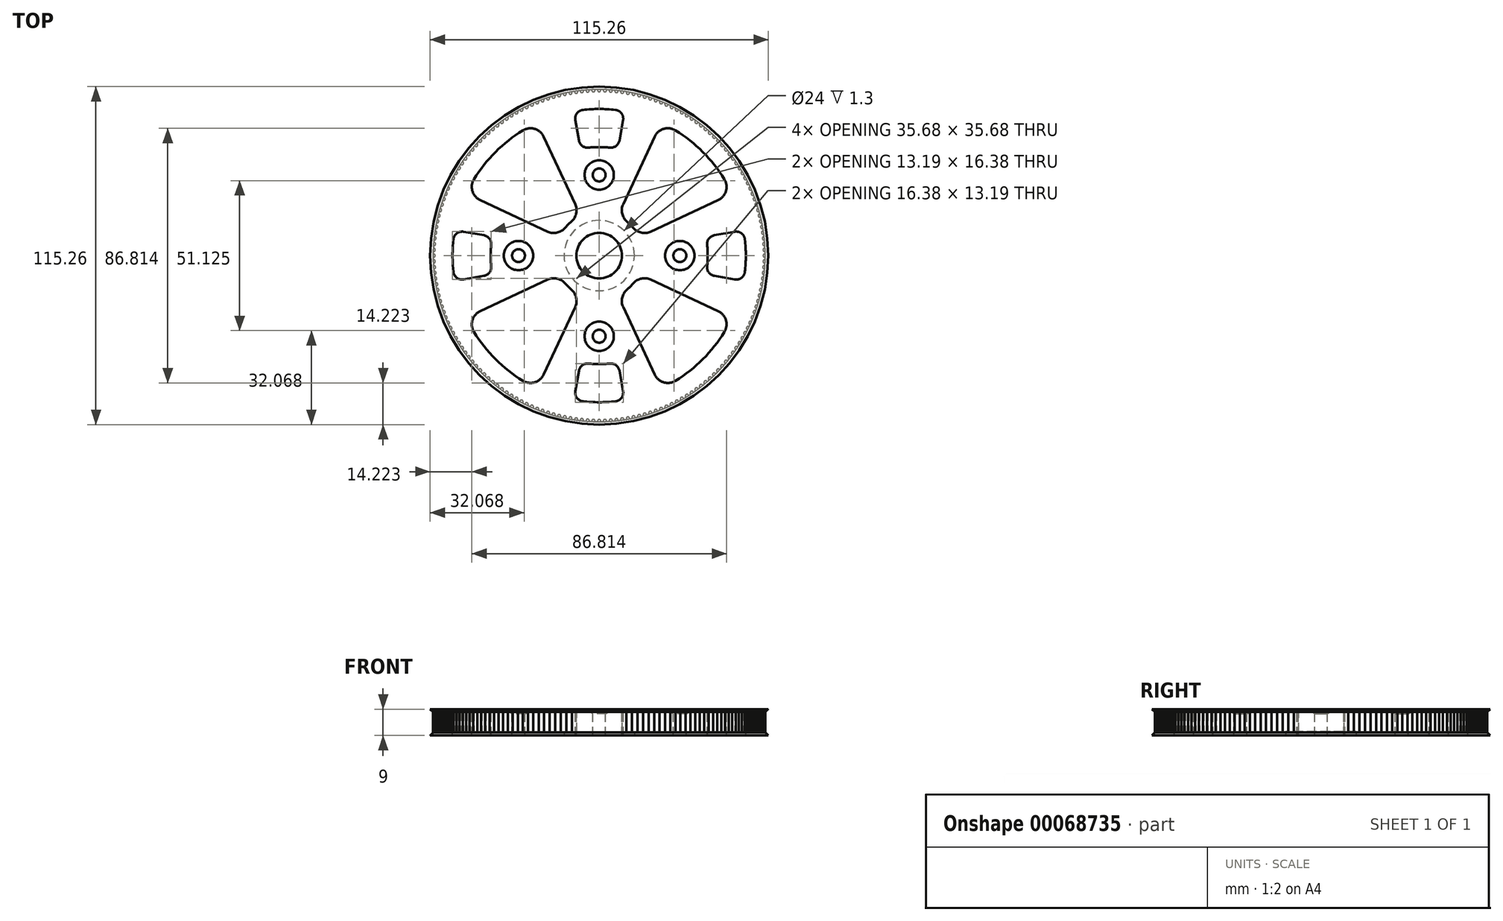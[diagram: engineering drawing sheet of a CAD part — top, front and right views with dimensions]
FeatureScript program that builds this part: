
annotation { "Feature Type Name" : "Feature", "Feature Type Description" : "" }
export const myFeature = defineFeature(function(context is Context, id is Id, definition is map)
    precondition{}
    {
        {
            var Q0;
            Q0=qCreatedBy(makeId("Top.planeOp"),FACE);
            var sketch = newSketch(context, id + "F0", { "sketchPlane" : qUnion([Q0])});
            skCircle(sketch, "E0", {"center": v(0, 0) * mm, "radius": 55.88 * mm, "construction": true});
            skCircle(sketch, "E1", {"center": v(0, 0) * mm, "radius": 56.63 * mm});
            skArc(sketch, "E2", {"start": v(0, -55.88) * mm, "mid": v(-0.3, -55.96) * mm, "end": v(-0.5, -56.2) * mm});
            skArc(sketch, "E3", {"start": v(-0.5, -56.2) * mm, "mid": v(-0.56, -56.32) * mm, "end": v(-0.59, -56.45) * mm});
            skArc(sketch, "E4", {"start": v(-0.59, -56.45) * mm, "mid": v(-0.66, -56.57) * mm, "end": v(-0.79, -56.62) * mm});
            skArc(sketch, "E5.MirrorCS", {"start": v(0, -55.88) * mm, "mid": v(0.3, -55.96) * mm, "end": v(0.5, -56.2) * mm});
            skArc(sketch, "E6.MirrorCS", {"start": v(0.5, -56.2) * mm, "mid": v(0.56, -56.32) * mm, "end": v(0.59, -56.45) * mm});
            skArc(sketch, "E7.MirrorCS", {"start": v(0.59, -56.45) * mm, "mid": v(0.66, -56.57) * mm, "end": v(0.79, -56.62) * mm});
            skArc(sketch, "E8.1.0", {"start": v(1.38, -56.44) * mm, "mid": v(1.32, -56.56) * mm, "end": v(1.19, -56.61) * mm});
            skArc(sketch, "E8.1.1", {"start": v(1.46, -56.18) * mm, "mid": v(1.41, -56.3) * mm, "end": v(1.38, -56.44) * mm});
            skArc(sketch, "E8.1.2", {"start": v(1.95, -55.84) * mm, "mid": v(1.65, -55.94) * mm, "end": v(1.46, -56.18) * mm});
            skArc(sketch, "E8.1.3", {"start": v(1.95, -55.84) * mm, "mid": v(2.25, -55.92) * mm, "end": v(2.47, -56.15) * mm});
            skArc(sketch, "E8.1.4", {"start": v(2.47, -56.15) * mm, "mid": v(2.52, -56.27) * mm, "end": v(2.56, -56.4) * mm});
            skArc(sketch, "E8.1.5", {"start": v(2.56, -56.4) * mm, "mid": v(2.63, -56.52) * mm, "end": v(2.76, -56.56) * mm});
            skArc(sketch, "E8.2.0", {"start": v(3.35, -56.36) * mm, "mid": v(3.3, -56.48) * mm, "end": v(3.16, -56.54) * mm});
            skArc(sketch, "E8.2.1", {"start": v(3.41, -56.1) * mm, "mid": v(3.37, -56.22) * mm, "end": v(3.35, -56.36) * mm});
            skArc(sketch, "E8.2.2", {"start": v(3.9, -55.74) * mm, "mid": v(3.6, -55.85) * mm, "end": v(3.41, -56.1) * mm});
            skArc(sketch, "E8.2.3", {"start": v(3.9, -55.74) * mm, "mid": v(4.2, -55.8) * mm, "end": v(4.43, -56.02) * mm});
            skArc(sketch, "E8.2.4", {"start": v(4.43, -56.02) * mm, "mid": v(4.48, -56.15) * mm, "end": v(4.52, -56.28) * mm});
            skArc(sketch, "E8.2.5", {"start": v(4.52, -56.28) * mm, "mid": v(4.6, -56.4) * mm, "end": v(4.74, -56.43) * mm});
            skArc(sketch, "E8.3.0", {"start": v(5.32, -56.2) * mm, "mid": v(5.26, -56.33) * mm, "end": v(5.14, -56.4) * mm});
            skArc(sketch, "E8.3.1", {"start": v(5.37, -55.94) * mm, "mid": v(5.33, -56.07) * mm, "end": v(5.32, -56.2) * mm});
            skArc(sketch, "E8.3.2", {"start": v(5.84, -55.57) * mm, "mid": v(5.55, -55.69) * mm, "end": v(5.37, -55.94) * mm});
            skArc(sketch, "E8.3.3", {"start": v(5.84, -55.57) * mm, "mid": v(6.15, -55.62) * mm, "end": v(6.38, -55.84) * mm});
            skArc(sketch, "E8.3.4", {"start": v(6.38, -55.84) * mm, "mid": v(6.44, -55.96) * mm, "end": v(6.49, -56.08) * mm});
            skArc(sketch, "E8.3.5", {"start": v(6.49, -56.08) * mm, "mid": v(6.57, -56.2) * mm, "end": v(6.7, -56.23) * mm});
            skArc(sketch, "E8.4.0", {"start": v(7.27, -55.99) * mm, "mid": v(7.22, -56.12) * mm, "end": v(7.1, -56.18) * mm});
            skArc(sketch, "E8.4.1", {"start": v(7.32, -55.72) * mm, "mid": v(7.29, -55.85) * mm, "end": v(7.27, -55.99) * mm});
            skArc(sketch, "E8.4.2", {"start": v(7.78, -55.33) * mm, "mid": v(7.5, -55.46) * mm, "end": v(7.32, -55.72) * mm});
            skArc(sketch, "E8.4.3", {"start": v(7.78, -55.33) * mm, "mid": v(8.09, -55.38) * mm, "end": v(8.32, -55.58) * mm});
            skArc(sketch, "E8.4.4", {"start": v(8.32, -55.58) * mm, "mid": v(8.39, -55.7) * mm, "end": v(8.44, -55.82) * mm});
            skArc(sketch, "E8.4.5", {"start": v(8.44, -55.82) * mm, "mid": v(8.52, -55.93) * mm, "end": v(8.66, -55.96) * mm});
            skArc(sketch, "E8.5.0", {"start": v(9.22, -55.7) * mm, "mid": v(9.18, -55.83) * mm, "end": v(9.06, -55.9) * mm});
            skArc(sketch, "E8.5.1", {"start": v(9.26, -55.43) * mm, "mid": v(9.23, -55.56) * mm, "end": v(9.22, -55.7) * mm});
            skArc(sketch, "E8.5.2", {"start": v(9.7, -55.03) * mm, "mid": v(9.42, -55.16) * mm, "end": v(9.26, -55.43) * mm});
            skArc(sketch, "E8.5.3", {"start": v(9.7, -55.03) * mm, "mid": v(10.01, -55.06) * mm, "end": v(10.26, -55.26) * mm});
            skArc(sketch, "E8.5.4", {"start": v(10.26, -55.26) * mm, "mid": v(10.33, -55.37) * mm, "end": v(10.38, -55.5) * mm});
            skArc(sketch, "E8.5.5", {"start": v(10.38, -55.5) * mm, "mid": v(10.47, -55.6) * mm, "end": v(10.6, -55.62) * mm});
            skArc(sketch, "E8.6.0", {"start": v(11.16, -55.34) * mm, "mid": v(11.12, -55.47) * mm, "end": v(11, -55.55) * mm});
            skArc(sketch, "E8.6.1", {"start": v(11.19, -55.07) * mm, "mid": v(11.17, -55.2) * mm, "end": v(11.16, -55.34) * mm});
            skArc(sketch, "E8.6.2", {"start": v(11.62, -54.65) * mm, "mid": v(11.34, -54.8) * mm, "end": v(11.19, -55.07) * mm});
            skArc(sketch, "E8.6.3", {"start": v(11.62, -54.65) * mm, "mid": v(11.93, -54.68) * mm, "end": v(12.18, -54.86) * mm});
            skArc(sketch, "E8.6.4", {"start": v(12.18, -54.86) * mm, "mid": v(12.25, -54.98) * mm, "end": v(12.31, -55.1) * mm});
            skArc(sketch, "E8.6.5", {"start": v(12.31, -55.1) * mm, "mid": v(12.4, -55.2) * mm, "end": v(12.54, -55.22) * mm});
            skArc(sketch, "E8.7.0", {"start": v(13.09, -54.92) * mm, "mid": v(13.05, -55.05) * mm, "end": v(12.93, -55.13) * mm});
            skArc(sketch, "E8.7.1", {"start": v(13.1, -54.65) * mm, "mid": v(13.09, -54.78) * mm, "end": v(13.09, -54.92) * mm});
            skArc(sketch, "E8.7.2", {"start": v(13.52, -54.22) * mm, "mid": v(13.25, -54.37) * mm, "end": v(13.1, -54.65) * mm});
            skArc(sketch, "E8.7.3", {"start": v(13.52, -54.22) * mm, "mid": v(13.83, -54.23) * mm, "end": v(14.09, -54.4) * mm});
            skArc(sketch, "E8.7.4", {"start": v(14.09, -54.4) * mm, "mid": v(14.17, -54.52) * mm, "end": v(14.23, -54.64) * mm});
            skArc(sketch, "E8.7.5", {"start": v(14.23, -54.64) * mm, "mid": v(14.32, -54.73) * mm, "end": v(14.46, -54.75) * mm});
            skArc(sketch, "E8.8.0", {"start": v(15, -54.43) * mm, "mid": v(14.96, -54.56) * mm, "end": v(14.85, -54.64) * mm});
            skArc(sketch, "E8.8.1", {"start": v(15, -54.16) * mm, "mid": v(15, -54.3) * mm, "end": v(15, -54.43) * mm});
            skArc(sketch, "E8.8.2", {"start": v(15.4, -53.71) * mm, "mid": v(15.14, -53.88) * mm, "end": v(15, -54.16) * mm});
            skArc(sketch, "E8.8.3", {"start": v(15.4, -53.71) * mm, "mid": v(15.71, -53.71) * mm, "end": v(15.98, -53.88) * mm});
            skArc(sketch, "E8.8.4", {"start": v(15.98, -53.88) * mm, "mid": v(16.06, -53.99) * mm, "end": v(16.13, -54.1) * mm});
            skArc(sketch, "E8.8.5", {"start": v(16.13, -54.1) * mm, "mid": v(16.23, -54.2) * mm, "end": v(16.36, -54.2) * mm});
            skArc(sketch, "E8.9.0", {"start": v(16.89, -53.87) * mm, "mid": v(16.86, -54) * mm, "end": v(16.75, -54.1) * mm});
            skArc(sketch, "E8.9.1", {"start": v(16.88, -53.6) * mm, "mid": v(16.88, -53.74) * mm, "end": v(16.89, -53.87) * mm});
            skArc(sketch, "E8.9.2", {"start": v(17.27, -53.14) * mm, "mid": v(17, -53.32) * mm, "end": v(16.88, -53.6) * mm});
            skArc(sketch, "E8.9.3", {"start": v(17.27, -53.14) * mm, "mid": v(17.58, -53.13) * mm, "end": v(17.85, -53.29) * mm});
            skArc(sketch, "E8.9.4", {"start": v(17.85, -53.29) * mm, "mid": v(17.93, -53.4) * mm, "end": v(18, -53.5) * mm});
            skArc(sketch, "E8.9.5", {"start": v(18, -53.5) * mm, "mid": v(18.1, -53.6) * mm, "end": v(18.25, -53.6) * mm});
            skArc(sketch, "E8.10.0", {"start": v(18.76, -53.25) * mm, "mid": v(18.73, -53.39) * mm, "end": v(18.63, -53.48) * mm});
            skArc(sketch, "E8.10.1", {"start": v(18.74, -52.98) * mm, "mid": v(18.74, -53.12) * mm, "end": v(18.76, -53.25) * mm});
            skArc(sketch, "E8.10.2", {"start": v(19.11, -52.5) * mm, "mid": v(18.86, -52.7) * mm, "end": v(18.74, -52.98) * mm});
            skArc(sketch, "E8.10.3", {"start": v(19.11, -52.5) * mm, "mid": v(19.42, -52.49) * mm, "end": v(19.7, -52.63) * mm});
            skArc(sketch, "E8.10.4", {"start": v(19.7, -52.63) * mm, "mid": v(19.79, -52.74) * mm, "end": v(19.86, -52.85) * mm});
            skArc(sketch, "E8.10.5", {"start": v(19.86, -52.85) * mm, "mid": v(19.97, -52.94) * mm, "end": v(20.1, -52.94) * mm});
            skArc(sketch, "E8.11.0", {"start": v(20.6, -52.56) * mm, "mid": v(20.58, -52.7) * mm, "end": v(20.48, -52.8) * mm});
            skArc(sketch, "E8.11.1", {"start": v(20.58, -52.3) * mm, "mid": v(20.58, -52.43) * mm, "end": v(20.6, -52.56) * mm});
            skArc(sketch, "E8.11.2", {"start": v(20.93, -51.8) * mm, "mid": v(20.69, -52) * mm, "end": v(20.58, -52.3) * mm});
            skArc(sketch, "E8.11.3", {"start": v(20.93, -51.8) * mm, "mid": v(21.24, -51.78) * mm, "end": v(21.52, -51.92) * mm});
            skArc(sketch, "E8.11.4", {"start": v(21.52, -51.92) * mm, "mid": v(21.61, -52.01) * mm, "end": v(21.7, -52.12) * mm});
            skArc(sketch, "E8.11.5", {"start": v(21.7, -52.12) * mm, "mid": v(21.8, -52.2) * mm, "end": v(21.94, -52.2) * mm});
            skArc(sketch, "E8.12.0", {"start": v(22.43, -51.81) * mm, "mid": v(22.41, -51.95) * mm, "end": v(22.31, -52.05) * mm});
            skArc(sketch, "E8.12.1", {"start": v(22.4, -51.54) * mm, "mid": v(22.4, -51.68) * mm, "end": v(22.43, -51.81) * mm});
            skArc(sketch, "E8.12.2", {"start": v(22.73, -51.05) * mm, "mid": v(22.49, -51.25) * mm, "end": v(22.4, -51.54) * mm});
            skArc(sketch, "E8.12.3", {"start": v(22.73, -51.05) * mm, "mid": v(23.04, -51) * mm, "end": v(23.32, -51.13) * mm});
            skArc(sketch, "E8.12.4", {"start": v(23.32, -51.13) * mm, "mid": v(23.42, -51.23) * mm, "end": v(23.5, -51.33) * mm});
            skArc(sketch, "E8.12.5", {"start": v(23.5, -51.33) * mm, "mid": v(23.61, -51.42) * mm, "end": v(23.75, -51.4) * mm});
            skArc(sketch, "E8.13.0", {"start": v(24.22, -51) * mm, "mid": v(24.2, -51.14) * mm, "end": v(24.11, -51.24) * mm});
            skArc(sketch, "E8.13.1", {"start": v(24.18, -50.73) * mm, "mid": v(24.2, -50.87) * mm, "end": v(24.22, -51) * mm});
            skArc(sketch, "E8.13.2", {"start": v(24.5, -50.22) * mm, "mid": v(24.26, -50.43) * mm, "end": v(24.18, -50.73) * mm});
            skArc(sketch, "E8.13.3", {"start": v(24.5, -50.22) * mm, "mid": v(24.8, -50.17) * mm, "end": v(25.1, -50.29) * mm});
            skArc(sketch, "E8.13.4", {"start": v(25.1, -50.29) * mm, "mid": v(25.19, -50.38) * mm, "end": v(25.28, -50.48) * mm});
            skArc(sketch, "E8.13.5", {"start": v(25.28, -50.48) * mm, "mid": v(25.4, -50.56) * mm, "end": v(25.53, -50.54) * mm});
            skArc(sketch, "E8.14.0", {"start": v(25.98, -50.12) * mm, "mid": v(25.98, -50.26) * mm, "end": v(25.89, -50.36) * mm});
            skArc(sketch, "E8.14.1", {"start": v(25.94, -49.86) * mm, "mid": v(25.95, -50) * mm, "end": v(25.98, -50.12) * mm});
            skArc(sketch, "E8.14.2", {"start": v(26.23, -49.34) * mm, "mid": v(26, -49.55) * mm, "end": v(25.94, -49.86) * mm});
            skArc(sketch, "E8.14.3", {"start": v(26.23, -49.34) * mm, "mid": v(26.54, -49.27) * mm, "end": v(26.83, -49.38) * mm});
            skArc(sketch, "E8.14.4", {"start": v(26.83, -49.38) * mm, "mid": v(26.93, -49.47) * mm, "end": v(27.02, -49.57) * mm});
            skArc(sketch, "E8.14.5", {"start": v(27.02, -49.57) * mm, "mid": v(27.14, -49.64) * mm, "end": v(27.28, -49.62) * mm});
            skArc(sketch, "E8.15.0", {"start": v(27.72, -49.18) * mm, "mid": v(27.72, -49.32) * mm, "end": v(27.63, -49.43) * mm});
            skArc(sketch, "E8.15.1", {"start": v(27.66, -48.92) * mm, "mid": v(27.68, -49.05) * mm, "end": v(27.72, -49.18) * mm});
            skArc(sketch, "E8.15.2", {"start": v(27.94, -48.39) * mm, "mid": v(27.72, -48.62) * mm, "end": v(27.66, -48.92) * mm});
            skArc(sketch, "E8.15.3", {"start": v(27.94, -48.39) * mm, "mid": v(28.24, -48.32) * mm, "end": v(28.54, -48.41) * mm});
            skArc(sketch, "E8.15.4", {"start": v(28.54, -48.41) * mm, "mid": v(28.64, -48.5) * mm, "end": v(28.74, -48.6) * mm});
            skArc(sketch, "E8.15.5", {"start": v(28.74, -48.6) * mm, "mid": v(28.86, -48.67) * mm, "end": v(29, -48.64) * mm});
            skArc(sketch, "E8.16.0", {"start": v(29.42, -48.19) * mm, "mid": v(29.42, -48.33) * mm, "end": v(29.34, -48.43) * mm});
            skArc(sketch, "E8.16.1", {"start": v(29.35, -47.93) * mm, "mid": v(29.38, -48.06) * mm, "end": v(29.42, -48.19) * mm});
            skArc(sketch, "E8.16.2", {"start": v(29.6, -47.39) * mm, "mid": v(29.4, -47.62) * mm, "end": v(29.35, -47.93) * mm});
            skArc(sketch, "E8.16.3", {"start": v(29.6, -47.39) * mm, "mid": v(29.91, -47.3) * mm, "end": v(30.2, -47.39) * mm});
            skArc(sketch, "E8.16.4", {"start": v(30.2, -47.39) * mm, "mid": v(30.32, -47.47) * mm, "end": v(30.41, -47.56) * mm});
            skArc(sketch, "E8.16.5", {"start": v(30.41, -47.56) * mm, "mid": v(30.54, -47.63) * mm, "end": v(30.67, -47.6) * mm});
            skArc(sketch, "E8.17.0", {"start": v(31.08, -47.13) * mm, "mid": v(31.1, -47.27) * mm, "end": v(31, -47.38) * mm});
            skArc(sketch, "E8.17.1", {"start": v(31, -46.87) * mm, "mid": v(31.03, -47) * mm, "end": v(31.08, -47.13) * mm});
            skArc(sketch, "E8.17.2", {"start": v(31.25, -46.32) * mm, "mid": v(31.05, -46.56) * mm, "end": v(31, -46.87) * mm});
            skArc(sketch, "E8.17.3", {"start": v(31.25, -46.32) * mm, "mid": v(31.54, -46.23) * mm, "end": v(31.84, -46.3) * mm});
            skArc(sketch, "E8.17.4", {"start": v(31.84, -46.3) * mm, "mid": v(31.96, -46.38) * mm, "end": v(32.06, -46.47) * mm});
            skArc(sketch, "E8.17.5", {"start": v(32.06, -46.47) * mm, "mid": v(32.18, -46.53) * mm, "end": v(32.31, -46.5) * mm});
            skArc(sketch, "E8.18.0", {"start": v(32.7, -46.02) * mm, "mid": v(32.72, -46.16) * mm, "end": v(32.64, -46.27) * mm});
            skArc(sketch, "E8.18.1", {"start": v(32.62, -45.76) * mm, "mid": v(32.66, -45.9) * mm, "end": v(32.7, -46.02) * mm});
            skArc(sketch, "E8.18.2", {"start": v(32.84, -45.2) * mm, "mid": v(32.65, -45.45) * mm, "end": v(32.62, -45.76) * mm});
            skArc(sketch, "E8.18.3", {"start": v(32.84, -45.2) * mm, "mid": v(33.14, -45.1) * mm, "end": v(33.44, -45.17) * mm});
            skArc(sketch, "E8.18.4", {"start": v(33.44, -45.17) * mm, "mid": v(33.56, -45.24) * mm, "end": v(33.66, -45.33) * mm});
            skArc(sketch, "E8.18.5", {"start": v(33.66, -45.33) * mm, "mid": v(33.78, -45.38) * mm, "end": v(33.92, -45.34) * mm});
            skArc(sketch, "E8.19.0", {"start": v(34.3, -44.85) * mm, "mid": v(34.31, -44.99) * mm, "end": v(34.24, -45.1) * mm});
            skArc(sketch, "E8.19.1", {"start": v(34.2, -44.6) * mm, "mid": v(34.24, -44.73) * mm, "end": v(34.3, -44.85) * mm});
            skArc(sketch, "E8.19.2", {"start": v(34.4, -44.03) * mm, "mid": v(34.22, -44.28) * mm, "end": v(34.2, -44.6) * mm});
            skArc(sketch, "E8.19.3", {"start": v(34.4, -44.03) * mm, "mid": v(34.7, -43.91) * mm, "end": v(35, -43.97) * mm});
            skArc(sketch, "E8.19.4", {"start": v(35, -43.97) * mm, "mid": v(35.11, -44.04) * mm, "end": v(35.22, -44.12) * mm});
            skArc(sketch, "E8.19.5", {"start": v(35.22, -44.12) * mm, "mid": v(35.35, -44.18) * mm, "end": v(35.48, -44.13) * mm});
            skArc(sketch, "E8.20.0", {"start": v(35.84, -43.62) * mm, "mid": v(35.86, -43.76) * mm, "end": v(35.8, -43.88) * mm});
            skArc(sketch, "E8.20.1", {"start": v(35.73, -43.37) * mm, "mid": v(35.78, -43.5) * mm, "end": v(35.84, -43.62) * mm});
            skArc(sketch, "E8.20.2", {"start": v(35.92, -42.8) * mm, "mid": v(35.74, -43.06) * mm, "end": v(35.73, -43.37) * mm});
            skArc(sketch, "E8.20.3", {"start": v(35.92, -42.8) * mm, "mid": v(36.2, -42.68) * mm, "end": v(36.51, -42.72) * mm});
            skArc(sketch, "E8.20.4", {"start": v(36.51, -42.72) * mm, "mid": v(36.63, -42.79) * mm, "end": v(36.74, -42.87) * mm});
            skArc(sketch, "E8.20.5", {"start": v(36.74, -42.87) * mm, "mid": v(36.87, -42.92) * mm, "end": v(37, -42.87) * mm});
            skArc(sketch, "E8.21.0", {"start": v(37.34, -42.35) * mm, "mid": v(37.37, -42.48) * mm, "end": v(37.3, -42.6) * mm});
            skArc(sketch, "E8.21.1", {"start": v(37.23, -42.1) * mm, "mid": v(37.27, -42.23) * mm, "end": v(37.34, -42.35) * mm});
            skArc(sketch, "E8.21.2", {"start": v(37.39, -41.52) * mm, "mid": v(37.22, -41.79) * mm, "end": v(37.23, -42.1) * mm});
            skArc(sketch, "E8.21.3", {"start": v(37.39, -41.52) * mm, "mid": v(37.67, -41.39) * mm, "end": v(37.98, -41.42) * mm});
            skArc(sketch, "E8.21.4", {"start": v(37.98, -41.42) * mm, "mid": v(38.1, -41.48) * mm, "end": v(38.21, -41.56) * mm});
            skArc(sketch, "E8.21.5", {"start": v(38.21, -41.56) * mm, "mid": v(38.34, -41.6) * mm, "end": v(38.47, -41.55) * mm});
            skArc(sketch, "E8.22.0", {"start": v(38.8, -41.02) * mm, "mid": v(38.83, -41.15) * mm, "end": v(38.77, -41.28) * mm});
            skArc(sketch, "E8.22.1", {"start": v(38.67, -40.78) * mm, "mid": v(38.73, -40.9) * mm, "end": v(38.8, -41.02) * mm});
            skArc(sketch, "E8.22.2", {"start": v(38.81, -40.2) * mm, "mid": v(38.66, -40.46) * mm, "end": v(38.67, -40.78) * mm});
            skArc(sketch, "E8.22.3", {"start": v(38.81, -40.2) * mm, "mid": v(39.1, -40.05) * mm, "end": v(39.4, -40.07) * mm});
            skArc(sketch, "E8.22.4", {"start": v(39.4, -40.07) * mm, "mid": v(39.52, -40.13) * mm, "end": v(39.64, -40.2) * mm});
            skArc(sketch, "E8.22.5", {"start": v(39.64, -40.2) * mm, "mid": v(39.77, -40.24) * mm, "end": v(39.9, -40.18) * mm});
            skArc(sketch, "E8.23.0", {"start": v(40.2, -39.64) * mm, "mid": v(40.24, -39.77) * mm, "end": v(40.18, -39.9) * mm});
            skArc(sketch, "E8.23.1", {"start": v(40.07, -39.4) * mm, "mid": v(40.13, -39.52) * mm, "end": v(40.2, -39.64) * mm});
            skArc(sketch, "E8.23.2", {"start": v(40.2, -38.81) * mm, "mid": v(40.05, -39.1) * mm, "end": v(40.07, -39.4) * mm});
            skArc(sketch, "E8.23.3", {"start": v(40.2, -38.81) * mm, "mid": v(40.46, -38.66) * mm, "end": v(40.78, -38.67) * mm});
            skArc(sketch, "E8.23.4", {"start": v(40.78, -38.67) * mm, "mid": v(40.9, -38.73) * mm, "end": v(41.02, -38.8) * mm});
            skArc(sketch, "E8.23.5", {"start": v(41.02, -38.8) * mm, "mid": v(41.15, -38.83) * mm, "end": v(41.28, -38.77) * mm});
            skArc(sketch, "E8.24.0", {"start": v(41.56, -38.21) * mm, "mid": v(41.6, -38.34) * mm, "end": v(41.55, -38.47) * mm});
            skArc(sketch, "E8.24.1", {"start": v(41.42, -37.98) * mm, "mid": v(41.48, -38.1) * mm, "end": v(41.56, -38.21) * mm});
            skArc(sketch, "E8.24.2", {"start": v(41.52, -37.39) * mm, "mid": v(41.39, -37.67) * mm, "end": v(41.42, -37.98) * mm});
            skArc(sketch, "E8.24.3", {"start": v(41.52, -37.39) * mm, "mid": v(41.79, -37.22) * mm, "end": v(42.1, -37.23) * mm});
            skArc(sketch, "E8.24.4", {"start": v(42.1, -37.23) * mm, "mid": v(42.23, -37.27) * mm, "end": v(42.35, -37.34) * mm});
            skArc(sketch, "E8.24.5", {"start": v(42.35, -37.34) * mm, "mid": v(42.48, -37.37) * mm, "end": v(42.6, -37.3) * mm});
            skArc(sketch, "E8.25.0", {"start": v(42.87, -36.74) * mm, "mid": v(42.92, -36.87) * mm, "end": v(42.87, -37) * mm});
            skArc(sketch, "E8.25.1", {"start": v(42.72, -36.51) * mm, "mid": v(42.79, -36.63) * mm, "end": v(42.87, -36.74) * mm});
            skArc(sketch, "E8.25.2", {"start": v(42.8, -35.92) * mm, "mid": v(42.68, -36.2) * mm, "end": v(42.72, -36.51) * mm});
            skArc(sketch, "E8.25.3", {"start": v(42.8, -35.92) * mm, "mid": v(43.06, -35.74) * mm, "end": v(43.37, -35.73) * mm});
            skArc(sketch, "E8.25.4", {"start": v(43.37, -35.73) * mm, "mid": v(43.5, -35.78) * mm, "end": v(43.62, -35.84) * mm});
            skArc(sketch, "E8.25.5", {"start": v(43.62, -35.84) * mm, "mid": v(43.76, -35.86) * mm, "end": v(43.88, -35.8) * mm});
            skArc(sketch, "E8.26.0", {"start": v(44.12, -35.22) * mm, "mid": v(44.18, -35.35) * mm, "end": v(44.13, -35.48) * mm});
            skArc(sketch, "E8.26.1", {"start": v(43.97, -35) * mm, "mid": v(44.04, -35.11) * mm, "end": v(44.12, -35.22) * mm});
            skArc(sketch, "E8.26.2", {"start": v(44.03, -34.4) * mm, "mid": v(43.91, -34.7) * mm, "end": v(43.97, -35) * mm});
            skArc(sketch, "E8.26.3", {"start": v(44.03, -34.4) * mm, "mid": v(44.28, -34.22) * mm, "end": v(44.6, -34.2) * mm});
            skArc(sketch, "E8.26.4", {"start": v(44.6, -34.2) * mm, "mid": v(44.73, -34.24) * mm, "end": v(44.85, -34.3) * mm});
            skArc(sketch, "E8.26.5", {"start": v(44.85, -34.3) * mm, "mid": v(44.99, -34.31) * mm, "end": v(45.1, -34.24) * mm});
            skArc(sketch, "E8.27.0", {"start": v(45.33, -33.66) * mm, "mid": v(45.38, -33.78) * mm, "end": v(45.34, -33.92) * mm});
            skArc(sketch, "E8.27.1", {"start": v(45.17, -33.44) * mm, "mid": v(45.24, -33.56) * mm, "end": v(45.33, -33.66) * mm});
            skArc(sketch, "E8.27.2", {"start": v(45.2, -32.84) * mm, "mid": v(45.1, -33.14) * mm, "end": v(45.17, -33.44) * mm});
            skArc(sketch, "E8.27.3", {"start": v(45.2, -32.84) * mm, "mid": v(45.45, -32.65) * mm, "end": v(45.76, -32.62) * mm});
            skArc(sketch, "E8.27.4", {"start": v(45.76, -32.62) * mm, "mid": v(45.9, -32.66) * mm, "end": v(46.02, -32.7) * mm});
            skArc(sketch, "E8.27.5", {"start": v(46.02, -32.7) * mm, "mid": v(46.16, -32.72) * mm, "end": v(46.27, -32.64) * mm});
            skArc(sketch, "E8.28.0", {"start": v(46.47, -32.06) * mm, "mid": v(46.53, -32.18) * mm, "end": v(46.5, -32.31) * mm});
            skArc(sketch, "E8.28.1", {"start": v(46.3, -31.84) * mm, "mid": v(46.38, -31.96) * mm, "end": v(46.47, -32.06) * mm});
            skArc(sketch, "E8.28.2", {"start": v(46.32, -31.25) * mm, "mid": v(46.23, -31.54) * mm, "end": v(46.3, -31.84) * mm});
            skArc(sketch, "E8.28.3", {"start": v(46.32, -31.25) * mm, "mid": v(46.56, -31.05) * mm, "end": v(46.87, -31) * mm});
            skArc(sketch, "E8.28.4", {"start": v(46.87, -31) * mm, "mid": v(47, -31.03) * mm, "end": v(47.13, -31.08) * mm});
            skArc(sketch, "E8.28.5", {"start": v(47.13, -31.08) * mm, "mid": v(47.27, -31.1) * mm, "end": v(47.38, -31) * mm});
            skArc(sketch, "E8.29.0", {"start": v(47.56, -30.41) * mm, "mid": v(47.63, -30.54) * mm, "end": v(47.6, -30.67) * mm});
            skArc(sketch, "E8.29.1", {"start": v(47.39, -30.2) * mm, "mid": v(47.47, -30.32) * mm, "end": v(47.56, -30.41) * mm});
            skArc(sketch, "E8.29.2", {"start": v(47.39, -29.6) * mm, "mid": v(47.3, -29.91) * mm, "end": v(47.39, -30.2) * mm});
            skArc(sketch, "E8.29.3", {"start": v(47.39, -29.6) * mm, "mid": v(47.62, -29.4) * mm, "end": v(47.93, -29.35) * mm});
            skArc(sketch, "E8.29.4", {"start": v(47.93, -29.35) * mm, "mid": v(48.06, -29.38) * mm, "end": v(48.19, -29.42) * mm});
            skArc(sketch, "E8.29.5", {"start": v(48.19, -29.42) * mm, "mid": v(48.33, -29.42) * mm, "end": v(48.43, -29.34) * mm});
            skArc(sketch, "E8.30.0", {"start": v(48.6, -28.74) * mm, "mid": v(48.67, -28.86) * mm, "end": v(48.64, -29) * mm});
            skArc(sketch, "E8.30.1", {"start": v(48.41, -28.54) * mm, "mid": v(48.5, -28.64) * mm, "end": v(48.6, -28.74) * mm});
            skArc(sketch, "E8.30.2", {"start": v(48.39, -27.94) * mm, "mid": v(48.32, -28.24) * mm, "end": v(48.41, -28.54) * mm});
            skArc(sketch, "E8.30.3", {"start": v(48.39, -27.94) * mm, "mid": v(48.62, -27.72) * mm, "end": v(48.92, -27.66) * mm});
            skArc(sketch, "E8.30.4", {"start": v(48.92, -27.66) * mm, "mid": v(49.05, -27.68) * mm, "end": v(49.18, -27.72) * mm});
            skArc(sketch, "E8.30.5", {"start": v(49.18, -27.72) * mm, "mid": v(49.32, -27.72) * mm, "end": v(49.43, -27.63) * mm});
            skArc(sketch, "E8.31.0", {"start": v(49.57, -27.02) * mm, "mid": v(49.64, -27.14) * mm, "end": v(49.62, -27.28) * mm});
            skArc(sketch, "E8.31.1", {"start": v(49.38, -26.83) * mm, "mid": v(49.47, -26.93) * mm, "end": v(49.57, -27.02) * mm});
            skArc(sketch, "E8.31.2", {"start": v(49.34, -26.23) * mm, "mid": v(49.27, -26.54) * mm, "end": v(49.38, -26.83) * mm});
            skArc(sketch, "E8.31.3", {"start": v(49.34, -26.23) * mm, "mid": v(49.55, -26) * mm, "end": v(49.86, -25.94) * mm});
            skArc(sketch, "E8.31.4", {"start": v(49.86, -25.94) * mm, "mid": v(50, -25.95) * mm, "end": v(50.12, -25.98) * mm});
            skArc(sketch, "E8.31.5", {"start": v(50.12, -25.98) * mm, "mid": v(50.26, -25.98) * mm, "end": v(50.36, -25.89) * mm});
            skArc(sketch, "E8.32.0", {"start": v(50.48, -25.28) * mm, "mid": v(50.56, -25.4) * mm, "end": v(50.54, -25.53) * mm});
            skArc(sketch, "E8.32.1", {"start": v(50.29, -25.1) * mm, "mid": v(50.38, -25.19) * mm, "end": v(50.48, -25.28) * mm});
            skArc(sketch, "E8.32.2", {"start": v(50.22, -24.5) * mm, "mid": v(50.17, -24.8) * mm, "end": v(50.29, -25.1) * mm});
            skArc(sketch, "E8.32.3", {"start": v(50.22, -24.5) * mm, "mid": v(50.43, -24.26) * mm, "end": v(50.73, -24.18) * mm});
            skArc(sketch, "E8.32.4", {"start": v(50.73, -24.18) * mm, "mid": v(50.87, -24.2) * mm, "end": v(51, -24.22) * mm});
            skArc(sketch, "E8.32.5", {"start": v(51, -24.22) * mm, "mid": v(51.14, -24.2) * mm, "end": v(51.24, -24.11) * mm});
            skArc(sketch, "E8.33.0", {"start": v(51.33, -23.5) * mm, "mid": v(51.42, -23.61) * mm, "end": v(51.4, -23.75) * mm});
            skArc(sketch, "E8.33.1", {"start": v(51.13, -23.32) * mm, "mid": v(51.23, -23.42) * mm, "end": v(51.33, -23.5) * mm});
            skArc(sketch, "E8.33.2", {"start": v(51.05, -22.73) * mm, "mid": v(51, -23.04) * mm, "end": v(51.13, -23.32) * mm});
            skArc(sketch, "E8.33.3", {"start": v(51.05, -22.73) * mm, "mid": v(51.25, -22.49) * mm, "end": v(51.54, -22.4) * mm});
            skArc(sketch, "E8.33.4", {"start": v(51.54, -22.4) * mm, "mid": v(51.68, -22.4) * mm, "end": v(51.81, -22.43) * mm});
            skArc(sketch, "E8.33.5", {"start": v(51.81, -22.43) * mm, "mid": v(51.95, -22.41) * mm, "end": v(52.05, -22.31) * mm});
            skArc(sketch, "E8.34.0", {"start": v(52.12, -21.7) * mm, "mid": v(52.2, -21.8) * mm, "end": v(52.2, -21.94) * mm});
            skArc(sketch, "E8.34.1", {"start": v(51.92, -21.52) * mm, "mid": v(52.01, -21.61) * mm, "end": v(52.12, -21.7) * mm});
            skArc(sketch, "E8.34.2", {"start": v(51.8, -20.93) * mm, "mid": v(51.78, -21.24) * mm, "end": v(51.92, -21.52) * mm});
            skArc(sketch, "E8.34.3", {"start": v(51.8, -20.93) * mm, "mid": v(52, -20.69) * mm, "end": v(52.3, -20.58) * mm});
            skArc(sketch, "E8.34.4", {"start": v(52.3, -20.58) * mm, "mid": v(52.43, -20.58) * mm, "end": v(52.56, -20.6) * mm});
            skArc(sketch, "E8.34.5", {"start": v(52.56, -20.6) * mm, "mid": v(52.7, -20.58) * mm, "end": v(52.8, -20.48) * mm});
            skArc(sketch, "E8.35.0", {"start": v(52.85, -19.86) * mm, "mid": v(52.94, -19.97) * mm, "end": v(52.94, -20.1) * mm});
            skArc(sketch, "E8.35.1", {"start": v(52.63, -19.7) * mm, "mid": v(52.74, -19.79) * mm, "end": v(52.85, -19.86) * mm});
            skArc(sketch, "E8.35.2", {"start": v(52.5, -19.11) * mm, "mid": v(52.49, -19.42) * mm, "end": v(52.63, -19.7) * mm});
            skArc(sketch, "E8.35.3", {"start": v(52.5, -19.11) * mm, "mid": v(52.7, -18.86) * mm, "end": v(52.98, -18.74) * mm});
            skArc(sketch, "E8.35.4", {"start": v(52.98, -18.74) * mm, "mid": v(53.12, -18.74) * mm, "end": v(53.25, -18.76) * mm});
            skArc(sketch, "E8.35.5", {"start": v(53.25, -18.76) * mm, "mid": v(53.39, -18.73) * mm, "end": v(53.48, -18.63) * mm});
            skArc(sketch, "E8.36.0", {"start": v(53.5, -18) * mm, "mid": v(53.6, -18.1) * mm, "end": v(53.6, -18.25) * mm});
            skArc(sketch, "E8.36.1", {"start": v(53.29, -17.85) * mm, "mid": v(53.4, -17.93) * mm, "end": v(53.5, -18) * mm});
            skArc(sketch, "E8.36.2", {"start": v(53.14, -17.27) * mm, "mid": v(53.13, -17.58) * mm, "end": v(53.29, -17.85) * mm});
            skArc(sketch, "E8.36.3", {"start": v(53.14, -17.27) * mm, "mid": v(53.32, -17) * mm, "end": v(53.6, -16.88) * mm});
            skArc(sketch, "E8.36.4", {"start": v(53.6, -16.88) * mm, "mid": v(53.74, -16.88) * mm, "end": v(53.87, -16.89) * mm});
            skArc(sketch, "E8.36.5", {"start": v(53.87, -16.89) * mm, "mid": v(54, -16.86) * mm, "end": v(54.1, -16.75) * mm});
            skArc(sketch, "E8.37.0", {"start": v(54.1, -16.13) * mm, "mid": v(54.2, -16.23) * mm, "end": v(54.2, -16.36) * mm});
            skArc(sketch, "E8.37.1", {"start": v(53.88, -15.98) * mm, "mid": v(53.99, -16.06) * mm, "end": v(54.1, -16.13) * mm});
            skArc(sketch, "E8.37.2", {"start": v(53.71, -15.4) * mm, "mid": v(53.71, -15.71) * mm, "end": v(53.88, -15.98) * mm});
            skArc(sketch, "E8.37.3", {"start": v(53.71, -15.4) * mm, "mid": v(53.88, -15.14) * mm, "end": v(54.16, -15) * mm});
            skArc(sketch, "E8.37.4", {"start": v(54.16, -15) * mm, "mid": v(54.3, -15) * mm, "end": v(54.43, -15) * mm});
            skArc(sketch, "E8.37.5", {"start": v(54.43, -15) * mm, "mid": v(54.56, -14.96) * mm, "end": v(54.64, -14.85) * mm});
            skArc(sketch, "E8.38.0", {"start": v(54.64, -14.23) * mm, "mid": v(54.73, -14.32) * mm, "end": v(54.75, -14.46) * mm});
            skArc(sketch, "E8.38.1", {"start": v(54.4, -14.09) * mm, "mid": v(54.52, -14.17) * mm, "end": v(54.64, -14.23) * mm});
            skArc(sketch, "E8.38.2", {"start": v(54.22, -13.52) * mm, "mid": v(54.23, -13.83) * mm, "end": v(54.4, -14.09) * mm});
            skArc(sketch, "E8.38.3", {"start": v(54.22, -13.52) * mm, "mid": v(54.37, -13.25) * mm, "end": v(54.65, -13.1) * mm});
            skArc(sketch, "E8.38.4", {"start": v(54.65, -13.1) * mm, "mid": v(54.78, -13.09) * mm, "end": v(54.92, -13.09) * mm});
            skArc(sketch, "E8.38.5", {"start": v(54.92, -13.09) * mm, "mid": v(55.05, -13.05) * mm, "end": v(55.13, -12.93) * mm});
            skArc(sketch, "E8.39.0", {"start": v(55.1, -12.31) * mm, "mid": v(55.2, -12.4) * mm, "end": v(55.22, -12.54) * mm});
            skArc(sketch, "E8.39.1", {"start": v(54.86, -12.18) * mm, "mid": v(54.98, -12.25) * mm, "end": v(55.1, -12.31) * mm});
            skArc(sketch, "E8.39.2", {"start": v(54.65, -11.62) * mm, "mid": v(54.68, -11.93) * mm, "end": v(54.86, -12.18) * mm});
            skArc(sketch, "E8.39.3", {"start": v(54.65, -11.62) * mm, "mid": v(54.8, -11.34) * mm, "end": v(55.07, -11.19) * mm});
            skArc(sketch, "E8.39.4", {"start": v(55.07, -11.19) * mm, "mid": v(55.2, -11.17) * mm, "end": v(55.34, -11.16) * mm});
            skArc(sketch, "E8.39.5", {"start": v(55.34, -11.16) * mm, "mid": v(55.47, -11.12) * mm, "end": v(55.55, -11) * mm});
            skArc(sketch, "E8.40.0", {"start": v(55.5, -10.38) * mm, "mid": v(55.6, -10.47) * mm, "end": v(55.62, -10.6) * mm});
            skArc(sketch, "E8.40.1", {"start": v(55.26, -10.26) * mm, "mid": v(55.37, -10.33) * mm, "end": v(55.5, -10.38) * mm});
            skArc(sketch, "E8.40.2", {"start": v(55.03, -9.7) * mm, "mid": v(55.06, -10.01) * mm, "end": v(55.26, -10.26) * mm});
            skArc(sketch, "E8.40.3", {"start": v(55.03, -9.7) * mm, "mid": v(55.16, -9.42) * mm, "end": v(55.43, -9.26) * mm});
            skArc(sketch, "E8.40.4", {"start": v(55.43, -9.26) * mm, "mid": v(55.56, -9.23) * mm, "end": v(55.7, -9.22) * mm});
            skArc(sketch, "E8.40.5", {"start": v(55.7, -9.22) * mm, "mid": v(55.83, -9.18) * mm, "end": v(55.9, -9.06) * mm});
            skArc(sketch, "E8.41.0", {"start": v(55.82, -8.44) * mm, "mid": v(55.93, -8.52) * mm, "end": v(55.96, -8.66) * mm});
            skArc(sketch, "E8.41.1", {"start": v(55.58, -8.32) * mm, "mid": v(55.7, -8.39) * mm, "end": v(55.82, -8.44) * mm});
            skArc(sketch, "E8.41.2", {"start": v(55.33, -7.78) * mm, "mid": v(55.38, -8.09) * mm, "end": v(55.58, -8.32) * mm});
            skArc(sketch, "E8.41.3", {"start": v(55.33, -7.78) * mm, "mid": v(55.46, -7.5) * mm, "end": v(55.72, -7.32) * mm});
            skArc(sketch, "E8.41.4", {"start": v(55.72, -7.32) * mm, "mid": v(55.85, -7.29) * mm, "end": v(55.99, -7.27) * mm});
            skArc(sketch, "E8.41.5", {"start": v(55.99, -7.27) * mm, "mid": v(56.12, -7.22) * mm, "end": v(56.18, -7.1) * mm});
            skArc(sketch, "E8.42.0", {"start": v(56.08, -6.49) * mm, "mid": v(56.2, -6.57) * mm, "end": v(56.23, -6.7) * mm});
            skArc(sketch, "E8.42.1", {"start": v(55.84, -6.38) * mm, "mid": v(55.96, -6.44) * mm, "end": v(56.08, -6.49) * mm});
            skArc(sketch, "E8.42.2", {"start": v(55.57, -5.84) * mm, "mid": v(55.62, -6.15) * mm, "end": v(55.84, -6.38) * mm});
            skArc(sketch, "E8.42.3", {"start": v(55.57, -5.84) * mm, "mid": v(55.69, -5.55) * mm, "end": v(55.94, -5.37) * mm});
            skArc(sketch, "E8.42.4", {"start": v(55.94, -5.37) * mm, "mid": v(56.07, -5.33) * mm, "end": v(56.2, -5.32) * mm});
            skArc(sketch, "E8.42.5", {"start": v(56.2, -5.32) * mm, "mid": v(56.33, -5.26) * mm, "end": v(56.4, -5.14) * mm});
            skArc(sketch, "E8.43.0", {"start": v(56.28, -4.52) * mm, "mid": v(56.4, -4.6) * mm, "end": v(56.43, -4.74) * mm});
            skArc(sketch, "E8.43.1", {"start": v(56.02, -4.43) * mm, "mid": v(56.15, -4.48) * mm, "end": v(56.28, -4.52) * mm});
            skArc(sketch, "E8.43.2", {"start": v(55.74, -3.9) * mm, "mid": v(55.8, -4.2) * mm, "end": v(56.02, -4.43) * mm});
            skArc(sketch, "E8.43.3", {"start": v(55.74, -3.9) * mm, "mid": v(55.85, -3.6) * mm, "end": v(56.1, -3.41) * mm});
            skArc(sketch, "E8.43.4", {"start": v(56.1, -3.41) * mm, "mid": v(56.22, -3.37) * mm, "end": v(56.36, -3.35) * mm});
            skArc(sketch, "E8.43.5", {"start": v(56.36, -3.35) * mm, "mid": v(56.48, -3.3) * mm, "end": v(56.54, -3.16) * mm});
            skArc(sketch, "E8.44.0", {"start": v(56.4, -2.56) * mm, "mid": v(56.52, -2.63) * mm, "end": v(56.56, -2.76) * mm});
            skArc(sketch, "E8.44.1", {"start": v(56.15, -2.47) * mm, "mid": v(56.27, -2.52) * mm, "end": v(56.4, -2.56) * mm});
            skArc(sketch, "E8.44.2", {"start": v(55.84, -1.95) * mm, "mid": v(55.92, -2.25) * mm, "end": v(56.15, -2.47) * mm});
            skArc(sketch, "E8.44.3", {"start": v(55.84, -1.95) * mm, "mid": v(55.94, -1.65) * mm, "end": v(56.18, -1.46) * mm});
            skArc(sketch, "E8.44.4", {"start": v(56.18, -1.46) * mm, "mid": v(56.3, -1.41) * mm, "end": v(56.44, -1.38) * mm});
            skArc(sketch, "E8.44.5", {"start": v(56.44, -1.38) * mm, "mid": v(56.56, -1.32) * mm, "end": v(56.61, -1.19) * mm});
            skArc(sketch, "E8.45.0", {"start": v(56.45, -0.59) * mm, "mid": v(56.57, -0.66) * mm, "end": v(56.62, -0.79) * mm});
            skArc(sketch, "E8.45.1", {"start": v(56.2, -0.5) * mm, "mid": v(56.32, -0.56) * mm, "end": v(56.45, -0.59) * mm});
            skArc(sketch, "E8.45.2", {"start": v(55.88, 0) * mm, "mid": v(55.96, -0.3) * mm, "end": v(56.2, -0.5) * mm});
            skArc(sketch, "E8.45.3", {"start": v(55.88, 0) * mm, "mid": v(55.96, 0.3) * mm, "end": v(56.2, 0.5) * mm});
            skArc(sketch, "E8.45.4", {"start": v(56.2, 0.5) * mm, "mid": v(56.32, 0.56) * mm, "end": v(56.45, 0.59) * mm});
            skArc(sketch, "E8.45.5", {"start": v(56.45, 0.59) * mm, "mid": v(56.57, 0.66) * mm, "end": v(56.62, 0.79) * mm});
            skArc(sketch, "E8.46.0", {"start": v(56.44, 1.38) * mm, "mid": v(56.56, 1.32) * mm, "end": v(56.61, 1.19) * mm});
            skArc(sketch, "E8.46.1", {"start": v(56.18, 1.46) * mm, "mid": v(56.3, 1.41) * mm, "end": v(56.44, 1.38) * mm});
            skArc(sketch, "E8.46.2", {"start": v(55.84, 1.95) * mm, "mid": v(55.94, 1.65) * mm, "end": v(56.18, 1.46) * mm});
            skArc(sketch, "E8.46.3", {"start": v(55.84, 1.95) * mm, "mid": v(55.92, 2.25) * mm, "end": v(56.15, 2.47) * mm});
            skArc(sketch, "E8.46.4", {"start": v(56.15, 2.47) * mm, "mid": v(56.27, 2.52) * mm, "end": v(56.4, 2.56) * mm});
            skArc(sketch, "E8.46.5", {"start": v(56.4, 2.56) * mm, "mid": v(56.52, 2.63) * mm, "end": v(56.56, 2.76) * mm});
            skArc(sketch, "E8.47.0", {"start": v(56.36, 3.35) * mm, "mid": v(56.48, 3.3) * mm, "end": v(56.54, 3.16) * mm});
            skArc(sketch, "E8.47.1", {"start": v(56.1, 3.41) * mm, "mid": v(56.22, 3.37) * mm, "end": v(56.36, 3.35) * mm});
            skArc(sketch, "E8.47.2", {"start": v(55.74, 3.9) * mm, "mid": v(55.85, 3.6) * mm, "end": v(56.1, 3.41) * mm});
            skArc(sketch, "E8.47.3", {"start": v(55.74, 3.9) * mm, "mid": v(55.8, 4.2) * mm, "end": v(56.02, 4.43) * mm});
            skArc(sketch, "E8.47.4", {"start": v(56.02, 4.43) * mm, "mid": v(56.15, 4.48) * mm, "end": v(56.28, 4.52) * mm});
            skArc(sketch, "E8.47.5", {"start": v(56.28, 4.52) * mm, "mid": v(56.4, 4.6) * mm, "end": v(56.43, 4.74) * mm});
            skArc(sketch, "E8.48.0", {"start": v(56.2, 5.32) * mm, "mid": v(56.33, 5.26) * mm, "end": v(56.4, 5.14) * mm});
            skArc(sketch, "E8.48.1", {"start": v(55.94, 5.37) * mm, "mid": v(56.07, 5.33) * mm, "end": v(56.2, 5.32) * mm});
            skArc(sketch, "E8.48.2", {"start": v(55.57, 5.84) * mm, "mid": v(55.69, 5.55) * mm, "end": v(55.94, 5.37) * mm});
            skArc(sketch, "E8.48.3", {"start": v(55.57, 5.84) * mm, "mid": v(55.62, 6.15) * mm, "end": v(55.84, 6.38) * mm});
            skArc(sketch, "E8.48.4", {"start": v(55.84, 6.38) * mm, "mid": v(55.96, 6.44) * mm, "end": v(56.08, 6.49) * mm});
            skArc(sketch, "E8.48.5", {"start": v(56.08, 6.49) * mm, "mid": v(56.2, 6.57) * mm, "end": v(56.23, 6.7) * mm});
            skArc(sketch, "E8.49.0", {"start": v(55.99, 7.27) * mm, "mid": v(56.12, 7.22) * mm, "end": v(56.18, 7.1) * mm});
            skArc(sketch, "E8.49.1", {"start": v(55.72, 7.32) * mm, "mid": v(55.85, 7.29) * mm, "end": v(55.99, 7.27) * mm});
            skArc(sketch, "E8.49.2", {"start": v(55.33, 7.78) * mm, "mid": v(55.46, 7.5) * mm, "end": v(55.72, 7.32) * mm});
            skArc(sketch, "E8.49.3", {"start": v(55.33, 7.78) * mm, "mid": v(55.38, 8.09) * mm, "end": v(55.58, 8.32) * mm});
            skArc(sketch, "E8.49.4", {"start": v(55.58, 8.32) * mm, "mid": v(55.7, 8.39) * mm, "end": v(55.82, 8.44) * mm});
            skArc(sketch, "E8.49.5", {"start": v(55.82, 8.44) * mm, "mid": v(55.93, 8.52) * mm, "end": v(55.96, 8.66) * mm});
            skArc(sketch, "E8.50.0", {"start": v(55.7, 9.22) * mm, "mid": v(55.83, 9.18) * mm, "end": v(55.9, 9.06) * mm});
            skArc(sketch, "E8.50.1", {"start": v(55.43, 9.26) * mm, "mid": v(55.56, 9.23) * mm, "end": v(55.7, 9.22) * mm});
            skArc(sketch, "E8.50.2", {"start": v(55.03, 9.7) * mm, "mid": v(55.16, 9.42) * mm, "end": v(55.43, 9.26) * mm});
            skArc(sketch, "E8.50.3", {"start": v(55.03, 9.7) * mm, "mid": v(55.06, 10.01) * mm, "end": v(55.26, 10.26) * mm});
            skArc(sketch, "E8.50.4", {"start": v(55.26, 10.26) * mm, "mid": v(55.37, 10.33) * mm, "end": v(55.5, 10.38) * mm});
            skArc(sketch, "E8.50.5", {"start": v(55.5, 10.38) * mm, "mid": v(55.6, 10.47) * mm, "end": v(55.62, 10.6) * mm});
            skArc(sketch, "E8.51.0", {"start": v(55.34, 11.16) * mm, "mid": v(55.47, 11.12) * mm, "end": v(55.55, 11) * mm});
            skArc(sketch, "E8.51.1", {"start": v(55.07, 11.19) * mm, "mid": v(55.2, 11.17) * mm, "end": v(55.34, 11.16) * mm});
            skArc(sketch, "E8.51.2", {"start": v(54.65, 11.62) * mm, "mid": v(54.8, 11.34) * mm, "end": v(55.07, 11.19) * mm});
            skArc(sketch, "E8.51.3", {"start": v(54.65, 11.62) * mm, "mid": v(54.68, 11.93) * mm, "end": v(54.86, 12.18) * mm});
            skArc(sketch, "E8.51.4", {"start": v(54.86, 12.18) * mm, "mid": v(54.98, 12.25) * mm, "end": v(55.1, 12.31) * mm});
            skArc(sketch, "E8.51.5", {"start": v(55.1, 12.31) * mm, "mid": v(55.2, 12.4) * mm, "end": v(55.22, 12.54) * mm});
            skArc(sketch, "E8.52.0", {"start": v(54.92, 13.09) * mm, "mid": v(55.05, 13.05) * mm, "end": v(55.13, 12.93) * mm});
            skArc(sketch, "E8.52.1", {"start": v(54.65, 13.1) * mm, "mid": v(54.78, 13.09) * mm, "end": v(54.92, 13.09) * mm});
            skArc(sketch, "E8.52.2", {"start": v(54.22, 13.52) * mm, "mid": v(54.37, 13.25) * mm, "end": v(54.65, 13.1) * mm});
            skArc(sketch, "E8.52.3", {"start": v(54.22, 13.52) * mm, "mid": v(54.23, 13.83) * mm, "end": v(54.4, 14.09) * mm});
            skArc(sketch, "E8.52.4", {"start": v(54.4, 14.09) * mm, "mid": v(54.52, 14.17) * mm, "end": v(54.64, 14.23) * mm});
            skArc(sketch, "E8.52.5", {"start": v(54.64, 14.23) * mm, "mid": v(54.73, 14.32) * mm, "end": v(54.75, 14.46) * mm});
            skArc(sketch, "E8.53.0", {"start": v(54.43, 15) * mm, "mid": v(54.56, 14.96) * mm, "end": v(54.64, 14.85) * mm});
            skArc(sketch, "E8.53.1", {"start": v(54.16, 15) * mm, "mid": v(54.3, 15) * mm, "end": v(54.43, 15) * mm});
            skArc(sketch, "E8.53.2", {"start": v(53.71, 15.4) * mm, "mid": v(53.88, 15.14) * mm, "end": v(54.16, 15) * mm});
            skArc(sketch, "E8.53.3", {"start": v(53.71, 15.4) * mm, "mid": v(53.71, 15.71) * mm, "end": v(53.88, 15.98) * mm});
            skArc(sketch, "E8.53.4", {"start": v(53.88, 15.98) * mm, "mid": v(53.99, 16.06) * mm, "end": v(54.1, 16.13) * mm});
            skArc(sketch, "E8.53.5", {"start": v(54.1, 16.13) * mm, "mid": v(54.2, 16.23) * mm, "end": v(54.2, 16.36) * mm});
            skArc(sketch, "E8.54.0", {"start": v(53.87, 16.89) * mm, "mid": v(54, 16.86) * mm, "end": v(54.1, 16.75) * mm});
            skArc(sketch, "E8.54.1", {"start": v(53.6, 16.88) * mm, "mid": v(53.74, 16.88) * mm, "end": v(53.87, 16.89) * mm});
            skArc(sketch, "E8.54.2", {"start": v(53.14, 17.27) * mm, "mid": v(53.32, 17) * mm, "end": v(53.6, 16.88) * mm});
            skArc(sketch, "E8.54.3", {"start": v(53.14, 17.27) * mm, "mid": v(53.13, 17.58) * mm, "end": v(53.29, 17.85) * mm});
            skArc(sketch, "E8.54.4", {"start": v(53.29, 17.85) * mm, "mid": v(53.4, 17.93) * mm, "end": v(53.5, 18) * mm});
            skArc(sketch, "E8.54.5", {"start": v(53.5, 18) * mm, "mid": v(53.6, 18.1) * mm, "end": v(53.6, 18.25) * mm});
            skArc(sketch, "E8.55.0", {"start": v(53.25, 18.76) * mm, "mid": v(53.39, 18.73) * mm, "end": v(53.48, 18.63) * mm});
            skArc(sketch, "E8.55.1", {"start": v(52.98, 18.74) * mm, "mid": v(53.12, 18.74) * mm, "end": v(53.25, 18.76) * mm});
            skArc(sketch, "E8.55.2", {"start": v(52.5, 19.11) * mm, "mid": v(52.7, 18.86) * mm, "end": v(52.98, 18.74) * mm});
            skArc(sketch, "E8.55.3", {"start": v(52.5, 19.11) * mm, "mid": v(52.49, 19.42) * mm, "end": v(52.63, 19.7) * mm});
            skArc(sketch, "E8.55.4", {"start": v(52.63, 19.7) * mm, "mid": v(52.74, 19.79) * mm, "end": v(52.85, 19.86) * mm});
            skArc(sketch, "E8.55.5", {"start": v(52.85, 19.86) * mm, "mid": v(52.94, 19.97) * mm, "end": v(52.94, 20.1) * mm});
            skArc(sketch, "E8.56.0", {"start": v(52.56, 20.6) * mm, "mid": v(52.7, 20.58) * mm, "end": v(52.8, 20.48) * mm});
            skArc(sketch, "E8.56.1", {"start": v(52.3, 20.58) * mm, "mid": v(52.43, 20.58) * mm, "end": v(52.56, 20.6) * mm});
            skArc(sketch, "E8.56.2", {"start": v(51.8, 20.93) * mm, "mid": v(52, 20.69) * mm, "end": v(52.3, 20.58) * mm});
            skArc(sketch, "E8.56.3", {"start": v(51.8, 20.93) * mm, "mid": v(51.78, 21.24) * mm, "end": v(51.92, 21.52) * mm});
            skArc(sketch, "E8.56.4", {"start": v(51.92, 21.52) * mm, "mid": v(52.01, 21.61) * mm, "end": v(52.12, 21.7) * mm});
            skArc(sketch, "E8.56.5", {"start": v(52.12, 21.7) * mm, "mid": v(52.2, 21.8) * mm, "end": v(52.2, 21.94) * mm});
            skArc(sketch, "E8.57.0", {"start": v(51.81, 22.43) * mm, "mid": v(51.95, 22.41) * mm, "end": v(52.05, 22.31) * mm});
            skArc(sketch, "E8.57.1", {"start": v(51.54, 22.4) * mm, "mid": v(51.68, 22.4) * mm, "end": v(51.81, 22.43) * mm});
            skArc(sketch, "E8.57.2", {"start": v(51.05, 22.73) * mm, "mid": v(51.25, 22.49) * mm, "end": v(51.54, 22.4) * mm});
            skArc(sketch, "E8.57.3", {"start": v(51.05, 22.73) * mm, "mid": v(51, 23.04) * mm, "end": v(51.13, 23.32) * mm});
            skArc(sketch, "E8.57.4", {"start": v(51.13, 23.32) * mm, "mid": v(51.23, 23.42) * mm, "end": v(51.33, 23.5) * mm});
            skArc(sketch, "E8.57.5", {"start": v(51.33, 23.5) * mm, "mid": v(51.42, 23.61) * mm, "end": v(51.4, 23.75) * mm});
            skArc(sketch, "E8.58.0", {"start": v(51, 24.22) * mm, "mid": v(51.14, 24.2) * mm, "end": v(51.24, 24.11) * mm});
            skArc(sketch, "E8.58.1", {"start": v(50.73, 24.18) * mm, "mid": v(50.87, 24.2) * mm, "end": v(51, 24.22) * mm});
            skArc(sketch, "E8.58.2", {"start": v(50.22, 24.5) * mm, "mid": v(50.43, 24.26) * mm, "end": v(50.73, 24.18) * mm});
            skArc(sketch, "E8.58.3", {"start": v(50.22, 24.5) * mm, "mid": v(50.17, 24.8) * mm, "end": v(50.29, 25.1) * mm});
            skArc(sketch, "E8.58.4", {"start": v(50.29, 25.1) * mm, "mid": v(50.38, 25.19) * mm, "end": v(50.48, 25.28) * mm});
            skArc(sketch, "E8.58.5", {"start": v(50.48, 25.28) * mm, "mid": v(50.56, 25.4) * mm, "end": v(50.54, 25.53) * mm});
            skArc(sketch, "E8.59.0", {"start": v(50.12, 25.98) * mm, "mid": v(50.26, 25.98) * mm, "end": v(50.36, 25.89) * mm});
            skArc(sketch, "E8.59.1", {"start": v(49.86, 25.94) * mm, "mid": v(50, 25.95) * mm, "end": v(50.12, 25.98) * mm});
            skArc(sketch, "E8.59.2", {"start": v(49.34, 26.23) * mm, "mid": v(49.55, 26) * mm, "end": v(49.86, 25.94) * mm});
            skArc(sketch, "E8.59.3", {"start": v(49.34, 26.23) * mm, "mid": v(49.27, 26.54) * mm, "end": v(49.38, 26.83) * mm});
            skArc(sketch, "E8.59.4", {"start": v(49.38, 26.83) * mm, "mid": v(49.47, 26.93) * mm, "end": v(49.57, 27.02) * mm});
            skArc(sketch, "E8.59.5", {"start": v(49.57, 27.02) * mm, "mid": v(49.64, 27.14) * mm, "end": v(49.62, 27.28) * mm});
            skArc(sketch, "E8.60.0", {"start": v(49.18, 27.72) * mm, "mid": v(49.32, 27.72) * mm, "end": v(49.43, 27.63) * mm});
            skArc(sketch, "E8.60.1", {"start": v(48.92, 27.66) * mm, "mid": v(49.05, 27.68) * mm, "end": v(49.18, 27.72) * mm});
            skArc(sketch, "E8.60.2", {"start": v(48.39, 27.94) * mm, "mid": v(48.62, 27.72) * mm, "end": v(48.92, 27.66) * mm});
            skArc(sketch, "E8.60.3", {"start": v(48.39, 27.94) * mm, "mid": v(48.32, 28.24) * mm, "end": v(48.41, 28.54) * mm});
            skArc(sketch, "E8.60.4", {"start": v(48.41, 28.54) * mm, "mid": v(48.5, 28.64) * mm, "end": v(48.6, 28.74) * mm});
            skArc(sketch, "E8.60.5", {"start": v(48.6, 28.74) * mm, "mid": v(48.67, 28.86) * mm, "end": v(48.64, 29) * mm});
            skArc(sketch, "E8.61.0", {"start": v(48.19, 29.42) * mm, "mid": v(48.33, 29.42) * mm, "end": v(48.43, 29.34) * mm});
            skArc(sketch, "E8.61.1", {"start": v(47.93, 29.35) * mm, "mid": v(48.06, 29.38) * mm, "end": v(48.19, 29.42) * mm});
            skArc(sketch, "E8.61.2", {"start": v(47.39, 29.6) * mm, "mid": v(47.62, 29.4) * mm, "end": v(47.93, 29.35) * mm});
            skArc(sketch, "E8.61.3", {"start": v(47.39, 29.6) * mm, "mid": v(47.3, 29.91) * mm, "end": v(47.39, 30.2) * mm});
            skArc(sketch, "E8.61.4", {"start": v(47.39, 30.2) * mm, "mid": v(47.47, 30.32) * mm, "end": v(47.56, 30.41) * mm});
            skArc(sketch, "E8.61.5", {"start": v(47.56, 30.41) * mm, "mid": v(47.63, 30.54) * mm, "end": v(47.6, 30.67) * mm});
            skArc(sketch, "E8.62.0", {"start": v(47.13, 31.08) * mm, "mid": v(47.27, 31.1) * mm, "end": v(47.38, 31) * mm});
            skArc(sketch, "E8.62.1", {"start": v(46.87, 31) * mm, "mid": v(47, 31.03) * mm, "end": v(47.13, 31.08) * mm});
            skArc(sketch, "E8.62.2", {"start": v(46.32, 31.25) * mm, "mid": v(46.56, 31.05) * mm, "end": v(46.87, 31) * mm});
            skArc(sketch, "E8.62.3", {"start": v(46.32, 31.25) * mm, "mid": v(46.23, 31.54) * mm, "end": v(46.3, 31.84) * mm});
            skArc(sketch, "E8.62.4", {"start": v(46.3, 31.84) * mm, "mid": v(46.38, 31.96) * mm, "end": v(46.47, 32.06) * mm});
            skArc(sketch, "E8.62.5", {"start": v(46.47, 32.06) * mm, "mid": v(46.53, 32.18) * mm, "end": v(46.5, 32.31) * mm});
            skArc(sketch, "E8.63.0", {"start": v(46.02, 32.7) * mm, "mid": v(46.16, 32.72) * mm, "end": v(46.27, 32.64) * mm});
            skArc(sketch, "E8.63.1", {"start": v(45.76, 32.62) * mm, "mid": v(45.9, 32.66) * mm, "end": v(46.02, 32.7) * mm});
            skArc(sketch, "E8.63.2", {"start": v(45.2, 32.84) * mm, "mid": v(45.45, 32.65) * mm, "end": v(45.76, 32.62) * mm});
            skArc(sketch, "E8.63.3", {"start": v(45.2, 32.84) * mm, "mid": v(45.1, 33.14) * mm, "end": v(45.17, 33.44) * mm});
            skArc(sketch, "E8.63.4", {"start": v(45.17, 33.44) * mm, "mid": v(45.24, 33.56) * mm, "end": v(45.33, 33.66) * mm});
            skArc(sketch, "E8.63.5", {"start": v(45.33, 33.66) * mm, "mid": v(45.38, 33.78) * mm, "end": v(45.34, 33.92) * mm});
            skArc(sketch, "E8.64.0", {"start": v(44.85, 34.3) * mm, "mid": v(44.99, 34.31) * mm, "end": v(45.1, 34.24) * mm});
            skArc(sketch, "E8.64.1", {"start": v(44.6, 34.2) * mm, "mid": v(44.73, 34.24) * mm, "end": v(44.85, 34.3) * mm});
            skArc(sketch, "E8.64.2", {"start": v(44.03, 34.4) * mm, "mid": v(44.28, 34.22) * mm, "end": v(44.6, 34.2) * mm});
            skArc(sketch, "E8.64.3", {"start": v(44.03, 34.4) * mm, "mid": v(43.91, 34.7) * mm, "end": v(43.97, 35) * mm});
            skArc(sketch, "E8.64.4", {"start": v(43.97, 35) * mm, "mid": v(44.04, 35.11) * mm, "end": v(44.12, 35.22) * mm});
            skArc(sketch, "E8.64.5", {"start": v(44.12, 35.22) * mm, "mid": v(44.18, 35.35) * mm, "end": v(44.13, 35.48) * mm});
            skArc(sketch, "E8.65.0", {"start": v(43.62, 35.84) * mm, "mid": v(43.76, 35.86) * mm, "end": v(43.88, 35.8) * mm});
            skArc(sketch, "E8.65.1", {"start": v(43.37, 35.73) * mm, "mid": v(43.5, 35.78) * mm, "end": v(43.62, 35.84) * mm});
            skArc(sketch, "E8.65.2", {"start": v(42.8, 35.92) * mm, "mid": v(43.06, 35.74) * mm, "end": v(43.37, 35.73) * mm});
            skArc(sketch, "E8.65.3", {"start": v(42.8, 35.92) * mm, "mid": v(42.68, 36.2) * mm, "end": v(42.72, 36.51) * mm});
            skArc(sketch, "E8.65.4", {"start": v(42.72, 36.51) * mm, "mid": v(42.79, 36.63) * mm, "end": v(42.87, 36.74) * mm});
            skArc(sketch, "E8.65.5", {"start": v(42.87, 36.74) * mm, "mid": v(42.92, 36.87) * mm, "end": v(42.87, 37) * mm});
            skArc(sketch, "E8.66.0", {"start": v(42.35, 37.34) * mm, "mid": v(42.48, 37.37) * mm, "end": v(42.6, 37.3) * mm});
            skArc(sketch, "E8.66.1", {"start": v(42.1, 37.23) * mm, "mid": v(42.23, 37.27) * mm, "end": v(42.35, 37.34) * mm});
            skArc(sketch, "E8.66.2", {"start": v(41.52, 37.39) * mm, "mid": v(41.79, 37.22) * mm, "end": v(42.1, 37.23) * mm});
            skArc(sketch, "E8.66.3", {"start": v(41.52, 37.39) * mm, "mid": v(41.39, 37.67) * mm, "end": v(41.42, 37.98) * mm});
            skArc(sketch, "E8.66.4", {"start": v(41.42, 37.98) * mm, "mid": v(41.48, 38.1) * mm, "end": v(41.56, 38.21) * mm});
            skArc(sketch, "E8.66.5", {"start": v(41.56, 38.21) * mm, "mid": v(41.6, 38.34) * mm, "end": v(41.55, 38.47) * mm});
            skArc(sketch, "E8.67.0", {"start": v(41.02, 38.8) * mm, "mid": v(41.15, 38.83) * mm, "end": v(41.28, 38.77) * mm});
            skArc(sketch, "E8.67.1", {"start": v(40.78, 38.67) * mm, "mid": v(40.9, 38.73) * mm, "end": v(41.02, 38.8) * mm});
            skArc(sketch, "E8.67.2", {"start": v(40.2, 38.81) * mm, "mid": v(40.46, 38.66) * mm, "end": v(40.78, 38.67) * mm});
            skArc(sketch, "E8.67.3", {"start": v(40.2, 38.81) * mm, "mid": v(40.05, 39.1) * mm, "end": v(40.07, 39.4) * mm});
            skArc(sketch, "E8.67.4", {"start": v(40.07, 39.4) * mm, "mid": v(40.13, 39.52) * mm, "end": v(40.2, 39.64) * mm});
            skArc(sketch, "E8.67.5", {"start": v(40.2, 39.64) * mm, "mid": v(40.24, 39.77) * mm, "end": v(40.18, 39.9) * mm});
            skArc(sketch, "E8.68.0", {"start": v(39.64, 40.2) * mm, "mid": v(39.77, 40.24) * mm, "end": v(39.9, 40.18) * mm});
            skArc(sketch, "E8.68.1", {"start": v(39.4, 40.07) * mm, "mid": v(39.52, 40.13) * mm, "end": v(39.64, 40.2) * mm});
            skArc(sketch, "E8.68.2", {"start": v(38.81, 40.2) * mm, "mid": v(39.1, 40.05) * mm, "end": v(39.4, 40.07) * mm});
            skArc(sketch, "E8.68.3", {"start": v(38.81, 40.2) * mm, "mid": v(38.66, 40.46) * mm, "end": v(38.67, 40.78) * mm});
            skArc(sketch, "E8.68.4", {"start": v(38.67, 40.78) * mm, "mid": v(38.73, 40.9) * mm, "end": v(38.8, 41.02) * mm});
            skArc(sketch, "E8.68.5", {"start": v(38.8, 41.02) * mm, "mid": v(38.83, 41.15) * mm, "end": v(38.77, 41.28) * mm});
            skArc(sketch, "E8.69.0", {"start": v(38.21, 41.56) * mm, "mid": v(38.34, 41.6) * mm, "end": v(38.47, 41.55) * mm});
            skArc(sketch, "E8.69.1", {"start": v(37.98, 41.42) * mm, "mid": v(38.1, 41.48) * mm, "end": v(38.21, 41.56) * mm});
            skArc(sketch, "E8.69.2", {"start": v(37.39, 41.52) * mm, "mid": v(37.67, 41.39) * mm, "end": v(37.98, 41.42) * mm});
            skArc(sketch, "E8.69.3", {"start": v(37.39, 41.52) * mm, "mid": v(37.22, 41.79) * mm, "end": v(37.23, 42.1) * mm});
            skArc(sketch, "E8.69.4", {"start": v(37.23, 42.1) * mm, "mid": v(37.27, 42.23) * mm, "end": v(37.34, 42.35) * mm});
            skArc(sketch, "E8.69.5", {"start": v(37.34, 42.35) * mm, "mid": v(37.37, 42.48) * mm, "end": v(37.3, 42.6) * mm});
            skArc(sketch, "E8.70.0", {"start": v(36.74, 42.87) * mm, "mid": v(36.87, 42.92) * mm, "end": v(37, 42.87) * mm});
            skArc(sketch, "E8.70.1", {"start": v(36.51, 42.72) * mm, "mid": v(36.63, 42.79) * mm, "end": v(36.74, 42.87) * mm});
            skArc(sketch, "E8.70.2", {"start": v(35.92, 42.8) * mm, "mid": v(36.2, 42.68) * mm, "end": v(36.51, 42.72) * mm});
            skArc(sketch, "E8.70.3", {"start": v(35.92, 42.8) * mm, "mid": v(35.74, 43.06) * mm, "end": v(35.73, 43.37) * mm});
            skArc(sketch, "E8.70.4", {"start": v(35.73, 43.37) * mm, "mid": v(35.78, 43.5) * mm, "end": v(35.84, 43.62) * mm});
            skArc(sketch, "E8.70.5", {"start": v(35.84, 43.62) * mm, "mid": v(35.86, 43.76) * mm, "end": v(35.8, 43.88) * mm});
            skArc(sketch, "E8.71.0", {"start": v(35.22, 44.12) * mm, "mid": v(35.35, 44.18) * mm, "end": v(35.48, 44.13) * mm});
            skArc(sketch, "E8.71.1", {"start": v(35, 43.97) * mm, "mid": v(35.11, 44.04) * mm, "end": v(35.22, 44.12) * mm});
            skArc(sketch, "E8.71.2", {"start": v(34.4, 44.03) * mm, "mid": v(34.7, 43.91) * mm, "end": v(35, 43.97) * mm});
            skArc(sketch, "E8.71.3", {"start": v(34.4, 44.03) * mm, "mid": v(34.22, 44.28) * mm, "end": v(34.2, 44.6) * mm});
            skArc(sketch, "E8.71.4", {"start": v(34.2, 44.6) * mm, "mid": v(34.24, 44.73) * mm, "end": v(34.3, 44.85) * mm});
            skArc(sketch, "E8.71.5", {"start": v(34.3, 44.85) * mm, "mid": v(34.31, 44.99) * mm, "end": v(34.24, 45.1) * mm});
            skArc(sketch, "E8.72.0", {"start": v(33.66, 45.33) * mm, "mid": v(33.78, 45.38) * mm, "end": v(33.92, 45.34) * mm});
            skArc(sketch, "E8.72.1", {"start": v(33.44, 45.17) * mm, "mid": v(33.56, 45.24) * mm, "end": v(33.66, 45.33) * mm});
            skArc(sketch, "E8.72.2", {"start": v(32.84, 45.2) * mm, "mid": v(33.14, 45.1) * mm, "end": v(33.44, 45.17) * mm});
            skArc(sketch, "E8.72.3", {"start": v(32.84, 45.2) * mm, "mid": v(32.65, 45.45) * mm, "end": v(32.62, 45.76) * mm});
            skArc(sketch, "E8.72.4", {"start": v(32.62, 45.76) * mm, "mid": v(32.66, 45.9) * mm, "end": v(32.7, 46.02) * mm});
            skArc(sketch, "E8.72.5", {"start": v(32.7, 46.02) * mm, "mid": v(32.72, 46.16) * mm, "end": v(32.64, 46.27) * mm});
            skArc(sketch, "E8.73.0", {"start": v(32.06, 46.47) * mm, "mid": v(32.18, 46.53) * mm, "end": v(32.31, 46.5) * mm});
            skArc(sketch, "E8.73.1", {"start": v(31.84, 46.3) * mm, "mid": v(31.96, 46.38) * mm, "end": v(32.06, 46.47) * mm});
            skArc(sketch, "E8.73.2", {"start": v(31.25, 46.32) * mm, "mid": v(31.54, 46.23) * mm, "end": v(31.84, 46.3) * mm});
            skArc(sketch, "E8.73.3", {"start": v(31.25, 46.32) * mm, "mid": v(31.05, 46.56) * mm, "end": v(31, 46.87) * mm});
            skArc(sketch, "E8.73.4", {"start": v(31, 46.87) * mm, "mid": v(31.03, 47) * mm, "end": v(31.08, 47.13) * mm});
            skArc(sketch, "E8.73.5", {"start": v(31.08, 47.13) * mm, "mid": v(31.1, 47.27) * mm, "end": v(31, 47.38) * mm});
            skArc(sketch, "E8.74.0", {"start": v(30.41, 47.56) * mm, "mid": v(30.54, 47.63) * mm, "end": v(30.67, 47.6) * mm});
            skArc(sketch, "E8.74.1", {"start": v(30.2, 47.39) * mm, "mid": v(30.32, 47.47) * mm, "end": v(30.41, 47.56) * mm});
            skArc(sketch, "E8.74.2", {"start": v(29.6, 47.39) * mm, "mid": v(29.91, 47.3) * mm, "end": v(30.2, 47.39) * mm});
            skArc(sketch, "E8.74.3", {"start": v(29.6, 47.39) * mm, "mid": v(29.4, 47.62) * mm, "end": v(29.35, 47.93) * mm});
            skArc(sketch, "E8.74.4", {"start": v(29.35, 47.93) * mm, "mid": v(29.38, 48.06) * mm, "end": v(29.42, 48.19) * mm});
            skArc(sketch, "E8.74.5", {"start": v(29.42, 48.19) * mm, "mid": v(29.42, 48.33) * mm, "end": v(29.34, 48.43) * mm});
            skArc(sketch, "E8.75.0", {"start": v(28.74, 48.6) * mm, "mid": v(28.86, 48.67) * mm, "end": v(29, 48.64) * mm});
            skArc(sketch, "E8.75.1", {"start": v(28.54, 48.41) * mm, "mid": v(28.64, 48.5) * mm, "end": v(28.74, 48.6) * mm});
            skArc(sketch, "E8.75.2", {"start": v(27.94, 48.39) * mm, "mid": v(28.24, 48.32) * mm, "end": v(28.54, 48.41) * mm});
            skArc(sketch, "E8.75.3", {"start": v(27.94, 48.39) * mm, "mid": v(27.72, 48.62) * mm, "end": v(27.66, 48.92) * mm});
            skArc(sketch, "E8.75.4", {"start": v(27.66, 48.92) * mm, "mid": v(27.68, 49.05) * mm, "end": v(27.72, 49.18) * mm});
            skArc(sketch, "E8.75.5", {"start": v(27.72, 49.18) * mm, "mid": v(27.72, 49.32) * mm, "end": v(27.63, 49.43) * mm});
            skArc(sketch, "E8.76.0", {"start": v(27.02, 49.57) * mm, "mid": v(27.14, 49.64) * mm, "end": v(27.28, 49.62) * mm});
            skArc(sketch, "E8.76.1", {"start": v(26.83, 49.38) * mm, "mid": v(26.93, 49.47) * mm, "end": v(27.02, 49.57) * mm});
            skArc(sketch, "E8.76.2", {"start": v(26.23, 49.34) * mm, "mid": v(26.54, 49.27) * mm, "end": v(26.83, 49.38) * mm});
            skArc(sketch, "E8.76.3", {"start": v(26.23, 49.34) * mm, "mid": v(26, 49.55) * mm, "end": v(25.94, 49.86) * mm});
            skArc(sketch, "E8.76.4", {"start": v(25.94, 49.86) * mm, "mid": v(25.95, 50) * mm, "end": v(25.98, 50.12) * mm});
            skArc(sketch, "E8.76.5", {"start": v(25.98, 50.12) * mm, "mid": v(25.98, 50.26) * mm, "end": v(25.89, 50.36) * mm});
            skArc(sketch, "E8.77.0", {"start": v(25.28, 50.48) * mm, "mid": v(25.4, 50.56) * mm, "end": v(25.53, 50.54) * mm});
            skArc(sketch, "E8.77.1", {"start": v(25.1, 50.29) * mm, "mid": v(25.19, 50.38) * mm, "end": v(25.28, 50.48) * mm});
            skArc(sketch, "E8.77.2", {"start": v(24.5, 50.22) * mm, "mid": v(24.8, 50.17) * mm, "end": v(25.1, 50.29) * mm});
            skArc(sketch, "E8.77.3", {"start": v(24.5, 50.22) * mm, "mid": v(24.26, 50.43) * mm, "end": v(24.18, 50.73) * mm});
            skArc(sketch, "E8.77.4", {"start": v(24.18, 50.73) * mm, "mid": v(24.2, 50.87) * mm, "end": v(24.22, 51) * mm});
            skArc(sketch, "E8.77.5", {"start": v(24.22, 51) * mm, "mid": v(24.2, 51.14) * mm, "end": v(24.11, 51.24) * mm});
            skArc(sketch, "E8.78.0", {"start": v(23.5, 51.33) * mm, "mid": v(23.61, 51.42) * mm, "end": v(23.75, 51.4) * mm});
            skArc(sketch, "E8.78.1", {"start": v(23.32, 51.13) * mm, "mid": v(23.42, 51.23) * mm, "end": v(23.5, 51.33) * mm});
            skArc(sketch, "E8.78.2", {"start": v(22.73, 51.05) * mm, "mid": v(23.04, 51) * mm, "end": v(23.32, 51.13) * mm});
            skArc(sketch, "E8.78.3", {"start": v(22.73, 51.05) * mm, "mid": v(22.49, 51.25) * mm, "end": v(22.4, 51.54) * mm});
            skArc(sketch, "E8.78.4", {"start": v(22.4, 51.54) * mm, "mid": v(22.4, 51.68) * mm, "end": v(22.43, 51.81) * mm});
            skArc(sketch, "E8.78.5", {"start": v(22.43, 51.81) * mm, "mid": v(22.41, 51.95) * mm, "end": v(22.31, 52.05) * mm});
            skArc(sketch, "E8.79.0", {"start": v(21.7, 52.12) * mm, "mid": v(21.8, 52.2) * mm, "end": v(21.94, 52.2) * mm});
            skArc(sketch, "E8.79.1", {"start": v(21.52, 51.92) * mm, "mid": v(21.61, 52.01) * mm, "end": v(21.7, 52.12) * mm});
            skArc(sketch, "E8.79.2", {"start": v(20.93, 51.8) * mm, "mid": v(21.24, 51.78) * mm, "end": v(21.52, 51.92) * mm});
            skArc(sketch, "E8.79.3", {"start": v(20.93, 51.8) * mm, "mid": v(20.69, 52) * mm, "end": v(20.58, 52.3) * mm});
            skArc(sketch, "E8.79.4", {"start": v(20.58, 52.3) * mm, "mid": v(20.58, 52.43) * mm, "end": v(20.6, 52.56) * mm});
            skArc(sketch, "E8.79.5", {"start": v(20.6, 52.56) * mm, "mid": v(20.58, 52.7) * mm, "end": v(20.48, 52.8) * mm});
            skArc(sketch, "E8.80.0", {"start": v(19.86, 52.85) * mm, "mid": v(19.97, 52.94) * mm, "end": v(20.1, 52.94) * mm});
            skArc(sketch, "E8.80.1", {"start": v(19.7, 52.63) * mm, "mid": v(19.79, 52.74) * mm, "end": v(19.86, 52.85) * mm});
            skArc(sketch, "E8.80.2", {"start": v(19.11, 52.5) * mm, "mid": v(19.42, 52.49) * mm, "end": v(19.7, 52.63) * mm});
            skArc(sketch, "E8.80.3", {"start": v(19.11, 52.5) * mm, "mid": v(18.86, 52.7) * mm, "end": v(18.74, 52.98) * mm});
            skArc(sketch, "E8.80.4", {"start": v(18.74, 52.98) * mm, "mid": v(18.74, 53.12) * mm, "end": v(18.76, 53.25) * mm});
            skArc(sketch, "E8.80.5", {"start": v(18.76, 53.25) * mm, "mid": v(18.73, 53.39) * mm, "end": v(18.63, 53.48) * mm});
            skArc(sketch, "E8.81.0", {"start": v(18, 53.5) * mm, "mid": v(18.1, 53.6) * mm, "end": v(18.25, 53.6) * mm});
            skArc(sketch, "E8.81.1", {"start": v(17.85, 53.29) * mm, "mid": v(17.93, 53.4) * mm, "end": v(18, 53.5) * mm});
            skArc(sketch, "E8.81.2", {"start": v(17.27, 53.14) * mm, "mid": v(17.58, 53.13) * mm, "end": v(17.85, 53.29) * mm});
            skArc(sketch, "E8.81.3", {"start": v(17.27, 53.14) * mm, "mid": v(17, 53.32) * mm, "end": v(16.88, 53.6) * mm});
            skArc(sketch, "E8.81.4", {"start": v(16.88, 53.6) * mm, "mid": v(16.88, 53.74) * mm, "end": v(16.89, 53.87) * mm});
            skArc(sketch, "E8.81.5", {"start": v(16.89, 53.87) * mm, "mid": v(16.86, 54) * mm, "end": v(16.75, 54.1) * mm});
            skArc(sketch, "E8.82.0", {"start": v(16.13, 54.1) * mm, "mid": v(16.23, 54.2) * mm, "end": v(16.36, 54.2) * mm});
            skArc(sketch, "E8.82.1", {"start": v(15.98, 53.88) * mm, "mid": v(16.06, 53.99) * mm, "end": v(16.13, 54.1) * mm});
            skArc(sketch, "E8.82.2", {"start": v(15.4, 53.71) * mm, "mid": v(15.71, 53.71) * mm, "end": v(15.98, 53.88) * mm});
            skArc(sketch, "E8.82.3", {"start": v(15.4, 53.71) * mm, "mid": v(15.14, 53.88) * mm, "end": v(15, 54.16) * mm});
            skArc(sketch, "E8.82.4", {"start": v(15, 54.16) * mm, "mid": v(15, 54.3) * mm, "end": v(15, 54.43) * mm});
            skArc(sketch, "E8.82.5", {"start": v(15, 54.43) * mm, "mid": v(14.96, 54.56) * mm, "end": v(14.85, 54.64) * mm});
            skArc(sketch, "E8.83.0", {"start": v(14.23, 54.64) * mm, "mid": v(14.32, 54.73) * mm, "end": v(14.46, 54.75) * mm});
            skArc(sketch, "E8.83.1", {"start": v(14.09, 54.4) * mm, "mid": v(14.17, 54.52) * mm, "end": v(14.23, 54.64) * mm});
            skArc(sketch, "E8.83.2", {"start": v(13.52, 54.22) * mm, "mid": v(13.83, 54.23) * mm, "end": v(14.09, 54.4) * mm});
            skArc(sketch, "E8.83.3", {"start": v(13.52, 54.22) * mm, "mid": v(13.25, 54.37) * mm, "end": v(13.1, 54.65) * mm});
            skArc(sketch, "E8.83.4", {"start": v(13.1, 54.65) * mm, "mid": v(13.09, 54.78) * mm, "end": v(13.09, 54.92) * mm});
            skArc(sketch, "E8.83.5", {"start": v(13.09, 54.92) * mm, "mid": v(13.05, 55.05) * mm, "end": v(12.93, 55.13) * mm});
            skArc(sketch, "E8.84.0", {"start": v(12.31, 55.1) * mm, "mid": v(12.4, 55.2) * mm, "end": v(12.54, 55.22) * mm});
            skArc(sketch, "E8.84.1", {"start": v(12.18, 54.86) * mm, "mid": v(12.25, 54.98) * mm, "end": v(12.31, 55.1) * mm});
            skArc(sketch, "E8.84.2", {"start": v(11.62, 54.65) * mm, "mid": v(11.93, 54.68) * mm, "end": v(12.18, 54.86) * mm});
            skArc(sketch, "E8.84.3", {"start": v(11.62, 54.65) * mm, "mid": v(11.34, 54.8) * mm, "end": v(11.19, 55.07) * mm});
            skArc(sketch, "E8.84.4", {"start": v(11.19, 55.07) * mm, "mid": v(11.17, 55.2) * mm, "end": v(11.16, 55.34) * mm});
            skArc(sketch, "E8.84.5", {"start": v(11.16, 55.34) * mm, "mid": v(11.12, 55.47) * mm, "end": v(11, 55.55) * mm});
            skArc(sketch, "E8.85.0", {"start": v(10.38, 55.5) * mm, "mid": v(10.47, 55.6) * mm, "end": v(10.6, 55.62) * mm});
            skArc(sketch, "E8.85.1", {"start": v(10.26, 55.26) * mm, "mid": v(10.33, 55.37) * mm, "end": v(10.38, 55.5) * mm});
            skArc(sketch, "E8.85.2", {"start": v(9.7, 55.03) * mm, "mid": v(10.01, 55.06) * mm, "end": v(10.26, 55.26) * mm});
            skArc(sketch, "E8.85.3", {"start": v(9.7, 55.03) * mm, "mid": v(9.42, 55.16) * mm, "end": v(9.26, 55.43) * mm});
            skArc(sketch, "E8.85.4", {"start": v(9.26, 55.43) * mm, "mid": v(9.23, 55.56) * mm, "end": v(9.22, 55.7) * mm});
            skArc(sketch, "E8.85.5", {"start": v(9.22, 55.7) * mm, "mid": v(9.18, 55.83) * mm, "end": v(9.06, 55.9) * mm});
            skArc(sketch, "E8.86.0", {"start": v(8.44, 55.82) * mm, "mid": v(8.52, 55.93) * mm, "end": v(8.66, 55.96) * mm});
            skArc(sketch, "E8.86.1", {"start": v(8.32, 55.58) * mm, "mid": v(8.39, 55.7) * mm, "end": v(8.44, 55.82) * mm});
            skArc(sketch, "E8.86.2", {"start": v(7.78, 55.33) * mm, "mid": v(8.09, 55.38) * mm, "end": v(8.32, 55.58) * mm});
            skArc(sketch, "E8.86.3", {"start": v(7.78, 55.33) * mm, "mid": v(7.5, 55.46) * mm, "end": v(7.32, 55.72) * mm});
            skArc(sketch, "E8.86.4", {"start": v(7.32, 55.72) * mm, "mid": v(7.29, 55.85) * mm, "end": v(7.27, 55.99) * mm});
            skArc(sketch, "E8.86.5", {"start": v(7.27, 55.99) * mm, "mid": v(7.22, 56.12) * mm, "end": v(7.1, 56.18) * mm});
            skArc(sketch, "E8.87.0", {"start": v(6.49, 56.08) * mm, "mid": v(6.57, 56.2) * mm, "end": v(6.7, 56.23) * mm});
            skArc(sketch, "E8.87.1", {"start": v(6.38, 55.84) * mm, "mid": v(6.44, 55.96) * mm, "end": v(6.49, 56.08) * mm});
            skArc(sketch, "E8.87.2", {"start": v(5.84, 55.57) * mm, "mid": v(6.15, 55.62) * mm, "end": v(6.38, 55.84) * mm});
            skArc(sketch, "E8.87.3", {"start": v(5.84, 55.57) * mm, "mid": v(5.55, 55.69) * mm, "end": v(5.37, 55.94) * mm});
            skArc(sketch, "E8.87.4", {"start": v(5.37, 55.94) * mm, "mid": v(5.33, 56.07) * mm, "end": v(5.32, 56.2) * mm});
            skArc(sketch, "E8.87.5", {"start": v(5.32, 56.2) * mm, "mid": v(5.26, 56.33) * mm, "end": v(5.14, 56.4) * mm});
            skArc(sketch, "E8.88.0", {"start": v(4.52, 56.28) * mm, "mid": v(4.6, 56.4) * mm, "end": v(4.74, 56.43) * mm});
            skArc(sketch, "E8.88.1", {"start": v(4.43, 56.02) * mm, "mid": v(4.48, 56.15) * mm, "end": v(4.52, 56.28) * mm});
            skArc(sketch, "E8.88.2", {"start": v(3.9, 55.74) * mm, "mid": v(4.2, 55.8) * mm, "end": v(4.43, 56.02) * mm});
            skArc(sketch, "E8.88.3", {"start": v(3.9, 55.74) * mm, "mid": v(3.6, 55.85) * mm, "end": v(3.41, 56.1) * mm});
            skArc(sketch, "E8.88.4", {"start": v(3.41, 56.1) * mm, "mid": v(3.37, 56.22) * mm, "end": v(3.35, 56.36) * mm});
            skArc(sketch, "E8.88.5", {"start": v(3.35, 56.36) * mm, "mid": v(3.3, 56.48) * mm, "end": v(3.16, 56.54) * mm});
            skArc(sketch, "E8.89.0", {"start": v(2.56, 56.4) * mm, "mid": v(2.63, 56.52) * mm, "end": v(2.76, 56.56) * mm});
            skArc(sketch, "E8.89.1", {"start": v(2.47, 56.15) * mm, "mid": v(2.52, 56.27) * mm, "end": v(2.56, 56.4) * mm});
            skArc(sketch, "E8.89.2", {"start": v(1.95, 55.84) * mm, "mid": v(2.25, 55.92) * mm, "end": v(2.47, 56.15) * mm});
            skArc(sketch, "E8.89.3", {"start": v(1.95, 55.84) * mm, "mid": v(1.65, 55.94) * mm, "end": v(1.46, 56.18) * mm});
            skArc(sketch, "E8.89.4", {"start": v(1.46, 56.18) * mm, "mid": v(1.41, 56.3) * mm, "end": v(1.38, 56.44) * mm});
            skArc(sketch, "E8.89.5", {"start": v(1.38, 56.44) * mm, "mid": v(1.32, 56.56) * mm, "end": v(1.19, 56.61) * mm});
            skArc(sketch, "E8.90.0", {"start": v(0.59, 56.45) * mm, "mid": v(0.66, 56.57) * mm, "end": v(0.79, 56.62) * mm});
            skArc(sketch, "E8.90.1", {"start": v(0.5, 56.2) * mm, "mid": v(0.56, 56.32) * mm, "end": v(0.59, 56.45) * mm});
            skArc(sketch, "E8.90.2", {"start": v(0, 55.88) * mm, "mid": v(0.3, 55.96) * mm, "end": v(0.5, 56.2) * mm});
            skArc(sketch, "E8.90.3", {"start": v(0, 55.88) * mm, "mid": v(-0.3, 55.96) * mm, "end": v(-0.5, 56.2) * mm});
            skArc(sketch, "E8.90.4", {"start": v(-0.5, 56.2) * mm, "mid": v(-0.56, 56.32) * mm, "end": v(-0.59, 56.45) * mm});
            skArc(sketch, "E8.90.5", {"start": v(-0.59, 56.45) * mm, "mid": v(-0.66, 56.57) * mm, "end": v(-0.79, 56.62) * mm});
            skArc(sketch, "E8.91.0", {"start": v(-1.38, 56.44) * mm, "mid": v(-1.32, 56.56) * mm, "end": v(-1.19, 56.61) * mm});
            skArc(sketch, "E8.91.1", {"start": v(-1.46, 56.18) * mm, "mid": v(-1.41, 56.3) * mm, "end": v(-1.38, 56.44) * mm});
            skArc(sketch, "E8.91.2", {"start": v(-1.95, 55.84) * mm, "mid": v(-1.65, 55.94) * mm, "end": v(-1.46, 56.18) * mm});
            skArc(sketch, "E8.91.3", {"start": v(-1.95, 55.84) * mm, "mid": v(-2.25, 55.92) * mm, "end": v(-2.47, 56.15) * mm});
            skArc(sketch, "E8.91.4", {"start": v(-2.47, 56.15) * mm, "mid": v(-2.52, 56.27) * mm, "end": v(-2.56, 56.4) * mm});
            skArc(sketch, "E8.91.5", {"start": v(-2.56, 56.4) * mm, "mid": v(-2.63, 56.52) * mm, "end": v(-2.76, 56.56) * mm});
            skArc(sketch, "E8.92.0", {"start": v(-3.35, 56.36) * mm, "mid": v(-3.3, 56.48) * mm, "end": v(-3.16, 56.54) * mm});
            skArc(sketch, "E8.92.1", {"start": v(-3.41, 56.1) * mm, "mid": v(-3.37, 56.22) * mm, "end": v(-3.35, 56.36) * mm});
            skArc(sketch, "E8.92.2", {"start": v(-3.9, 55.74) * mm, "mid": v(-3.6, 55.85) * mm, "end": v(-3.41, 56.1) * mm});
            skArc(sketch, "E8.92.3", {"start": v(-3.9, 55.74) * mm, "mid": v(-4.2, 55.8) * mm, "end": v(-4.43, 56.02) * mm});
            skArc(sketch, "E8.92.4", {"start": v(-4.43, 56.02) * mm, "mid": v(-4.48, 56.15) * mm, "end": v(-4.52, 56.28) * mm});
            skArc(sketch, "E8.92.5", {"start": v(-4.52, 56.28) * mm, "mid": v(-4.6, 56.4) * mm, "end": v(-4.74, 56.43) * mm});
            skArc(sketch, "E8.93.0", {"start": v(-5.32, 56.2) * mm, "mid": v(-5.26, 56.33) * mm, "end": v(-5.14, 56.4) * mm});
            skArc(sketch, "E8.93.1", {"start": v(-5.37, 55.94) * mm, "mid": v(-5.33, 56.07) * mm, "end": v(-5.32, 56.2) * mm});
            skArc(sketch, "E8.93.2", {"start": v(-5.84, 55.57) * mm, "mid": v(-5.55, 55.69) * mm, "end": v(-5.37, 55.94) * mm});
            skArc(sketch, "E8.93.3", {"start": v(-5.84, 55.57) * mm, "mid": v(-6.15, 55.62) * mm, "end": v(-6.38, 55.84) * mm});
            skArc(sketch, "E8.93.4", {"start": v(-6.38, 55.84) * mm, "mid": v(-6.44, 55.96) * mm, "end": v(-6.49, 56.08) * mm});
            skArc(sketch, "E8.93.5", {"start": v(-6.49, 56.08) * mm, "mid": v(-6.57, 56.2) * mm, "end": v(-6.7, 56.23) * mm});
            skArc(sketch, "E8.94.0", {"start": v(-7.27, 55.99) * mm, "mid": v(-7.22, 56.12) * mm, "end": v(-7.1, 56.18) * mm});
            skArc(sketch, "E8.94.1", {"start": v(-7.32, 55.72) * mm, "mid": v(-7.29, 55.85) * mm, "end": v(-7.27, 55.99) * mm});
            skArc(sketch, "E8.94.2", {"start": v(-7.78, 55.33) * mm, "mid": v(-7.5, 55.46) * mm, "end": v(-7.32, 55.72) * mm});
            skArc(sketch, "E8.94.3", {"start": v(-7.78, 55.33) * mm, "mid": v(-8.09, 55.38) * mm, "end": v(-8.32, 55.58) * mm});
            skArc(sketch, "E8.94.4", {"start": v(-8.32, 55.58) * mm, "mid": v(-8.39, 55.7) * mm, "end": v(-8.44, 55.82) * mm});
            skArc(sketch, "E8.94.5", {"start": v(-8.44, 55.82) * mm, "mid": v(-8.52, 55.93) * mm, "end": v(-8.66, 55.96) * mm});
            skArc(sketch, "E8.95.0", {"start": v(-9.22, 55.7) * mm, "mid": v(-9.18, 55.83) * mm, "end": v(-9.06, 55.9) * mm});
            skArc(sketch, "E8.95.1", {"start": v(-9.26, 55.43) * mm, "mid": v(-9.23, 55.56) * mm, "end": v(-9.22, 55.7) * mm});
            skArc(sketch, "E8.95.2", {"start": v(-9.7, 55.03) * mm, "mid": v(-9.42, 55.16) * mm, "end": v(-9.26, 55.43) * mm});
            skArc(sketch, "E8.95.3", {"start": v(-9.7, 55.03) * mm, "mid": v(-10.01, 55.06) * mm, "end": v(-10.26, 55.26) * mm});
            skArc(sketch, "E8.95.4", {"start": v(-10.26, 55.26) * mm, "mid": v(-10.33, 55.37) * mm, "end": v(-10.38, 55.5) * mm});
            skArc(sketch, "E8.95.5", {"start": v(-10.38, 55.5) * mm, "mid": v(-10.47, 55.6) * mm, "end": v(-10.6, 55.62) * mm});
            skArc(sketch, "E8.96.0", {"start": v(-11.16, 55.34) * mm, "mid": v(-11.12, 55.47) * mm, "end": v(-11, 55.55) * mm});
            skArc(sketch, "E8.96.1", {"start": v(-11.19, 55.07) * mm, "mid": v(-11.17, 55.2) * mm, "end": v(-11.16, 55.34) * mm});
            skArc(sketch, "E8.96.2", {"start": v(-11.62, 54.65) * mm, "mid": v(-11.34, 54.8) * mm, "end": v(-11.19, 55.07) * mm});
            skArc(sketch, "E8.96.3", {"start": v(-11.62, 54.65) * mm, "mid": v(-11.93, 54.68) * mm, "end": v(-12.18, 54.86) * mm});
            skArc(sketch, "E8.96.4", {"start": v(-12.18, 54.86) * mm, "mid": v(-12.25, 54.98) * mm, "end": v(-12.31, 55.1) * mm});
            skArc(sketch, "E8.96.5", {"start": v(-12.31, 55.1) * mm, "mid": v(-12.4, 55.2) * mm, "end": v(-12.54, 55.22) * mm});
            skArc(sketch, "E8.97.0", {"start": v(-13.09, 54.92) * mm, "mid": v(-13.05, 55.05) * mm, "end": v(-12.93, 55.13) * mm});
            skArc(sketch, "E8.97.1", {"start": v(-13.1, 54.65) * mm, "mid": v(-13.09, 54.78) * mm, "end": v(-13.09, 54.92) * mm});
            skArc(sketch, "E8.97.2", {"start": v(-13.52, 54.22) * mm, "mid": v(-13.25, 54.37) * mm, "end": v(-13.1, 54.65) * mm});
            skArc(sketch, "E8.97.3", {"start": v(-13.52, 54.22) * mm, "mid": v(-13.83, 54.23) * mm, "end": v(-14.09, 54.4) * mm});
            skArc(sketch, "E8.97.4", {"start": v(-14.09, 54.4) * mm, "mid": v(-14.17, 54.52) * mm, "end": v(-14.23, 54.64) * mm});
            skArc(sketch, "E8.97.5", {"start": v(-14.23, 54.64) * mm, "mid": v(-14.32, 54.73) * mm, "end": v(-14.46, 54.75) * mm});
            skArc(sketch, "E8.98.0", {"start": v(-15, 54.43) * mm, "mid": v(-14.96, 54.56) * mm, "end": v(-14.85, 54.64) * mm});
            skArc(sketch, "E8.98.1", {"start": v(-15, 54.16) * mm, "mid": v(-15, 54.3) * mm, "end": v(-15, 54.43) * mm});
            skArc(sketch, "E8.98.2", {"start": v(-15.4, 53.71) * mm, "mid": v(-15.14, 53.88) * mm, "end": v(-15, 54.16) * mm});
            skArc(sketch, "E8.98.3", {"start": v(-15.4, 53.71) * mm, "mid": v(-15.71, 53.71) * mm, "end": v(-15.98, 53.88) * mm});
            skArc(sketch, "E8.98.4", {"start": v(-15.98, 53.88) * mm, "mid": v(-16.06, 53.99) * mm, "end": v(-16.13, 54.1) * mm});
            skArc(sketch, "E8.98.5", {"start": v(-16.13, 54.1) * mm, "mid": v(-16.23, 54.2) * mm, "end": v(-16.36, 54.2) * mm});
            skArc(sketch, "E8.99.0", {"start": v(-16.89, 53.87) * mm, "mid": v(-16.86, 54) * mm, "end": v(-16.75, 54.1) * mm});
            skArc(sketch, "E8.99.1", {"start": v(-16.88, 53.6) * mm, "mid": v(-16.88, 53.74) * mm, "end": v(-16.89, 53.87) * mm});
            skArc(sketch, "E8.99.2", {"start": v(-17.27, 53.14) * mm, "mid": v(-17, 53.32) * mm, "end": v(-16.88, 53.6) * mm});
            skArc(sketch, "E8.99.3", {"start": v(-17.27, 53.14) * mm, "mid": v(-17.58, 53.13) * mm, "end": v(-17.85, 53.29) * mm});
            skArc(sketch, "E8.99.4", {"start": v(-17.85, 53.29) * mm, "mid": v(-17.93, 53.4) * mm, "end": v(-18, 53.5) * mm});
            skArc(sketch, "E8.99.5", {"start": v(-18, 53.5) * mm, "mid": v(-18.1, 53.6) * mm, "end": v(-18.25, 53.6) * mm});
            skArc(sketch, "E8.100.0", {"start": v(-18.76, 53.25) * mm, "mid": v(-18.73, 53.39) * mm, "end": v(-18.63, 53.48) * mm});
            skArc(sketch, "E8.100.1", {"start": v(-18.74, 52.98) * mm, "mid": v(-18.74, 53.12) * mm, "end": v(-18.76, 53.25) * mm});
            skArc(sketch, "E8.100.2", {"start": v(-19.11, 52.5) * mm, "mid": v(-18.86, 52.7) * mm, "end": v(-18.74, 52.98) * mm});
            skArc(sketch, "E8.100.3", {"start": v(-19.11, 52.5) * mm, "mid": v(-19.42, 52.49) * mm, "end": v(-19.7, 52.63) * mm});
            skArc(sketch, "E8.100.4", {"start": v(-19.7, 52.63) * mm, "mid": v(-19.79, 52.74) * mm, "end": v(-19.86, 52.85) * mm});
            skArc(sketch, "E8.100.5", {"start": v(-19.86, 52.85) * mm, "mid": v(-19.97, 52.94) * mm, "end": v(-20.1, 52.94) * mm});
            skArc(sketch, "E8.101.0", {"start": v(-20.6, 52.56) * mm, "mid": v(-20.58, 52.7) * mm, "end": v(-20.48, 52.8) * mm});
            skArc(sketch, "E8.101.1", {"start": v(-20.58, 52.3) * mm, "mid": v(-20.58, 52.43) * mm, "end": v(-20.6, 52.56) * mm});
            skArc(sketch, "E8.101.2", {"start": v(-20.93, 51.8) * mm, "mid": v(-20.69, 52) * mm, "end": v(-20.58, 52.3) * mm});
            skArc(sketch, "E8.101.3", {"start": v(-20.93, 51.8) * mm, "mid": v(-21.24, 51.78) * mm, "end": v(-21.52, 51.92) * mm});
            skArc(sketch, "E8.101.4", {"start": v(-21.52, 51.92) * mm, "mid": v(-21.61, 52.01) * mm, "end": v(-21.7, 52.12) * mm});
            skArc(sketch, "E8.101.5", {"start": v(-21.7, 52.12) * mm, "mid": v(-21.8, 52.2) * mm, "end": v(-21.94, 52.2) * mm});
            skArc(sketch, "E8.102.0", {"start": v(-22.43, 51.81) * mm, "mid": v(-22.41, 51.95) * mm, "end": v(-22.31, 52.05) * mm});
            skArc(sketch, "E8.102.1", {"start": v(-22.4, 51.54) * mm, "mid": v(-22.4, 51.68) * mm, "end": v(-22.43, 51.81) * mm});
            skArc(sketch, "E8.102.2", {"start": v(-22.73, 51.05) * mm, "mid": v(-22.49, 51.25) * mm, "end": v(-22.4, 51.54) * mm});
            skArc(sketch, "E8.102.3", {"start": v(-22.73, 51.05) * mm, "mid": v(-23.04, 51) * mm, "end": v(-23.32, 51.13) * mm});
            skArc(sketch, "E8.102.4", {"start": v(-23.32, 51.13) * mm, "mid": v(-23.42, 51.23) * mm, "end": v(-23.5, 51.33) * mm});
            skArc(sketch, "E8.102.5", {"start": v(-23.5, 51.33) * mm, "mid": v(-23.61, 51.42) * mm, "end": v(-23.75, 51.4) * mm});
            skArc(sketch, "E8.103.0", {"start": v(-24.22, 51) * mm, "mid": v(-24.2, 51.14) * mm, "end": v(-24.11, 51.24) * mm});
            skArc(sketch, "E8.103.1", {"start": v(-24.18, 50.73) * mm, "mid": v(-24.2, 50.87) * mm, "end": v(-24.22, 51) * mm});
            skArc(sketch, "E8.103.2", {"start": v(-24.5, 50.22) * mm, "mid": v(-24.26, 50.43) * mm, "end": v(-24.18, 50.73) * mm});
            skArc(sketch, "E8.103.3", {"start": v(-24.5, 50.22) * mm, "mid": v(-24.8, 50.17) * mm, "end": v(-25.1, 50.29) * mm});
            skArc(sketch, "E8.103.4", {"start": v(-25.1, 50.29) * mm, "mid": v(-25.19, 50.38) * mm, "end": v(-25.28, 50.48) * mm});
            skArc(sketch, "E8.103.5", {"start": v(-25.28, 50.48) * mm, "mid": v(-25.4, 50.56) * mm, "end": v(-25.53, 50.54) * mm});
            skArc(sketch, "E8.104.0", {"start": v(-25.98, 50.12) * mm, "mid": v(-25.98, 50.26) * mm, "end": v(-25.89, 50.36) * mm});
            skArc(sketch, "E8.104.1", {"start": v(-25.94, 49.86) * mm, "mid": v(-25.95, 50) * mm, "end": v(-25.98, 50.12) * mm});
            skArc(sketch, "E8.104.2", {"start": v(-26.23, 49.34) * mm, "mid": v(-26, 49.55) * mm, "end": v(-25.94, 49.86) * mm});
            skArc(sketch, "E8.104.3", {"start": v(-26.23, 49.34) * mm, "mid": v(-26.54, 49.27) * mm, "end": v(-26.83, 49.38) * mm});
            skArc(sketch, "E8.104.4", {"start": v(-26.83, 49.38) * mm, "mid": v(-26.93, 49.47) * mm, "end": v(-27.02, 49.57) * mm});
            skArc(sketch, "E8.104.5", {"start": v(-27.02, 49.57) * mm, "mid": v(-27.14, 49.64) * mm, "end": v(-27.28, 49.62) * mm});
            skArc(sketch, "E8.105.0", {"start": v(-27.72, 49.18) * mm, "mid": v(-27.72, 49.32) * mm, "end": v(-27.63, 49.43) * mm});
            skArc(sketch, "E8.105.1", {"start": v(-27.66, 48.92) * mm, "mid": v(-27.68, 49.05) * mm, "end": v(-27.72, 49.18) * mm});
            skArc(sketch, "E8.105.2", {"start": v(-27.94, 48.39) * mm, "mid": v(-27.72, 48.62) * mm, "end": v(-27.66, 48.92) * mm});
            skArc(sketch, "E8.105.3", {"start": v(-27.94, 48.39) * mm, "mid": v(-28.24, 48.32) * mm, "end": v(-28.54, 48.41) * mm});
            skArc(sketch, "E8.105.4", {"start": v(-28.54, 48.41) * mm, "mid": v(-28.64, 48.5) * mm, "end": v(-28.74, 48.6) * mm});
            skArc(sketch, "E8.105.5", {"start": v(-28.74, 48.6) * mm, "mid": v(-28.86, 48.67) * mm, "end": v(-29, 48.64) * mm});
            skArc(sketch, "E8.106.0", {"start": v(-29.42, 48.19) * mm, "mid": v(-29.42, 48.33) * mm, "end": v(-29.34, 48.43) * mm});
            skArc(sketch, "E8.106.1", {"start": v(-29.35, 47.93) * mm, "mid": v(-29.38, 48.06) * mm, "end": v(-29.42, 48.19) * mm});
            skArc(sketch, "E8.106.2", {"start": v(-29.6, 47.39) * mm, "mid": v(-29.4, 47.62) * mm, "end": v(-29.35, 47.93) * mm});
            skArc(sketch, "E8.106.3", {"start": v(-29.6, 47.39) * mm, "mid": v(-29.91, 47.3) * mm, "end": v(-30.2, 47.39) * mm});
            skArc(sketch, "E8.106.4", {"start": v(-30.2, 47.39) * mm, "mid": v(-30.32, 47.47) * mm, "end": v(-30.41, 47.56) * mm});
            skArc(sketch, "E8.106.5", {"start": v(-30.41, 47.56) * mm, "mid": v(-30.54, 47.63) * mm, "end": v(-30.67, 47.6) * mm});
            skArc(sketch, "E8.107.0", {"start": v(-31.08, 47.13) * mm, "mid": v(-31.1, 47.27) * mm, "end": v(-31, 47.38) * mm});
            skArc(sketch, "E8.107.1", {"start": v(-31, 46.87) * mm, "mid": v(-31.03, 47) * mm, "end": v(-31.08, 47.13) * mm});
            skArc(sketch, "E8.107.2", {"start": v(-31.25, 46.32) * mm, "mid": v(-31.05, 46.56) * mm, "end": v(-31, 46.87) * mm});
            skArc(sketch, "E8.107.3", {"start": v(-31.25, 46.32) * mm, "mid": v(-31.54, 46.23) * mm, "end": v(-31.84, 46.3) * mm});
            skArc(sketch, "E8.107.4", {"start": v(-31.84, 46.3) * mm, "mid": v(-31.96, 46.38) * mm, "end": v(-32.06, 46.47) * mm});
            skArc(sketch, "E8.107.5", {"start": v(-32.06, 46.47) * mm, "mid": v(-32.18, 46.53) * mm, "end": v(-32.31, 46.5) * mm});
            skArc(sketch, "E8.108.0", {"start": v(-32.7, 46.02) * mm, "mid": v(-32.72, 46.16) * mm, "end": v(-32.64, 46.27) * mm});
            skArc(sketch, "E8.108.1", {"start": v(-32.62, 45.76) * mm, "mid": v(-32.66, 45.9) * mm, "end": v(-32.7, 46.02) * mm});
            skArc(sketch, "E8.108.2", {"start": v(-32.84, 45.2) * mm, "mid": v(-32.65, 45.45) * mm, "end": v(-32.62, 45.76) * mm});
            skArc(sketch, "E8.108.3", {"start": v(-32.84, 45.2) * mm, "mid": v(-33.14, 45.1) * mm, "end": v(-33.44, 45.17) * mm});
            skArc(sketch, "E8.108.4", {"start": v(-33.44, 45.17) * mm, "mid": v(-33.56, 45.24) * mm, "end": v(-33.66, 45.33) * mm});
            skArc(sketch, "E8.108.5", {"start": v(-33.66, 45.33) * mm, "mid": v(-33.78, 45.38) * mm, "end": v(-33.92, 45.34) * mm});
            skArc(sketch, "E8.109.0", {"start": v(-34.3, 44.85) * mm, "mid": v(-34.31, 44.99) * mm, "end": v(-34.24, 45.1) * mm});
            skArc(sketch, "E8.109.1", {"start": v(-34.2, 44.6) * mm, "mid": v(-34.24, 44.73) * mm, "end": v(-34.3, 44.85) * mm});
            skArc(sketch, "E8.109.2", {"start": v(-34.4, 44.03) * mm, "mid": v(-34.22, 44.28) * mm, "end": v(-34.2, 44.6) * mm});
            skArc(sketch, "E8.109.3", {"start": v(-34.4, 44.03) * mm, "mid": v(-34.7, 43.91) * mm, "end": v(-35, 43.97) * mm});
            skArc(sketch, "E8.109.4", {"start": v(-35, 43.97) * mm, "mid": v(-35.11, 44.04) * mm, "end": v(-35.22, 44.12) * mm});
            skArc(sketch, "E8.109.5", {"start": v(-35.22, 44.12) * mm, "mid": v(-35.35, 44.18) * mm, "end": v(-35.48, 44.13) * mm});
            skArc(sketch, "E8.110.0", {"start": v(-35.84, 43.62) * mm, "mid": v(-35.86, 43.76) * mm, "end": v(-35.8, 43.88) * mm});
            skArc(sketch, "E8.110.1", {"start": v(-35.73, 43.37) * mm, "mid": v(-35.78, 43.5) * mm, "end": v(-35.84, 43.62) * mm});
            skArc(sketch, "E8.110.2", {"start": v(-35.92, 42.8) * mm, "mid": v(-35.74, 43.06) * mm, "end": v(-35.73, 43.37) * mm});
            skArc(sketch, "E8.110.3", {"start": v(-35.92, 42.8) * mm, "mid": v(-36.2, 42.68) * mm, "end": v(-36.51, 42.72) * mm});
            skArc(sketch, "E8.110.4", {"start": v(-36.51, 42.72) * mm, "mid": v(-36.63, 42.79) * mm, "end": v(-36.74, 42.87) * mm});
            skArc(sketch, "E8.110.5", {"start": v(-36.74, 42.87) * mm, "mid": v(-36.87, 42.92) * mm, "end": v(-37, 42.87) * mm});
            skArc(sketch, "E8.111.0", {"start": v(-37.34, 42.35) * mm, "mid": v(-37.37, 42.48) * mm, "end": v(-37.3, 42.6) * mm});
            skArc(sketch, "E8.111.1", {"start": v(-37.23, 42.1) * mm, "mid": v(-37.27, 42.23) * mm, "end": v(-37.34, 42.35) * mm});
            skArc(sketch, "E8.111.2", {"start": v(-37.39, 41.52) * mm, "mid": v(-37.22, 41.79) * mm, "end": v(-37.23, 42.1) * mm});
            skArc(sketch, "E8.111.3", {"start": v(-37.39, 41.52) * mm, "mid": v(-37.67, 41.39) * mm, "end": v(-37.98, 41.42) * mm});
            skArc(sketch, "E8.111.4", {"start": v(-37.98, 41.42) * mm, "mid": v(-38.1, 41.48) * mm, "end": v(-38.21, 41.56) * mm});
            skArc(sketch, "E8.111.5", {"start": v(-38.21, 41.56) * mm, "mid": v(-38.34, 41.6) * mm, "end": v(-38.47, 41.55) * mm});
            skArc(sketch, "E8.112.0", {"start": v(-38.8, 41.02) * mm, "mid": v(-38.83, 41.15) * mm, "end": v(-38.77, 41.28) * mm});
            skArc(sketch, "E8.112.1", {"start": v(-38.67, 40.78) * mm, "mid": v(-38.73, 40.9) * mm, "end": v(-38.8, 41.02) * mm});
            skArc(sketch, "E8.112.2", {"start": v(-38.81, 40.2) * mm, "mid": v(-38.66, 40.46) * mm, "end": v(-38.67, 40.78) * mm});
            skArc(sketch, "E8.112.3", {"start": v(-38.81, 40.2) * mm, "mid": v(-39.1, 40.05) * mm, "end": v(-39.4, 40.07) * mm});
            skArc(sketch, "E8.112.4", {"start": v(-39.4, 40.07) * mm, "mid": v(-39.52, 40.13) * mm, "end": v(-39.64, 40.2) * mm});
            skArc(sketch, "E8.112.5", {"start": v(-39.64, 40.2) * mm, "mid": v(-39.77, 40.24) * mm, "end": v(-39.9, 40.18) * mm});
            skArc(sketch, "E8.113.0", {"start": v(-40.2, 39.64) * mm, "mid": v(-40.24, 39.77) * mm, "end": v(-40.18, 39.9) * mm});
            skArc(sketch, "E8.113.1", {"start": v(-40.07, 39.4) * mm, "mid": v(-40.13, 39.52) * mm, "end": v(-40.2, 39.64) * mm});
            skArc(sketch, "E8.113.2", {"start": v(-40.2, 38.81) * mm, "mid": v(-40.05, 39.1) * mm, "end": v(-40.07, 39.4) * mm});
            skArc(sketch, "E8.113.3", {"start": v(-40.2, 38.81) * mm, "mid": v(-40.46, 38.66) * mm, "end": v(-40.78, 38.67) * mm});
            skArc(sketch, "E8.113.4", {"start": v(-40.78, 38.67) * mm, "mid": v(-40.9, 38.73) * mm, "end": v(-41.02, 38.8) * mm});
            skArc(sketch, "E8.113.5", {"start": v(-41.02, 38.8) * mm, "mid": v(-41.15, 38.83) * mm, "end": v(-41.28, 38.77) * mm});
            skArc(sketch, "E8.114.0", {"start": v(-41.56, 38.21) * mm, "mid": v(-41.6, 38.34) * mm, "end": v(-41.55, 38.47) * mm});
            skArc(sketch, "E8.114.1", {"start": v(-41.42, 37.98) * mm, "mid": v(-41.48, 38.1) * mm, "end": v(-41.56, 38.21) * mm});
            skArc(sketch, "E8.114.2", {"start": v(-41.52, 37.39) * mm, "mid": v(-41.39, 37.67) * mm, "end": v(-41.42, 37.98) * mm});
            skArc(sketch, "E8.114.3", {"start": v(-41.52, 37.39) * mm, "mid": v(-41.79, 37.22) * mm, "end": v(-42.1, 37.23) * mm});
            skArc(sketch, "E8.114.4", {"start": v(-42.1, 37.23) * mm, "mid": v(-42.23, 37.27) * mm, "end": v(-42.35, 37.34) * mm});
            skArc(sketch, "E8.114.5", {"start": v(-42.35, 37.34) * mm, "mid": v(-42.48, 37.37) * mm, "end": v(-42.6, 37.3) * mm});
            skArc(sketch, "E8.115.0", {"start": v(-42.87, 36.74) * mm, "mid": v(-42.92, 36.87) * mm, "end": v(-42.87, 37) * mm});
            skArc(sketch, "E8.115.1", {"start": v(-42.72, 36.51) * mm, "mid": v(-42.79, 36.63) * mm, "end": v(-42.87, 36.74) * mm});
            skArc(sketch, "E8.115.2", {"start": v(-42.8, 35.92) * mm, "mid": v(-42.68, 36.2) * mm, "end": v(-42.72, 36.51) * mm});
            skArc(sketch, "E8.115.3", {"start": v(-42.8, 35.92) * mm, "mid": v(-43.06, 35.74) * mm, "end": v(-43.37, 35.73) * mm});
            skArc(sketch, "E8.115.4", {"start": v(-43.37, 35.73) * mm, "mid": v(-43.5, 35.78) * mm, "end": v(-43.62, 35.84) * mm});
            skArc(sketch, "E8.115.5", {"start": v(-43.62, 35.84) * mm, "mid": v(-43.76, 35.86) * mm, "end": v(-43.88, 35.8) * mm});
            skArc(sketch, "E8.116.0", {"start": v(-44.12, 35.22) * mm, "mid": v(-44.18, 35.35) * mm, "end": v(-44.13, 35.48) * mm});
            skArc(sketch, "E8.116.1", {"start": v(-43.97, 35) * mm, "mid": v(-44.04, 35.11) * mm, "end": v(-44.12, 35.22) * mm});
            skArc(sketch, "E8.116.2", {"start": v(-44.03, 34.4) * mm, "mid": v(-43.91, 34.7) * mm, "end": v(-43.97, 35) * mm});
            skArc(sketch, "E8.116.3", {"start": v(-44.03, 34.4) * mm, "mid": v(-44.28, 34.22) * mm, "end": v(-44.6, 34.2) * mm});
            skArc(sketch, "E8.116.4", {"start": v(-44.6, 34.2) * mm, "mid": v(-44.73, 34.24) * mm, "end": v(-44.85, 34.3) * mm});
            skArc(sketch, "E8.116.5", {"start": v(-44.85, 34.3) * mm, "mid": v(-44.99, 34.31) * mm, "end": v(-45.1, 34.24) * mm});
            skArc(sketch, "E8.117.0", {"start": v(-45.33, 33.66) * mm, "mid": v(-45.38, 33.78) * mm, "end": v(-45.34, 33.92) * mm});
            skArc(sketch, "E8.117.1", {"start": v(-45.17, 33.44) * mm, "mid": v(-45.24, 33.56) * mm, "end": v(-45.33, 33.66) * mm});
            skArc(sketch, "E8.117.2", {"start": v(-45.2, 32.84) * mm, "mid": v(-45.1, 33.14) * mm, "end": v(-45.17, 33.44) * mm});
            skArc(sketch, "E8.117.3", {"start": v(-45.2, 32.84) * mm, "mid": v(-45.45, 32.65) * mm, "end": v(-45.76, 32.62) * mm});
            skArc(sketch, "E8.117.4", {"start": v(-45.76, 32.62) * mm, "mid": v(-45.9, 32.66) * mm, "end": v(-46.02, 32.7) * mm});
            skArc(sketch, "E8.117.5", {"start": v(-46.02, 32.7) * mm, "mid": v(-46.16, 32.72) * mm, "end": v(-46.27, 32.64) * mm});
            skArc(sketch, "E8.118.0", {"start": v(-46.47, 32.06) * mm, "mid": v(-46.53, 32.18) * mm, "end": v(-46.5, 32.31) * mm});
            skArc(sketch, "E8.118.1", {"start": v(-46.3, 31.84) * mm, "mid": v(-46.38, 31.96) * mm, "end": v(-46.47, 32.06) * mm});
            skArc(sketch, "E8.118.2", {"start": v(-46.32, 31.25) * mm, "mid": v(-46.23, 31.54) * mm, "end": v(-46.3, 31.84) * mm});
            skArc(sketch, "E8.118.3", {"start": v(-46.32, 31.25) * mm, "mid": v(-46.56, 31.05) * mm, "end": v(-46.87, 31) * mm});
            skArc(sketch, "E8.118.4", {"start": v(-46.87, 31) * mm, "mid": v(-47, 31.03) * mm, "end": v(-47.13, 31.08) * mm});
            skArc(sketch, "E8.118.5", {"start": v(-47.13, 31.08) * mm, "mid": v(-47.27, 31.1) * mm, "end": v(-47.38, 31) * mm});
            skArc(sketch, "E8.119.0", {"start": v(-47.56, 30.41) * mm, "mid": v(-47.63, 30.54) * mm, "end": v(-47.6, 30.67) * mm});
            skArc(sketch, "E8.119.1", {"start": v(-47.39, 30.2) * mm, "mid": v(-47.47, 30.32) * mm, "end": v(-47.56, 30.41) * mm});
            skArc(sketch, "E8.119.2", {"start": v(-47.39, 29.6) * mm, "mid": v(-47.3, 29.91) * mm, "end": v(-47.39, 30.2) * mm});
            skArc(sketch, "E8.119.3", {"start": v(-47.39, 29.6) * mm, "mid": v(-47.62, 29.4) * mm, "end": v(-47.93, 29.35) * mm});
            skArc(sketch, "E8.119.4", {"start": v(-47.93, 29.35) * mm, "mid": v(-48.06, 29.38) * mm, "end": v(-48.19, 29.42) * mm});
            skArc(sketch, "E8.119.5", {"start": v(-48.19, 29.42) * mm, "mid": v(-48.33, 29.42) * mm, "end": v(-48.43, 29.34) * mm});
            skArc(sketch, "E8.120.0", {"start": v(-48.6, 28.74) * mm, "mid": v(-48.67, 28.86) * mm, "end": v(-48.64, 29) * mm});
            skArc(sketch, "E8.120.1", {"start": v(-48.41, 28.54) * mm, "mid": v(-48.5, 28.64) * mm, "end": v(-48.6, 28.74) * mm});
            skArc(sketch, "E8.120.2", {"start": v(-48.39, 27.94) * mm, "mid": v(-48.32, 28.24) * mm, "end": v(-48.41, 28.54) * mm});
            skArc(sketch, "E8.120.3", {"start": v(-48.39, 27.94) * mm, "mid": v(-48.62, 27.72) * mm, "end": v(-48.92, 27.66) * mm});
            skArc(sketch, "E8.120.4", {"start": v(-48.92, 27.66) * mm, "mid": v(-49.05, 27.68) * mm, "end": v(-49.18, 27.72) * mm});
            skArc(sketch, "E8.120.5", {"start": v(-49.18, 27.72) * mm, "mid": v(-49.32, 27.72) * mm, "end": v(-49.43, 27.63) * mm});
            skArc(sketch, "E8.121.0", {"start": v(-49.57, 27.02) * mm, "mid": v(-49.64, 27.14) * mm, "end": v(-49.62, 27.28) * mm});
            skArc(sketch, "E8.121.1", {"start": v(-49.38, 26.83) * mm, "mid": v(-49.47, 26.93) * mm, "end": v(-49.57, 27.02) * mm});
            skArc(sketch, "E8.121.2", {"start": v(-49.34, 26.23) * mm, "mid": v(-49.27, 26.54) * mm, "end": v(-49.38, 26.83) * mm});
            skArc(sketch, "E8.121.3", {"start": v(-49.34, 26.23) * mm, "mid": v(-49.55, 26) * mm, "end": v(-49.86, 25.94) * mm});
            skArc(sketch, "E8.121.4", {"start": v(-49.86, 25.94) * mm, "mid": v(-50, 25.95) * mm, "end": v(-50.12, 25.98) * mm});
            skArc(sketch, "E8.121.5", {"start": v(-50.12, 25.98) * mm, "mid": v(-50.26, 25.98) * mm, "end": v(-50.36, 25.89) * mm});
            skArc(sketch, "E8.122.0", {"start": v(-50.48, 25.28) * mm, "mid": v(-50.56, 25.4) * mm, "end": v(-50.54, 25.53) * mm});
            skArc(sketch, "E8.122.1", {"start": v(-50.29, 25.1) * mm, "mid": v(-50.38, 25.19) * mm, "end": v(-50.48, 25.28) * mm});
            skArc(sketch, "E8.122.2", {"start": v(-50.22, 24.5) * mm, "mid": v(-50.17, 24.8) * mm, "end": v(-50.29, 25.1) * mm});
            skArc(sketch, "E8.122.3", {"start": v(-50.22, 24.5) * mm, "mid": v(-50.43, 24.26) * mm, "end": v(-50.73, 24.18) * mm});
            skArc(sketch, "E8.122.4", {"start": v(-50.73, 24.18) * mm, "mid": v(-50.87, 24.2) * mm, "end": v(-51, 24.22) * mm});
            skArc(sketch, "E8.122.5", {"start": v(-51, 24.22) * mm, "mid": v(-51.14, 24.2) * mm, "end": v(-51.24, 24.11) * mm});
            skArc(sketch, "E8.123.0", {"start": v(-51.33, 23.5) * mm, "mid": v(-51.42, 23.61) * mm, "end": v(-51.4, 23.75) * mm});
            skArc(sketch, "E8.123.1", {"start": v(-51.13, 23.32) * mm, "mid": v(-51.23, 23.42) * mm, "end": v(-51.33, 23.5) * mm});
            skArc(sketch, "E8.123.2", {"start": v(-51.05, 22.73) * mm, "mid": v(-51, 23.04) * mm, "end": v(-51.13, 23.32) * mm});
            skArc(sketch, "E8.123.3", {"start": v(-51.05, 22.73) * mm, "mid": v(-51.25, 22.49) * mm, "end": v(-51.54, 22.4) * mm});
            skArc(sketch, "E8.123.4", {"start": v(-51.54, 22.4) * mm, "mid": v(-51.68, 22.4) * mm, "end": v(-51.81, 22.43) * mm});
            skArc(sketch, "E8.123.5", {"start": v(-51.81, 22.43) * mm, "mid": v(-51.95, 22.41) * mm, "end": v(-52.05, 22.31) * mm});
            skArc(sketch, "E8.124.0", {"start": v(-52.12, 21.7) * mm, "mid": v(-52.2, 21.8) * mm, "end": v(-52.2, 21.94) * mm});
            skArc(sketch, "E8.124.1", {"start": v(-51.92, 21.52) * mm, "mid": v(-52.01, 21.61) * mm, "end": v(-52.12, 21.7) * mm});
            skArc(sketch, "E8.124.2", {"start": v(-51.8, 20.93) * mm, "mid": v(-51.78, 21.24) * mm, "end": v(-51.92, 21.52) * mm});
            skArc(sketch, "E8.124.3", {"start": v(-51.8, 20.93) * mm, "mid": v(-52, 20.69) * mm, "end": v(-52.3, 20.58) * mm});
            skArc(sketch, "E8.124.4", {"start": v(-52.3, 20.58) * mm, "mid": v(-52.43, 20.58) * mm, "end": v(-52.56, 20.6) * mm});
            skArc(sketch, "E8.124.5", {"start": v(-52.56, 20.6) * mm, "mid": v(-52.7, 20.58) * mm, "end": v(-52.8, 20.48) * mm});
            skArc(sketch, "E8.125.0", {"start": v(-52.85, 19.86) * mm, "mid": v(-52.94, 19.97) * mm, "end": v(-52.94, 20.1) * mm});
            skArc(sketch, "E8.125.1", {"start": v(-52.63, 19.7) * mm, "mid": v(-52.74, 19.79) * mm, "end": v(-52.85, 19.86) * mm});
            skArc(sketch, "E8.125.2", {"start": v(-52.5, 19.11) * mm, "mid": v(-52.49, 19.42) * mm, "end": v(-52.63, 19.7) * mm});
            skArc(sketch, "E8.125.3", {"start": v(-52.5, 19.11) * mm, "mid": v(-52.7, 18.86) * mm, "end": v(-52.98, 18.74) * mm});
            skArc(sketch, "E8.125.4", {"start": v(-52.98, 18.74) * mm, "mid": v(-53.12, 18.74) * mm, "end": v(-53.25, 18.76) * mm});
            skArc(sketch, "E8.125.5", {"start": v(-53.25, 18.76) * mm, "mid": v(-53.39, 18.73) * mm, "end": v(-53.48, 18.63) * mm});
            skArc(sketch, "E8.126.0", {"start": v(-53.5, 18) * mm, "mid": v(-53.6, 18.1) * mm, "end": v(-53.6, 18.25) * mm});
            skArc(sketch, "E8.126.1", {"start": v(-53.29, 17.85) * mm, "mid": v(-53.4, 17.93) * mm, "end": v(-53.5, 18) * mm});
            skArc(sketch, "E8.126.2", {"start": v(-53.14, 17.27) * mm, "mid": v(-53.13, 17.58) * mm, "end": v(-53.29, 17.85) * mm});
            skArc(sketch, "E8.126.3", {"start": v(-53.14, 17.27) * mm, "mid": v(-53.32, 17) * mm, "end": v(-53.6, 16.88) * mm});
            skArc(sketch, "E8.126.4", {"start": v(-53.6, 16.88) * mm, "mid": v(-53.74, 16.88) * mm, "end": v(-53.87, 16.89) * mm});
            skArc(sketch, "E8.126.5", {"start": v(-53.87, 16.89) * mm, "mid": v(-54, 16.86) * mm, "end": v(-54.1, 16.75) * mm});
            skArc(sketch, "E8.127.0", {"start": v(-54.1, 16.13) * mm, "mid": v(-54.2, 16.23) * mm, "end": v(-54.2, 16.36) * mm});
            skArc(sketch, "E8.127.1", {"start": v(-53.88, 15.98) * mm, "mid": v(-53.99, 16.06) * mm, "end": v(-54.1, 16.13) * mm});
            skArc(sketch, "E8.127.2", {"start": v(-53.71, 15.4) * mm, "mid": v(-53.71, 15.71) * mm, "end": v(-53.88, 15.98) * mm});
            skArc(sketch, "E8.127.3", {"start": v(-53.71, 15.4) * mm, "mid": v(-53.88, 15.14) * mm, "end": v(-54.16, 15) * mm});
            skArc(sketch, "E8.127.4", {"start": v(-54.16, 15) * mm, "mid": v(-54.3, 15) * mm, "end": v(-54.43, 15) * mm});
            skArc(sketch, "E8.127.5", {"start": v(-54.43, 15) * mm, "mid": v(-54.56, 14.96) * mm, "end": v(-54.64, 14.85) * mm});
            skArc(sketch, "E8.128.0", {"start": v(-54.64, 14.23) * mm, "mid": v(-54.73, 14.32) * mm, "end": v(-54.75, 14.46) * mm});
            skArc(sketch, "E8.128.1", {"start": v(-54.4, 14.09) * mm, "mid": v(-54.52, 14.17) * mm, "end": v(-54.64, 14.23) * mm});
            skArc(sketch, "E8.128.2", {"start": v(-54.22, 13.52) * mm, "mid": v(-54.23, 13.83) * mm, "end": v(-54.4, 14.09) * mm});
            skArc(sketch, "E8.128.3", {"start": v(-54.22, 13.52) * mm, "mid": v(-54.37, 13.25) * mm, "end": v(-54.65, 13.1) * mm});
            skArc(sketch, "E8.128.4", {"start": v(-54.65, 13.1) * mm, "mid": v(-54.78, 13.09) * mm, "end": v(-54.92, 13.09) * mm});
            skArc(sketch, "E8.128.5", {"start": v(-54.92, 13.09) * mm, "mid": v(-55.05, 13.05) * mm, "end": v(-55.13, 12.93) * mm});
            skArc(sketch, "E8.129.0", {"start": v(-55.1, 12.31) * mm, "mid": v(-55.2, 12.4) * mm, "end": v(-55.22, 12.54) * mm});
            skArc(sketch, "E8.129.1", {"start": v(-54.86, 12.18) * mm, "mid": v(-54.98, 12.25) * mm, "end": v(-55.1, 12.31) * mm});
            skArc(sketch, "E8.129.2", {"start": v(-54.65, 11.62) * mm, "mid": v(-54.68, 11.93) * mm, "end": v(-54.86, 12.18) * mm});
            skArc(sketch, "E8.129.3", {"start": v(-54.65, 11.62) * mm, "mid": v(-54.8, 11.34) * mm, "end": v(-55.07, 11.19) * mm});
            skArc(sketch, "E8.129.4", {"start": v(-55.07, 11.19) * mm, "mid": v(-55.2, 11.17) * mm, "end": v(-55.34, 11.16) * mm});
            skArc(sketch, "E8.129.5", {"start": v(-55.34, 11.16) * mm, "mid": v(-55.47, 11.12) * mm, "end": v(-55.55, 11) * mm});
            skArc(sketch, "E8.130.0", {"start": v(-55.5, 10.38) * mm, "mid": v(-55.6, 10.47) * mm, "end": v(-55.62, 10.6) * mm});
            skArc(sketch, "E8.130.1", {"start": v(-55.26, 10.26) * mm, "mid": v(-55.37, 10.33) * mm, "end": v(-55.5, 10.38) * mm});
            skArc(sketch, "E8.130.2", {"start": v(-55.03, 9.7) * mm, "mid": v(-55.06, 10.01) * mm, "end": v(-55.26, 10.26) * mm});
            skArc(sketch, "E8.130.3", {"start": v(-55.03, 9.7) * mm, "mid": v(-55.16, 9.42) * mm, "end": v(-55.43, 9.26) * mm});
            skArc(sketch, "E8.130.4", {"start": v(-55.43, 9.26) * mm, "mid": v(-55.56, 9.23) * mm, "end": v(-55.7, 9.22) * mm});
            skArc(sketch, "E8.130.5", {"start": v(-55.7, 9.22) * mm, "mid": v(-55.83, 9.18) * mm, "end": v(-55.9, 9.06) * mm});
            skArc(sketch, "E8.131.0", {"start": v(-55.82, 8.44) * mm, "mid": v(-55.93, 8.52) * mm, "end": v(-55.96, 8.66) * mm});
            skArc(sketch, "E8.131.1", {"start": v(-55.58, 8.32) * mm, "mid": v(-55.7, 8.39) * mm, "end": v(-55.82, 8.44) * mm});
            skArc(sketch, "E8.131.2", {"start": v(-55.33, 7.78) * mm, "mid": v(-55.38, 8.09) * mm, "end": v(-55.58, 8.32) * mm});
            skArc(sketch, "E8.131.3", {"start": v(-55.33, 7.78) * mm, "mid": v(-55.46, 7.5) * mm, "end": v(-55.72, 7.32) * mm});
            skArc(sketch, "E8.131.4", {"start": v(-55.72, 7.32) * mm, "mid": v(-55.85, 7.29) * mm, "end": v(-55.99, 7.27) * mm});
            skArc(sketch, "E8.131.5", {"start": v(-55.99, 7.27) * mm, "mid": v(-56.12, 7.22) * mm, "end": v(-56.18, 7.1) * mm});
            skArc(sketch, "E8.132.0", {"start": v(-56.08, 6.49) * mm, "mid": v(-56.2, 6.57) * mm, "end": v(-56.23, 6.7) * mm});
            skArc(sketch, "E8.132.1", {"start": v(-55.84, 6.38) * mm, "mid": v(-55.96, 6.44) * mm, "end": v(-56.08, 6.49) * mm});
            skArc(sketch, "E8.132.2", {"start": v(-55.57, 5.84) * mm, "mid": v(-55.62, 6.15) * mm, "end": v(-55.84, 6.38) * mm});
            skArc(sketch, "E8.132.3", {"start": v(-55.57, 5.84) * mm, "mid": v(-55.69, 5.55) * mm, "end": v(-55.94, 5.37) * mm});
            skArc(sketch, "E8.132.4", {"start": v(-55.94, 5.37) * mm, "mid": v(-56.07, 5.33) * mm, "end": v(-56.2, 5.32) * mm});
            skArc(sketch, "E8.132.5", {"start": v(-56.2, 5.32) * mm, "mid": v(-56.33, 5.26) * mm, "end": v(-56.4, 5.14) * mm});
            skArc(sketch, "E8.133.0", {"start": v(-56.28, 4.52) * mm, "mid": v(-56.4, 4.6) * mm, "end": v(-56.43, 4.74) * mm});
            skArc(sketch, "E8.133.1", {"start": v(-56.02, 4.43) * mm, "mid": v(-56.15, 4.48) * mm, "end": v(-56.28, 4.52) * mm});
            skArc(sketch, "E8.133.2", {"start": v(-55.74, 3.9) * mm, "mid": v(-55.8, 4.2) * mm, "end": v(-56.02, 4.43) * mm});
            skArc(sketch, "E8.133.3", {"start": v(-55.74, 3.9) * mm, "mid": v(-55.85, 3.6) * mm, "end": v(-56.1, 3.41) * mm});
            skArc(sketch, "E8.133.4", {"start": v(-56.1, 3.41) * mm, "mid": v(-56.22, 3.37) * mm, "end": v(-56.36, 3.35) * mm});
            skArc(sketch, "E8.133.5", {"start": v(-56.36, 3.35) * mm, "mid": v(-56.48, 3.3) * mm, "end": v(-56.54, 3.16) * mm});
            skArc(sketch, "E8.134.0", {"start": v(-56.4, 2.56) * mm, "mid": v(-56.52, 2.63) * mm, "end": v(-56.56, 2.76) * mm});
            skArc(sketch, "E8.134.1", {"start": v(-56.15, 2.47) * mm, "mid": v(-56.27, 2.52) * mm, "end": v(-56.4, 2.56) * mm});
            skArc(sketch, "E8.134.2", {"start": v(-55.84, 1.95) * mm, "mid": v(-55.92, 2.25) * mm, "end": v(-56.15, 2.47) * mm});
            skArc(sketch, "E8.134.3", {"start": v(-55.84, 1.95) * mm, "mid": v(-55.94, 1.65) * mm, "end": v(-56.18, 1.46) * mm});
            skArc(sketch, "E8.134.4", {"start": v(-56.18, 1.46) * mm, "mid": v(-56.3, 1.41) * mm, "end": v(-56.44, 1.38) * mm});
            skArc(sketch, "E8.134.5", {"start": v(-56.44, 1.38) * mm, "mid": v(-56.56, 1.32) * mm, "end": v(-56.61, 1.19) * mm});
            skArc(sketch, "E8.135.0", {"start": v(-56.45, 0.59) * mm, "mid": v(-56.57, 0.66) * mm, "end": v(-56.62, 0.79) * mm});
            skArc(sketch, "E8.135.1", {"start": v(-56.2, 0.5) * mm, "mid": v(-56.32, 0.56) * mm, "end": v(-56.45, 0.59) * mm});
            skArc(sketch, "E8.135.2", {"start": v(-55.88, 0) * mm, "mid": v(-55.96, 0.3) * mm, "end": v(-56.2, 0.5) * mm});
            skArc(sketch, "E8.135.3", {"start": v(-55.88, 0) * mm, "mid": v(-55.96, -0.3) * mm, "end": v(-56.2, -0.5) * mm});
            skArc(sketch, "E8.135.4", {"start": v(-56.2, -0.5) * mm, "mid": v(-56.32, -0.56) * mm, "end": v(-56.45, -0.59) * mm});
            skArc(sketch, "E8.135.5", {"start": v(-56.45, -0.59) * mm, "mid": v(-56.57, -0.66) * mm, "end": v(-56.62, -0.79) * mm});
            skArc(sketch, "E8.136.0", {"start": v(-56.44, -1.38) * mm, "mid": v(-56.56, -1.32) * mm, "end": v(-56.61, -1.19) * mm});
            skArc(sketch, "E8.136.1", {"start": v(-56.18, -1.46) * mm, "mid": v(-56.3, -1.41) * mm, "end": v(-56.44, -1.38) * mm});
            skArc(sketch, "E8.136.2", {"start": v(-55.84, -1.95) * mm, "mid": v(-55.94, -1.65) * mm, "end": v(-56.18, -1.46) * mm});
            skArc(sketch, "E8.136.3", {"start": v(-55.84, -1.95) * mm, "mid": v(-55.92, -2.25) * mm, "end": v(-56.15, -2.47) * mm});
            skArc(sketch, "E8.136.4", {"start": v(-56.15, -2.47) * mm, "mid": v(-56.27, -2.52) * mm, "end": v(-56.4, -2.56) * mm});
            skArc(sketch, "E8.136.5", {"start": v(-56.4, -2.56) * mm, "mid": v(-56.52, -2.63) * mm, "end": v(-56.56, -2.76) * mm});
            skArc(sketch, "E8.137.0", {"start": v(-56.36, -3.35) * mm, "mid": v(-56.48, -3.3) * mm, "end": v(-56.54, -3.16) * mm});
            skArc(sketch, "E8.137.1", {"start": v(-56.1, -3.41) * mm, "mid": v(-56.22, -3.37) * mm, "end": v(-56.36, -3.35) * mm});
            skArc(sketch, "E8.137.2", {"start": v(-55.74, -3.9) * mm, "mid": v(-55.85, -3.6) * mm, "end": v(-56.1, -3.41) * mm});
            skArc(sketch, "E8.137.3", {"start": v(-55.74, -3.9) * mm, "mid": v(-55.8, -4.2) * mm, "end": v(-56.02, -4.43) * mm});
            skArc(sketch, "E8.137.4", {"start": v(-56.02, -4.43) * mm, "mid": v(-56.15, -4.48) * mm, "end": v(-56.28, -4.52) * mm});
            skArc(sketch, "E8.137.5", {"start": v(-56.28, -4.52) * mm, "mid": v(-56.4, -4.6) * mm, "end": v(-56.43, -4.74) * mm});
            skArc(sketch, "E8.138.0", {"start": v(-56.2, -5.32) * mm, "mid": v(-56.33, -5.26) * mm, "end": v(-56.4, -5.14) * mm});
            skArc(sketch, "E8.138.1", {"start": v(-55.94, -5.37) * mm, "mid": v(-56.07, -5.33) * mm, "end": v(-56.2, -5.32) * mm});
            skArc(sketch, "E8.138.2", {"start": v(-55.57, -5.84) * mm, "mid": v(-55.69, -5.55) * mm, "end": v(-55.94, -5.37) * mm});
            skArc(sketch, "E8.138.3", {"start": v(-55.57, -5.84) * mm, "mid": v(-55.62, -6.15) * mm, "end": v(-55.84, -6.38) * mm});
            skArc(sketch, "E8.138.4", {"start": v(-55.84, -6.38) * mm, "mid": v(-55.96, -6.44) * mm, "end": v(-56.08, -6.49) * mm});
            skArc(sketch, "E8.138.5", {"start": v(-56.08, -6.49) * mm, "mid": v(-56.2, -6.57) * mm, "end": v(-56.23, -6.7) * mm});
            skArc(sketch, "E8.139.0", {"start": v(-55.99, -7.27) * mm, "mid": v(-56.12, -7.22) * mm, "end": v(-56.18, -7.1) * mm});
            skArc(sketch, "E8.139.1", {"start": v(-55.72, -7.32) * mm, "mid": v(-55.85, -7.29) * mm, "end": v(-55.99, -7.27) * mm});
            skArc(sketch, "E8.139.2", {"start": v(-55.33, -7.78) * mm, "mid": v(-55.46, -7.5) * mm, "end": v(-55.72, -7.32) * mm});
            skArc(sketch, "E8.139.3", {"start": v(-55.33, -7.78) * mm, "mid": v(-55.38, -8.09) * mm, "end": v(-55.58, -8.32) * mm});
            skArc(sketch, "E8.139.4", {"start": v(-55.58, -8.32) * mm, "mid": v(-55.7, -8.39) * mm, "end": v(-55.82, -8.44) * mm});
            skArc(sketch, "E8.139.5", {"start": v(-55.82, -8.44) * mm, "mid": v(-55.93, -8.52) * mm, "end": v(-55.96, -8.66) * mm});
            skArc(sketch, "E8.140.0", {"start": v(-55.7, -9.22) * mm, "mid": v(-55.83, -9.18) * mm, "end": v(-55.9, -9.06) * mm});
            skArc(sketch, "E8.140.1", {"start": v(-55.43, -9.26) * mm, "mid": v(-55.56, -9.23) * mm, "end": v(-55.7, -9.22) * mm});
            skArc(sketch, "E8.140.2", {"start": v(-55.03, -9.7) * mm, "mid": v(-55.16, -9.42) * mm, "end": v(-55.43, -9.26) * mm});
            skArc(sketch, "E8.140.3", {"start": v(-55.03, -9.7) * mm, "mid": v(-55.06, -10.01) * mm, "end": v(-55.26, -10.26) * mm});
            skArc(sketch, "E8.140.4", {"start": v(-55.26, -10.26) * mm, "mid": v(-55.37, -10.33) * mm, "end": v(-55.5, -10.38) * mm});
            skArc(sketch, "E8.140.5", {"start": v(-55.5, -10.38) * mm, "mid": v(-55.6, -10.47) * mm, "end": v(-55.62, -10.6) * mm});
            skArc(sketch, "E8.141.0", {"start": v(-55.34, -11.16) * mm, "mid": v(-55.47, -11.12) * mm, "end": v(-55.55, -11) * mm});
            skArc(sketch, "E8.141.1", {"start": v(-55.07, -11.19) * mm, "mid": v(-55.2, -11.17) * mm, "end": v(-55.34, -11.16) * mm});
            skArc(sketch, "E8.141.2", {"start": v(-54.65, -11.62) * mm, "mid": v(-54.8, -11.34) * mm, "end": v(-55.07, -11.19) * mm});
            skArc(sketch, "E8.141.3", {"start": v(-54.65, -11.62) * mm, "mid": v(-54.68, -11.93) * mm, "end": v(-54.86, -12.18) * mm});
            skArc(sketch, "E8.141.4", {"start": v(-54.86, -12.18) * mm, "mid": v(-54.98, -12.25) * mm, "end": v(-55.1, -12.31) * mm});
            skArc(sketch, "E8.141.5", {"start": v(-55.1, -12.31) * mm, "mid": v(-55.2, -12.4) * mm, "end": v(-55.22, -12.54) * mm});
            skArc(sketch, "E8.142.0", {"start": v(-54.92, -13.09) * mm, "mid": v(-55.05, -13.05) * mm, "end": v(-55.13, -12.93) * mm});
            skArc(sketch, "E8.142.1", {"start": v(-54.65, -13.1) * mm, "mid": v(-54.78, -13.09) * mm, "end": v(-54.92, -13.09) * mm});
            skArc(sketch, "E8.142.2", {"start": v(-54.22, -13.52) * mm, "mid": v(-54.37, -13.25) * mm, "end": v(-54.65, -13.1) * mm});
            skArc(sketch, "E8.142.3", {"start": v(-54.22, -13.52) * mm, "mid": v(-54.23, -13.83) * mm, "end": v(-54.4, -14.09) * mm});
            skArc(sketch, "E8.142.4", {"start": v(-54.4, -14.09) * mm, "mid": v(-54.52, -14.17) * mm, "end": v(-54.64, -14.23) * mm});
            skArc(sketch, "E8.142.5", {"start": v(-54.64, -14.23) * mm, "mid": v(-54.73, -14.32) * mm, "end": v(-54.75, -14.46) * mm});
            skArc(sketch, "E8.143.0", {"start": v(-54.43, -15) * mm, "mid": v(-54.56, -14.96) * mm, "end": v(-54.64, -14.85) * mm});
            skArc(sketch, "E8.143.1", {"start": v(-54.16, -15) * mm, "mid": v(-54.3, -15) * mm, "end": v(-54.43, -15) * mm});
            skArc(sketch, "E8.143.2", {"start": v(-53.71, -15.4) * mm, "mid": v(-53.88, -15.14) * mm, "end": v(-54.16, -15) * mm});
            skArc(sketch, "E8.143.3", {"start": v(-53.71, -15.4) * mm, "mid": v(-53.71, -15.71) * mm, "end": v(-53.88, -15.98) * mm});
            skArc(sketch, "E8.143.4", {"start": v(-53.88, -15.98) * mm, "mid": v(-53.99, -16.06) * mm, "end": v(-54.1, -16.13) * mm});
            skArc(sketch, "E8.143.5", {"start": v(-54.1, -16.13) * mm, "mid": v(-54.2, -16.23) * mm, "end": v(-54.2, -16.36) * mm});
            skArc(sketch, "E8.144.0", {"start": v(-53.87, -16.89) * mm, "mid": v(-54, -16.86) * mm, "end": v(-54.1, -16.75) * mm});
            skArc(sketch, "E8.144.1", {"start": v(-53.6, -16.88) * mm, "mid": v(-53.74, -16.88) * mm, "end": v(-53.87, -16.89) * mm});
            skArc(sketch, "E8.144.2", {"start": v(-53.14, -17.27) * mm, "mid": v(-53.32, -17) * mm, "end": v(-53.6, -16.88) * mm});
            skArc(sketch, "E8.144.3", {"start": v(-53.14, -17.27) * mm, "mid": v(-53.13, -17.58) * mm, "end": v(-53.29, -17.85) * mm});
            skArc(sketch, "E8.144.4", {"start": v(-53.29, -17.85) * mm, "mid": v(-53.4, -17.93) * mm, "end": v(-53.5, -18) * mm});
            skArc(sketch, "E8.144.5", {"start": v(-53.5, -18) * mm, "mid": v(-53.6, -18.1) * mm, "end": v(-53.6, -18.25) * mm});
            skArc(sketch, "E8.145.0", {"start": v(-53.25, -18.76) * mm, "mid": v(-53.39, -18.73) * mm, "end": v(-53.48, -18.63) * mm});
            skArc(sketch, "E8.145.1", {"start": v(-52.98, -18.74) * mm, "mid": v(-53.12, -18.74) * mm, "end": v(-53.25, -18.76) * mm});
            skArc(sketch, "E8.145.2", {"start": v(-52.5, -19.11) * mm, "mid": v(-52.7, -18.86) * mm, "end": v(-52.98, -18.74) * mm});
            skArc(sketch, "E8.145.3", {"start": v(-52.5, -19.11) * mm, "mid": v(-52.49, -19.42) * mm, "end": v(-52.63, -19.7) * mm});
            skArc(sketch, "E8.145.4", {"start": v(-52.63, -19.7) * mm, "mid": v(-52.74, -19.79) * mm, "end": v(-52.85, -19.86) * mm});
            skArc(sketch, "E8.145.5", {"start": v(-52.85, -19.86) * mm, "mid": v(-52.94, -19.97) * mm, "end": v(-52.94, -20.1) * mm});
            skArc(sketch, "E8.146.0", {"start": v(-52.56, -20.6) * mm, "mid": v(-52.7, -20.58) * mm, "end": v(-52.8, -20.48) * mm});
            skArc(sketch, "E8.146.1", {"start": v(-52.3, -20.58) * mm, "mid": v(-52.43, -20.58) * mm, "end": v(-52.56, -20.6) * mm});
            skArc(sketch, "E8.146.2", {"start": v(-51.8, -20.93) * mm, "mid": v(-52, -20.69) * mm, "end": v(-52.3, -20.58) * mm});
            skArc(sketch, "E8.146.3", {"start": v(-51.8, -20.93) * mm, "mid": v(-51.78, -21.24) * mm, "end": v(-51.92, -21.52) * mm});
            skArc(sketch, "E8.146.4", {"start": v(-51.92, -21.52) * mm, "mid": v(-52.01, -21.61) * mm, "end": v(-52.12, -21.7) * mm});
            skArc(sketch, "E8.146.5", {"start": v(-52.12, -21.7) * mm, "mid": v(-52.2, -21.8) * mm, "end": v(-52.2, -21.94) * mm});
            skArc(sketch, "E8.147.0", {"start": v(-51.81, -22.43) * mm, "mid": v(-51.95, -22.41) * mm, "end": v(-52.05, -22.31) * mm});
            skArc(sketch, "E8.147.1", {"start": v(-51.54, -22.4) * mm, "mid": v(-51.68, -22.4) * mm, "end": v(-51.81, -22.43) * mm});
            skArc(sketch, "E8.147.2", {"start": v(-51.05, -22.73) * mm, "mid": v(-51.25, -22.49) * mm, "end": v(-51.54, -22.4) * mm});
            skArc(sketch, "E8.147.3", {"start": v(-51.05, -22.73) * mm, "mid": v(-51, -23.04) * mm, "end": v(-51.13, -23.32) * mm});
            skArc(sketch, "E8.147.4", {"start": v(-51.13, -23.32) * mm, "mid": v(-51.23, -23.42) * mm, "end": v(-51.33, -23.5) * mm});
            skArc(sketch, "E8.147.5", {"start": v(-51.33, -23.5) * mm, "mid": v(-51.42, -23.61) * mm, "end": v(-51.4, -23.75) * mm});
            skArc(sketch, "E8.148.0", {"start": v(-51, -24.22) * mm, "mid": v(-51.14, -24.2) * mm, "end": v(-51.24, -24.11) * mm});
            skArc(sketch, "E8.148.1", {"start": v(-50.73, -24.18) * mm, "mid": v(-50.87, -24.2) * mm, "end": v(-51, -24.22) * mm});
            skArc(sketch, "E8.148.2", {"start": v(-50.22, -24.5) * mm, "mid": v(-50.43, -24.26) * mm, "end": v(-50.73, -24.18) * mm});
            skArc(sketch, "E8.148.3", {"start": v(-50.22, -24.5) * mm, "mid": v(-50.17, -24.8) * mm, "end": v(-50.29, -25.1) * mm});
            skArc(sketch, "E8.148.4", {"start": v(-50.29, -25.1) * mm, "mid": v(-50.38, -25.19) * mm, "end": v(-50.48, -25.28) * mm});
            skArc(sketch, "E8.148.5", {"start": v(-50.48, -25.28) * mm, "mid": v(-50.56, -25.4) * mm, "end": v(-50.54, -25.53) * mm});
            skArc(sketch, "E8.149.0", {"start": v(-50.12, -25.98) * mm, "mid": v(-50.26, -25.98) * mm, "end": v(-50.36, -25.89) * mm});
            skArc(sketch, "E8.149.1", {"start": v(-49.86, -25.94) * mm, "mid": v(-50, -25.95) * mm, "end": v(-50.12, -25.98) * mm});
            skArc(sketch, "E8.149.2", {"start": v(-49.34, -26.23) * mm, "mid": v(-49.55, -26) * mm, "end": v(-49.86, -25.94) * mm});
            skArc(sketch, "E8.149.3", {"start": v(-49.34, -26.23) * mm, "mid": v(-49.27, -26.54) * mm, "end": v(-49.38, -26.83) * mm});
            skArc(sketch, "E8.149.4", {"start": v(-49.38, -26.83) * mm, "mid": v(-49.47, -26.93) * mm, "end": v(-49.57, -27.02) * mm});
            skArc(sketch, "E8.149.5", {"start": v(-49.57, -27.02) * mm, "mid": v(-49.64, -27.14) * mm, "end": v(-49.62, -27.28) * mm});
            skArc(sketch, "E8.150.0", {"start": v(-49.18, -27.72) * mm, "mid": v(-49.32, -27.72) * mm, "end": v(-49.43, -27.63) * mm});
            skArc(sketch, "E8.150.1", {"start": v(-48.92, -27.66) * mm, "mid": v(-49.05, -27.68) * mm, "end": v(-49.18, -27.72) * mm});
            skArc(sketch, "E8.150.2", {"start": v(-48.39, -27.94) * mm, "mid": v(-48.62, -27.72) * mm, "end": v(-48.92, -27.66) * mm});
            skArc(sketch, "E8.150.3", {"start": v(-48.39, -27.94) * mm, "mid": v(-48.32, -28.24) * mm, "end": v(-48.41, -28.54) * mm});
            skArc(sketch, "E8.150.4", {"start": v(-48.41, -28.54) * mm, "mid": v(-48.5, -28.64) * mm, "end": v(-48.6, -28.74) * mm});
            skArc(sketch, "E8.150.5", {"start": v(-48.6, -28.74) * mm, "mid": v(-48.67, -28.86) * mm, "end": v(-48.64, -29) * mm});
            skArc(sketch, "E8.151.0", {"start": v(-48.19, -29.42) * mm, "mid": v(-48.33, -29.42) * mm, "end": v(-48.43, -29.34) * mm});
            skArc(sketch, "E8.151.1", {"start": v(-47.93, -29.35) * mm, "mid": v(-48.06, -29.38) * mm, "end": v(-48.19, -29.42) * mm});
            skArc(sketch, "E8.151.2", {"start": v(-47.39, -29.6) * mm, "mid": v(-47.62, -29.4) * mm, "end": v(-47.93, -29.35) * mm});
            skArc(sketch, "E8.151.3", {"start": v(-47.39, -29.6) * mm, "mid": v(-47.3, -29.91) * mm, "end": v(-47.39, -30.2) * mm});
            skArc(sketch, "E8.151.4", {"start": v(-47.39, -30.2) * mm, "mid": v(-47.47, -30.32) * mm, "end": v(-47.56, -30.41) * mm});
            skArc(sketch, "E8.151.5", {"start": v(-47.56, -30.41) * mm, "mid": v(-47.63, -30.54) * mm, "end": v(-47.6, -30.67) * mm});
            skArc(sketch, "E8.152.0", {"start": v(-47.13, -31.08) * mm, "mid": v(-47.27, -31.1) * mm, "end": v(-47.38, -31) * mm});
            skArc(sketch, "E8.152.1", {"start": v(-46.87, -31) * mm, "mid": v(-47, -31.03) * mm, "end": v(-47.13, -31.08) * mm});
            skArc(sketch, "E8.152.2", {"start": v(-46.32, -31.25) * mm, "mid": v(-46.56, -31.05) * mm, "end": v(-46.87, -31) * mm});
            skArc(sketch, "E8.152.3", {"start": v(-46.32, -31.25) * mm, "mid": v(-46.23, -31.54) * mm, "end": v(-46.3, -31.84) * mm});
            skArc(sketch, "E8.152.4", {"start": v(-46.3, -31.84) * mm, "mid": v(-46.38, -31.96) * mm, "end": v(-46.47, -32.06) * mm});
            skArc(sketch, "E8.152.5", {"start": v(-46.47, -32.06) * mm, "mid": v(-46.53, -32.18) * mm, "end": v(-46.5, -32.31) * mm});
            skArc(sketch, "E8.153.0", {"start": v(-46.02, -32.7) * mm, "mid": v(-46.16, -32.72) * mm, "end": v(-46.27, -32.64) * mm});
            skArc(sketch, "E8.153.1", {"start": v(-45.76, -32.62) * mm, "mid": v(-45.9, -32.66) * mm, "end": v(-46.02, -32.7) * mm});
            skArc(sketch, "E8.153.2", {"start": v(-45.2, -32.84) * mm, "mid": v(-45.45, -32.65) * mm, "end": v(-45.76, -32.62) * mm});
            skArc(sketch, "E8.153.3", {"start": v(-45.2, -32.84) * mm, "mid": v(-45.1, -33.14) * mm, "end": v(-45.17, -33.44) * mm});
            skArc(sketch, "E8.153.4", {"start": v(-45.17, -33.44) * mm, "mid": v(-45.24, -33.56) * mm, "end": v(-45.33, -33.66) * mm});
            skArc(sketch, "E8.153.5", {"start": v(-45.33, -33.66) * mm, "mid": v(-45.38, -33.78) * mm, "end": v(-45.34, -33.92) * mm});
            skArc(sketch, "E8.154.0", {"start": v(-44.85, -34.3) * mm, "mid": v(-44.99, -34.31) * mm, "end": v(-45.1, -34.24) * mm});
            skArc(sketch, "E8.154.1", {"start": v(-44.6, -34.2) * mm, "mid": v(-44.73, -34.24) * mm, "end": v(-44.85, -34.3) * mm});
            skArc(sketch, "E8.154.2", {"start": v(-44.03, -34.4) * mm, "mid": v(-44.28, -34.22) * mm, "end": v(-44.6, -34.2) * mm});
            skArc(sketch, "E8.154.3", {"start": v(-44.03, -34.4) * mm, "mid": v(-43.91, -34.7) * mm, "end": v(-43.97, -35) * mm});
            skArc(sketch, "E8.154.4", {"start": v(-43.97, -35) * mm, "mid": v(-44.04, -35.11) * mm, "end": v(-44.12, -35.22) * mm});
            skArc(sketch, "E8.154.5", {"start": v(-44.12, -35.22) * mm, "mid": v(-44.18, -35.35) * mm, "end": v(-44.13, -35.48) * mm});
            skArc(sketch, "E8.155.0", {"start": v(-43.62, -35.84) * mm, "mid": v(-43.76, -35.86) * mm, "end": v(-43.88, -35.8) * mm});
            skArc(sketch, "E8.155.1", {"start": v(-43.37, -35.73) * mm, "mid": v(-43.5, -35.78) * mm, "end": v(-43.62, -35.84) * mm});
            skArc(sketch, "E8.155.2", {"start": v(-42.8, -35.92) * mm, "mid": v(-43.06, -35.74) * mm, "end": v(-43.37, -35.73) * mm});
            skArc(sketch, "E8.155.3", {"start": v(-42.8, -35.92) * mm, "mid": v(-42.68, -36.2) * mm, "end": v(-42.72, -36.51) * mm});
            skArc(sketch, "E8.155.4", {"start": v(-42.72, -36.51) * mm, "mid": v(-42.79, -36.63) * mm, "end": v(-42.87, -36.74) * mm});
            skArc(sketch, "E8.155.5", {"start": v(-42.87, -36.74) * mm, "mid": v(-42.92, -36.87) * mm, "end": v(-42.87, -37) * mm});
            skArc(sketch, "E8.156.0", {"start": v(-42.35, -37.34) * mm, "mid": v(-42.48, -37.37) * mm, "end": v(-42.6, -37.3) * mm});
            skArc(sketch, "E8.156.1", {"start": v(-42.1, -37.23) * mm, "mid": v(-42.23, -37.27) * mm, "end": v(-42.35, -37.34) * mm});
            skArc(sketch, "E8.156.2", {"start": v(-41.52, -37.39) * mm, "mid": v(-41.79, -37.22) * mm, "end": v(-42.1, -37.23) * mm});
            skArc(sketch, "E8.156.3", {"start": v(-41.52, -37.39) * mm, "mid": v(-41.39, -37.67) * mm, "end": v(-41.42, -37.98) * mm});
            skArc(sketch, "E8.156.4", {"start": v(-41.42, -37.98) * mm, "mid": v(-41.48, -38.1) * mm, "end": v(-41.56, -38.21) * mm});
            skArc(sketch, "E8.156.5", {"start": v(-41.56, -38.21) * mm, "mid": v(-41.6, -38.34) * mm, "end": v(-41.55, -38.47) * mm});
            skArc(sketch, "E8.157.0", {"start": v(-41.02, -38.8) * mm, "mid": v(-41.15, -38.83) * mm, "end": v(-41.28, -38.77) * mm});
            skArc(sketch, "E8.157.1", {"start": v(-40.78, -38.67) * mm, "mid": v(-40.9, -38.73) * mm, "end": v(-41.02, -38.8) * mm});
            skArc(sketch, "E8.157.2", {"start": v(-40.2, -38.81) * mm, "mid": v(-40.46, -38.66) * mm, "end": v(-40.78, -38.67) * mm});
            skArc(sketch, "E8.157.3", {"start": v(-40.2, -38.81) * mm, "mid": v(-40.05, -39.1) * mm, "end": v(-40.07, -39.4) * mm});
            skArc(sketch, "E8.157.4", {"start": v(-40.07, -39.4) * mm, "mid": v(-40.13, -39.52) * mm, "end": v(-40.2, -39.64) * mm});
            skArc(sketch, "E8.157.5", {"start": v(-40.2, -39.64) * mm, "mid": v(-40.24, -39.77) * mm, "end": v(-40.18, -39.9) * mm});
            skArc(sketch, "E8.158.0", {"start": v(-39.64, -40.2) * mm, "mid": v(-39.77, -40.24) * mm, "end": v(-39.9, -40.18) * mm});
            skArc(sketch, "E8.158.1", {"start": v(-39.4, -40.07) * mm, "mid": v(-39.52, -40.13) * mm, "end": v(-39.64, -40.2) * mm});
            skArc(sketch, "E8.158.2", {"start": v(-38.81, -40.2) * mm, "mid": v(-39.1, -40.05) * mm, "end": v(-39.4, -40.07) * mm});
            skArc(sketch, "E8.158.3", {"start": v(-38.81, -40.2) * mm, "mid": v(-38.66, -40.46) * mm, "end": v(-38.67, -40.78) * mm});
            skArc(sketch, "E8.158.4", {"start": v(-38.67, -40.78) * mm, "mid": v(-38.73, -40.9) * mm, "end": v(-38.8, -41.02) * mm});
            skArc(sketch, "E8.158.5", {"start": v(-38.8, -41.02) * mm, "mid": v(-38.83, -41.15) * mm, "end": v(-38.77, -41.28) * mm});
            skArc(sketch, "E8.159.0", {"start": v(-38.21, -41.56) * mm, "mid": v(-38.34, -41.6) * mm, "end": v(-38.47, -41.55) * mm});
            skArc(sketch, "E8.159.1", {"start": v(-37.98, -41.42) * mm, "mid": v(-38.1, -41.48) * mm, "end": v(-38.21, -41.56) * mm});
            skArc(sketch, "E8.159.2", {"start": v(-37.39, -41.52) * mm, "mid": v(-37.67, -41.39) * mm, "end": v(-37.98, -41.42) * mm});
            skArc(sketch, "E8.159.3", {"start": v(-37.39, -41.52) * mm, "mid": v(-37.22, -41.79) * mm, "end": v(-37.23, -42.1) * mm});
            skArc(sketch, "E8.159.4", {"start": v(-37.23, -42.1) * mm, "mid": v(-37.27, -42.23) * mm, "end": v(-37.34, -42.35) * mm});
            skArc(sketch, "E8.159.5", {"start": v(-37.34, -42.35) * mm, "mid": v(-37.37, -42.48) * mm, "end": v(-37.3, -42.6) * mm});
            skArc(sketch, "E8.160.0", {"start": v(-36.74, -42.87) * mm, "mid": v(-36.87, -42.92) * mm, "end": v(-37, -42.87) * mm});
            skArc(sketch, "E8.160.1", {"start": v(-36.51, -42.72) * mm, "mid": v(-36.63, -42.79) * mm, "end": v(-36.74, -42.87) * mm});
            skArc(sketch, "E8.160.2", {"start": v(-35.92, -42.8) * mm, "mid": v(-36.2, -42.68) * mm, "end": v(-36.51, -42.72) * mm});
            skArc(sketch, "E8.160.3", {"start": v(-35.92, -42.8) * mm, "mid": v(-35.74, -43.06) * mm, "end": v(-35.73, -43.37) * mm});
            skArc(sketch, "E8.160.4", {"start": v(-35.73, -43.37) * mm, "mid": v(-35.78, -43.5) * mm, "end": v(-35.84, -43.62) * mm});
            skArc(sketch, "E8.160.5", {"start": v(-35.84, -43.62) * mm, "mid": v(-35.86, -43.76) * mm, "end": v(-35.8, -43.88) * mm});
            skArc(sketch, "E8.161.0", {"start": v(-35.22, -44.12) * mm, "mid": v(-35.35, -44.18) * mm, "end": v(-35.48, -44.13) * mm});
            skArc(sketch, "E8.161.1", {"start": v(-35, -43.97) * mm, "mid": v(-35.11, -44.04) * mm, "end": v(-35.22, -44.12) * mm});
            skArc(sketch, "E8.161.2", {"start": v(-34.4, -44.03) * mm, "mid": v(-34.7, -43.91) * mm, "end": v(-35, -43.97) * mm});
            skArc(sketch, "E8.161.3", {"start": v(-34.4, -44.03) * mm, "mid": v(-34.22, -44.28) * mm, "end": v(-34.2, -44.6) * mm});
            skArc(sketch, "E8.161.4", {"start": v(-34.2, -44.6) * mm, "mid": v(-34.24, -44.73) * mm, "end": v(-34.3, -44.85) * mm});
            skArc(sketch, "E8.161.5", {"start": v(-34.3, -44.85) * mm, "mid": v(-34.31, -44.99) * mm, "end": v(-34.24, -45.1) * mm});
            skArc(sketch, "E8.162.0", {"start": v(-33.66, -45.33) * mm, "mid": v(-33.78, -45.38) * mm, "end": v(-33.92, -45.34) * mm});
            skArc(sketch, "E8.162.1", {"start": v(-33.44, -45.17) * mm, "mid": v(-33.56, -45.24) * mm, "end": v(-33.66, -45.33) * mm});
            skArc(sketch, "E8.162.2", {"start": v(-32.84, -45.2) * mm, "mid": v(-33.14, -45.1) * mm, "end": v(-33.44, -45.17) * mm});
            skArc(sketch, "E8.162.3", {"start": v(-32.84, -45.2) * mm, "mid": v(-32.65, -45.45) * mm, "end": v(-32.62, -45.76) * mm});
            skArc(sketch, "E8.162.4", {"start": v(-32.62, -45.76) * mm, "mid": v(-32.66, -45.9) * mm, "end": v(-32.7, -46.02) * mm});
            skArc(sketch, "E8.162.5", {"start": v(-32.7, -46.02) * mm, "mid": v(-32.72, -46.16) * mm, "end": v(-32.64, -46.27) * mm});
            skArc(sketch, "E8.163.0", {"start": v(-32.06, -46.47) * mm, "mid": v(-32.18, -46.53) * mm, "end": v(-32.31, -46.5) * mm});
            skArc(sketch, "E8.163.1", {"start": v(-31.84, -46.3) * mm, "mid": v(-31.96, -46.38) * mm, "end": v(-32.06, -46.47) * mm});
            skArc(sketch, "E8.163.2", {"start": v(-31.25, -46.32) * mm, "mid": v(-31.54, -46.23) * mm, "end": v(-31.84, -46.3) * mm});
            skArc(sketch, "E8.163.3", {"start": v(-31.25, -46.32) * mm, "mid": v(-31.05, -46.56) * mm, "end": v(-31, -46.87) * mm});
            skArc(sketch, "E8.163.4", {"start": v(-31, -46.87) * mm, "mid": v(-31.03, -47) * mm, "end": v(-31.08, -47.13) * mm});
            skArc(sketch, "E8.163.5", {"start": v(-31.08, -47.13) * mm, "mid": v(-31.1, -47.27) * mm, "end": v(-31, -47.38) * mm});
            skArc(sketch, "E8.164.0", {"start": v(-30.41, -47.56) * mm, "mid": v(-30.54, -47.63) * mm, "end": v(-30.67, -47.6) * mm});
            skArc(sketch, "E8.164.1", {"start": v(-30.2, -47.39) * mm, "mid": v(-30.32, -47.47) * mm, "end": v(-30.41, -47.56) * mm});
            skArc(sketch, "E8.164.2", {"start": v(-29.6, -47.39) * mm, "mid": v(-29.91, -47.3) * mm, "end": v(-30.2, -47.39) * mm});
            skArc(sketch, "E8.164.3", {"start": v(-29.6, -47.39) * mm, "mid": v(-29.4, -47.62) * mm, "end": v(-29.35, -47.93) * mm});
            skArc(sketch, "E8.164.4", {"start": v(-29.35, -47.93) * mm, "mid": v(-29.38, -48.06) * mm, "end": v(-29.42, -48.19) * mm});
            skArc(sketch, "E8.164.5", {"start": v(-29.42, -48.19) * mm, "mid": v(-29.42, -48.33) * mm, "end": v(-29.34, -48.43) * mm});
            skArc(sketch, "E8.165.0", {"start": v(-28.74, -48.6) * mm, "mid": v(-28.86, -48.67) * mm, "end": v(-29, -48.64) * mm});
            skArc(sketch, "E8.165.1", {"start": v(-28.54, -48.41) * mm, "mid": v(-28.64, -48.5) * mm, "end": v(-28.74, -48.6) * mm});
            skArc(sketch, "E8.165.2", {"start": v(-27.94, -48.39) * mm, "mid": v(-28.24, -48.32) * mm, "end": v(-28.54, -48.41) * mm});
            skArc(sketch, "E8.165.3", {"start": v(-27.94, -48.39) * mm, "mid": v(-27.72, -48.62) * mm, "end": v(-27.66, -48.92) * mm});
            skArc(sketch, "E8.165.4", {"start": v(-27.66, -48.92) * mm, "mid": v(-27.68, -49.05) * mm, "end": v(-27.72, -49.18) * mm});
            skArc(sketch, "E8.165.5", {"start": v(-27.72, -49.18) * mm, "mid": v(-27.72, -49.32) * mm, "end": v(-27.63, -49.43) * mm});
            skArc(sketch, "E8.166.0", {"start": v(-27.02, -49.57) * mm, "mid": v(-27.14, -49.64) * mm, "end": v(-27.28, -49.62) * mm});
            skArc(sketch, "E8.166.1", {"start": v(-26.83, -49.38) * mm, "mid": v(-26.93, -49.47) * mm, "end": v(-27.02, -49.57) * mm});
            skArc(sketch, "E8.166.2", {"start": v(-26.23, -49.34) * mm, "mid": v(-26.54, -49.27) * mm, "end": v(-26.83, -49.38) * mm});
            skArc(sketch, "E8.166.3", {"start": v(-26.23, -49.34) * mm, "mid": v(-26, -49.55) * mm, "end": v(-25.94, -49.86) * mm});
            skArc(sketch, "E8.166.4", {"start": v(-25.94, -49.86) * mm, "mid": v(-25.95, -50) * mm, "end": v(-25.98, -50.12) * mm});
            skArc(sketch, "E8.166.5", {"start": v(-25.98, -50.12) * mm, "mid": v(-25.98, -50.26) * mm, "end": v(-25.89, -50.36) * mm});
            skArc(sketch, "E8.167.0", {"start": v(-25.28, -50.48) * mm, "mid": v(-25.4, -50.56) * mm, "end": v(-25.53, -50.54) * mm});
            skArc(sketch, "E8.167.1", {"start": v(-25.1, -50.29) * mm, "mid": v(-25.19, -50.38) * mm, "end": v(-25.28, -50.48) * mm});
            skArc(sketch, "E8.167.2", {"start": v(-24.5, -50.22) * mm, "mid": v(-24.8, -50.17) * mm, "end": v(-25.1, -50.29) * mm});
            skArc(sketch, "E8.167.3", {"start": v(-24.5, -50.22) * mm, "mid": v(-24.26, -50.43) * mm, "end": v(-24.18, -50.73) * mm});
            skArc(sketch, "E8.167.4", {"start": v(-24.18, -50.73) * mm, "mid": v(-24.2, -50.87) * mm, "end": v(-24.22, -51) * mm});
            skArc(sketch, "E8.167.5", {"start": v(-24.22, -51) * mm, "mid": v(-24.2, -51.14) * mm, "end": v(-24.11, -51.24) * mm});
            skArc(sketch, "E8.168.0", {"start": v(-23.5, -51.33) * mm, "mid": v(-23.61, -51.42) * mm, "end": v(-23.75, -51.4) * mm});
            skArc(sketch, "E8.168.1", {"start": v(-23.32, -51.13) * mm, "mid": v(-23.42, -51.23) * mm, "end": v(-23.5, -51.33) * mm});
            skArc(sketch, "E8.168.2", {"start": v(-22.73, -51.05) * mm, "mid": v(-23.04, -51) * mm, "end": v(-23.32, -51.13) * mm});
            skArc(sketch, "E8.168.3", {"start": v(-22.73, -51.05) * mm, "mid": v(-22.49, -51.25) * mm, "end": v(-22.4, -51.54) * mm});
            skArc(sketch, "E8.168.4", {"start": v(-22.4, -51.54) * mm, "mid": v(-22.4, -51.68) * mm, "end": v(-22.43, -51.81) * mm});
            skArc(sketch, "E8.168.5", {"start": v(-22.43, -51.81) * mm, "mid": v(-22.41, -51.95) * mm, "end": v(-22.31, -52.05) * mm});
            skArc(sketch, "E8.169.0", {"start": v(-21.7, -52.12) * mm, "mid": v(-21.8, -52.2) * mm, "end": v(-21.94, -52.2) * mm});
            skArc(sketch, "E8.169.1", {"start": v(-21.52, -51.92) * mm, "mid": v(-21.61, -52.01) * mm, "end": v(-21.7, -52.12) * mm});
            skArc(sketch, "E8.169.2", {"start": v(-20.93, -51.8) * mm, "mid": v(-21.24, -51.78) * mm, "end": v(-21.52, -51.92) * mm});
            skArc(sketch, "E8.169.3", {"start": v(-20.93, -51.8) * mm, "mid": v(-20.69, -52) * mm, "end": v(-20.58, -52.3) * mm});
            skArc(sketch, "E8.169.4", {"start": v(-20.58, -52.3) * mm, "mid": v(-20.58, -52.43) * mm, "end": v(-20.6, -52.56) * mm});
            skArc(sketch, "E8.169.5", {"start": v(-20.6, -52.56) * mm, "mid": v(-20.58, -52.7) * mm, "end": v(-20.48, -52.8) * mm});
            skArc(sketch, "E8.170.0", {"start": v(-19.86, -52.85) * mm, "mid": v(-19.97, -52.94) * mm, "end": v(-20.1, -52.94) * mm});
            skArc(sketch, "E8.170.1", {"start": v(-19.7, -52.63) * mm, "mid": v(-19.79, -52.74) * mm, "end": v(-19.86, -52.85) * mm});
            skArc(sketch, "E8.170.2", {"start": v(-19.11, -52.5) * mm, "mid": v(-19.42, -52.49) * mm, "end": v(-19.7, -52.63) * mm});
            skArc(sketch, "E8.170.3", {"start": v(-19.11, -52.5) * mm, "mid": v(-18.86, -52.7) * mm, "end": v(-18.74, -52.98) * mm});
            skArc(sketch, "E8.170.4", {"start": v(-18.74, -52.98) * mm, "mid": v(-18.74, -53.12) * mm, "end": v(-18.76, -53.25) * mm});
            skArc(sketch, "E8.170.5", {"start": v(-18.76, -53.25) * mm, "mid": v(-18.73, -53.39) * mm, "end": v(-18.63, -53.48) * mm});
            skArc(sketch, "E8.171.0", {"start": v(-18, -53.5) * mm, "mid": v(-18.1, -53.6) * mm, "end": v(-18.25, -53.6) * mm});
            skArc(sketch, "E8.171.1", {"start": v(-17.85, -53.29) * mm, "mid": v(-17.93, -53.4) * mm, "end": v(-18, -53.5) * mm});
            skArc(sketch, "E8.171.2", {"start": v(-17.27, -53.14) * mm, "mid": v(-17.58, -53.13) * mm, "end": v(-17.85, -53.29) * mm});
            skArc(sketch, "E8.171.3", {"start": v(-17.27, -53.14) * mm, "mid": v(-17, -53.32) * mm, "end": v(-16.88, -53.6) * mm});
            skArc(sketch, "E8.171.4", {"start": v(-16.88, -53.6) * mm, "mid": v(-16.88, -53.74) * mm, "end": v(-16.89, -53.87) * mm});
            skArc(sketch, "E8.171.5", {"start": v(-16.89, -53.87) * mm, "mid": v(-16.86, -54) * mm, "end": v(-16.75, -54.1) * mm});
            skArc(sketch, "E8.172.0", {"start": v(-16.13, -54.1) * mm, "mid": v(-16.23, -54.2) * mm, "end": v(-16.36, -54.2) * mm});
            skArc(sketch, "E8.172.1", {"start": v(-15.98, -53.88) * mm, "mid": v(-16.06, -53.99) * mm, "end": v(-16.13, -54.1) * mm});
            skArc(sketch, "E8.172.2", {"start": v(-15.4, -53.71) * mm, "mid": v(-15.71, -53.71) * mm, "end": v(-15.98, -53.88) * mm});
            skArc(sketch, "E8.172.3", {"start": v(-15.4, -53.71) * mm, "mid": v(-15.14, -53.88) * mm, "end": v(-15, -54.16) * mm});
            skArc(sketch, "E8.172.4", {"start": v(-15, -54.16) * mm, "mid": v(-15, -54.3) * mm, "end": v(-15, -54.43) * mm});
            skArc(sketch, "E8.172.5", {"start": v(-15, -54.43) * mm, "mid": v(-14.96, -54.56) * mm, "end": v(-14.85, -54.64) * mm});
            skArc(sketch, "E8.173.0", {"start": v(-14.23, -54.64) * mm, "mid": v(-14.32, -54.73) * mm, "end": v(-14.46, -54.75) * mm});
            skArc(sketch, "E8.173.1", {"start": v(-14.09, -54.4) * mm, "mid": v(-14.17, -54.52) * mm, "end": v(-14.23, -54.64) * mm});
            skArc(sketch, "E8.173.2", {"start": v(-13.52, -54.22) * mm, "mid": v(-13.83, -54.23) * mm, "end": v(-14.09, -54.4) * mm});
            skArc(sketch, "E8.173.3", {"start": v(-13.52, -54.22) * mm, "mid": v(-13.25, -54.37) * mm, "end": v(-13.1, -54.65) * mm});
            skArc(sketch, "E8.173.4", {"start": v(-13.1, -54.65) * mm, "mid": v(-13.09, -54.78) * mm, "end": v(-13.09, -54.92) * mm});
            skArc(sketch, "E8.173.5", {"start": v(-13.09, -54.92) * mm, "mid": v(-13.05, -55.05) * mm, "end": v(-12.93, -55.13) * mm});
            skArc(sketch, "E8.174.0", {"start": v(-12.31, -55.1) * mm, "mid": v(-12.4, -55.2) * mm, "end": v(-12.54, -55.22) * mm});
            skArc(sketch, "E8.174.1", {"start": v(-12.18, -54.86) * mm, "mid": v(-12.25, -54.98) * mm, "end": v(-12.31, -55.1) * mm});
            skArc(sketch, "E8.174.2", {"start": v(-11.62, -54.65) * mm, "mid": v(-11.93, -54.68) * mm, "end": v(-12.18, -54.86) * mm});
            skArc(sketch, "E8.174.3", {"start": v(-11.62, -54.65) * mm, "mid": v(-11.34, -54.8) * mm, "end": v(-11.19, -55.07) * mm});
            skArc(sketch, "E8.174.4", {"start": v(-11.19, -55.07) * mm, "mid": v(-11.17, -55.2) * mm, "end": v(-11.16, -55.34) * mm});
            skArc(sketch, "E8.174.5", {"start": v(-11.16, -55.34) * mm, "mid": v(-11.12, -55.47) * mm, "end": v(-11, -55.55) * mm});
            skArc(sketch, "E8.175.0", {"start": v(-10.38, -55.5) * mm, "mid": v(-10.47, -55.6) * mm, "end": v(-10.6, -55.62) * mm});
            skArc(sketch, "E8.175.1", {"start": v(-10.26, -55.26) * mm, "mid": v(-10.33, -55.37) * mm, "end": v(-10.38, -55.5) * mm});
            skArc(sketch, "E8.175.2", {"start": v(-9.7, -55.03) * mm, "mid": v(-10.01, -55.06) * mm, "end": v(-10.26, -55.26) * mm});
            skArc(sketch, "E8.175.3", {"start": v(-9.7, -55.03) * mm, "mid": v(-9.42, -55.16) * mm, "end": v(-9.26, -55.43) * mm});
            skArc(sketch, "E8.175.4", {"start": v(-9.26, -55.43) * mm, "mid": v(-9.23, -55.56) * mm, "end": v(-9.22, -55.7) * mm});
            skArc(sketch, "E8.175.5", {"start": v(-9.22, -55.7) * mm, "mid": v(-9.18, -55.83) * mm, "end": v(-9.06, -55.9) * mm});
            skArc(sketch, "E8.176.0", {"start": v(-8.44, -55.82) * mm, "mid": v(-8.52, -55.93) * mm, "end": v(-8.66, -55.96) * mm});
            skArc(sketch, "E8.176.1", {"start": v(-8.32, -55.58) * mm, "mid": v(-8.39, -55.7) * mm, "end": v(-8.44, -55.82) * mm});
            skArc(sketch, "E8.176.2", {"start": v(-7.78, -55.33) * mm, "mid": v(-8.09, -55.38) * mm, "end": v(-8.32, -55.58) * mm});
            skArc(sketch, "E8.176.3", {"start": v(-7.78, -55.33) * mm, "mid": v(-7.5, -55.46) * mm, "end": v(-7.32, -55.72) * mm});
            skArc(sketch, "E8.176.4", {"start": v(-7.32, -55.72) * mm, "mid": v(-7.29, -55.85) * mm, "end": v(-7.27, -55.99) * mm});
            skArc(sketch, "E8.176.5", {"start": v(-7.27, -55.99) * mm, "mid": v(-7.22, -56.12) * mm, "end": v(-7.1, -56.18) * mm});
            skArc(sketch, "E8.177.0", {"start": v(-6.49, -56.08) * mm, "mid": v(-6.57, -56.2) * mm, "end": v(-6.7, -56.23) * mm});
            skArc(sketch, "E8.177.1", {"start": v(-6.38, -55.84) * mm, "mid": v(-6.44, -55.96) * mm, "end": v(-6.49, -56.08) * mm});
            skArc(sketch, "E8.177.2", {"start": v(-5.84, -55.57) * mm, "mid": v(-6.15, -55.62) * mm, "end": v(-6.38, -55.84) * mm});
            skArc(sketch, "E8.177.3", {"start": v(-5.84, -55.57) * mm, "mid": v(-5.55, -55.69) * mm, "end": v(-5.37, -55.94) * mm});
            skArc(sketch, "E8.177.4", {"start": v(-5.37, -55.94) * mm, "mid": v(-5.33, -56.07) * mm, "end": v(-5.32, -56.2) * mm});
            skArc(sketch, "E8.177.5", {"start": v(-5.32, -56.2) * mm, "mid": v(-5.26, -56.33) * mm, "end": v(-5.14, -56.4) * mm});
            skArc(sketch, "E8.178.0", {"start": v(-4.52, -56.28) * mm, "mid": v(-4.6, -56.4) * mm, "end": v(-4.74, -56.43) * mm});
            skArc(sketch, "E8.178.1", {"start": v(-4.43, -56.02) * mm, "mid": v(-4.48, -56.15) * mm, "end": v(-4.52, -56.28) * mm});
            skArc(sketch, "E8.178.2", {"start": v(-3.9, -55.74) * mm, "mid": v(-4.2, -55.8) * mm, "end": v(-4.43, -56.02) * mm});
            skArc(sketch, "E8.178.3", {"start": v(-3.9, -55.74) * mm, "mid": v(-3.6, -55.85) * mm, "end": v(-3.41, -56.1) * mm});
            skArc(sketch, "E8.178.4", {"start": v(-3.41, -56.1) * mm, "mid": v(-3.37, -56.22) * mm, "end": v(-3.35, -56.36) * mm});
            skArc(sketch, "E8.178.5", {"start": v(-3.35, -56.36) * mm, "mid": v(-3.3, -56.48) * mm, "end": v(-3.16, -56.54) * mm});
            skArc(sketch, "E8.179.0", {"start": v(-2.56, -56.4) * mm, "mid": v(-2.63, -56.52) * mm, "end": v(-2.76, -56.56) * mm});
            skArc(sketch, "E8.179.1", {"start": v(-2.47, -56.15) * mm, "mid": v(-2.52, -56.27) * mm, "end": v(-2.56, -56.4) * mm});
            skArc(sketch, "E8.179.2", {"start": v(-1.95, -55.84) * mm, "mid": v(-2.25, -55.92) * mm, "end": v(-2.47, -56.15) * mm});
            skArc(sketch, "E8.179.3", {"start": v(-1.95, -55.84) * mm, "mid": v(-1.65, -55.94) * mm, "end": v(-1.46, -56.18) * mm});
            skArc(sketch, "E8.179.4", {"start": v(-1.46, -56.18) * mm, "mid": v(-1.41, -56.3) * mm, "end": v(-1.38, -56.44) * mm});
            skArc(sketch, "E8.179.5", {"start": v(-1.38, -56.44) * mm, "mid": v(-1.32, -56.56) * mm, "end": v(-1.19, -56.61) * mm});
            skSolve(sketch);
        }
        {
            var Q0;
            Q0=makeQuery(id+"F0.imprint","IMPRINT",FACE,{"disambiguationData":[TD([[makeQuery(id+"F0.imprint","IMPRINT",EDGE,{"derivedFrom":sQuery(id+"F0.wireOp",EDGE,"E2")}),-1.0]])]});
            extrude(context, id + "F1", {"entities" : qUnion([Q0]), "depth" : 7 * mm});
        }
        {
            var Q0;
            Q0=makeQuery(id+"F1.opExtrude","CAP_FACE",FACE,{"disambiguationData":[OSD([sQuery(id+"F0.wireOp",EDGE,"E1"),sQuery(id+"F0.wireOp",EDGE,"E2"),sQuery(id+"F0.wireOp",EDGE,"E3"),sQuery(id+"F0.wireOp",EDGE,"E4"),sQuery(id+"F0.wireOp",EDGE,"E5.MirrorCS"),sQuery(id+"F0.wireOp",EDGE,"E6.MirrorCS"),sQuery(id+"F0.wireOp",EDGE,"E7.MirrorCS")])],"isStart":false});
            var sketch = newSketch(context, id + "F2", { "sketchPlane" : qUnion([Q0])});
            skCircle(sketch, "E9", {"center": v(0, 0) * mm, "radius": 56.63 * mm});
            skSolve(sketch);
        }
        {
            var Q0;
            Q0=qSketchRegion(id+"F2",true);
            extrude(context, id + "F3", {"entities" : qUnion([Q0]), "operationType" : NewBodyOperationType.ADD, "depth" : 1 * mm, "hasDraft" : true, "draftAngle" : 45 * degree});
        }
        {
            var Q0;
            Q0=makeQuery(id+"F1.opExtrude","CAP_FACE",FACE,{"disambiguationData":[OSD([sQuery(id+"F0.wireOp",EDGE,"E1"),sQuery(id+"F0.wireOp",EDGE,"E2"),sQuery(id+"F0.wireOp",EDGE,"E3"),sQuery(id+"F0.wireOp",EDGE,"E4"),sQuery(id+"F0.wireOp",EDGE,"E5.MirrorCS"),sQuery(id+"F0.wireOp",EDGE,"E6.MirrorCS"),sQuery(id+"F0.wireOp",EDGE,"E7.MirrorCS")])],"isStart":true});
            var sketch = newSketch(context, id + "F4", { "sketchPlane" : qUnion([Q0])});
            skCircle(sketch, "E10", {"center": v(0, 0) * mm, "radius": 56.63 * mm});
            skSolve(sketch);
        }
        {
            var Q0;
            Q0=qSketchRegion(id+"F4",true);
            extrude(context, id + "F5", {"entities" : qUnion([Q0]), "operationType" : NewBodyOperationType.ADD, "depth" : 1 * mm, "hasDraft" : true, "draftAngle" : 45 * degree});
        }
        {
            var Q0;
            Q0=makeQuery(id+"F5.opExtrude","CAP_FACE",FACE,{"disambiguationData":[OSD([sQuery(id+"F4.wireOp",EDGE,"E10")])],"isStart":false});
            var sketch = newSketch(context, id + "F6", { "sketchPlane" : qUnion([Q0])});
            skCircle(sketch, "E11", {"center": v(0, 0) * mm, "radius": 7.75 * mm});
            skSolve(sketch);
        }
        {
            var Q0;
            Q0=qSketchRegion(id+"F6",true);
            extrude(context, id + "F7", {"entities" : qUnion([Q0]), "operationType" : NewBodyOperationType.REMOVE, "oppositeDirection" : true, "depth" : 25 * mm});
        }
        {
            var Q0;
            Q0=makeQuery(id+"F5.opExtrude","CAP_FACE",FACE,{"disambiguationData":[OSD([sQuery(id+"F4.wireOp",EDGE,"E10")])],"isStart":false});
            var sketch = newSketch(context, id + "F8", { "sketchPlane" : qUnion([Q0])});
            skCircle(sketch, "E12", {"center": v(0, 0) * mm, "radius": 12 * mm});
            skSolve(sketch);
        }
        {
            var Q0;
            Q0=qSketchRegion(id+"F8",true);
            extrude(context, id + "F9", {"entities" : qUnion([Q0]), "operationType" : NewBodyOperationType.REMOVE, "oppositeDirection" : true, "depth" : 1.3 * mm});
        }
        {
            var Q0;
            Q0=makeQuery(id+"F3.opExtrude","CAP_FACE",FACE,{"disambiguationData":[OSD([sQuery(id+"F2.wireOp",EDGE,"E9")])],"isStart":false});
            var sketch = newSketch(context, id + "F10", { "sketchPlane" : qUnion([Q0])});
            skCircle(sketch, "E13", {"center": v(0, -27.5) * mm, "radius": 2.2 * mm});
            skCircle(sketch, "E14.1.0", {"center": v(27.5, 0) * mm, "radius": 2.2 * mm});
            skCircle(sketch, "E14.2.0", {"center": v(0, 27.5) * mm, "radius": 2.2 * mm});
            skCircle(sketch, "E14.3.0", {"center": v(-27.5, 0) * mm, "radius": 2.2 * mm});
            skPoint(sketch, "E14.center", {"position": v(0, 0) * mm});
            skSolve(sketch);
        }
        {
            var Q0;
            Q0=qSketchRegion(id+"F10",true);
            extrude(context, id + "F11", {"entities" : qUnion([Q0]), "operationType" : NewBodyOperationType.REMOVE, "oppositeDirection" : true, "depth" : 25 * mm});
        }
        {
            var Q0;
            Q0=makeQuery(id+"F3.opExtrude","CAP_FACE",FACE,{"disambiguationData":[OSD([sQuery(id+"F2.wireOp",EDGE,"E9")])],"isStart":false});
            var sketch = newSketch(context, id + "F12", { "sketchPlane" : qUnion([Q0])});
            skCircle(sketch, "E15", {"center": v(0, -27.5) * mm, "radius": 5 * mm});
            skCircle(sketch, "E16.1.0", {"center": v(27.5, 0) * mm, "radius": 5 * mm});
            skCircle(sketch, "E16.2.0", {"center": v(0, 27.5) * mm, "radius": 5 * mm});
            skCircle(sketch, "E16.3.0", {"center": v(-27.5, 0) * mm, "radius": 5 * mm});
            skPoint(sketch, "E16.center", {"position": v(0, 0) * mm});
            skSolve(sketch);
        }
        {
            var Q0;
            Q0=qSketchRegion(id+"F12",true);
            extrude(context, id + "F13", {"entities" : qUnion([Q0]), "operationType" : NewBodyOperationType.REMOVE, "oppositeDirection" : true, "depth" : 25 * mm, "hasDraft" : true, "draftAngle" : 60 * degree, "draftPullDirection" : true});
        }
        {
            var Q0;
            Q0=makeQuery(id+"F3.opExtrude","CAP_FACE",FACE,{"disambiguationData":[OSD([sQuery(id+"F2.wireOp",EDGE,"E9")])],"isStart":false});
            var sketch = newSketch(context, id + "F14", { "sketchPlane" : qUnion([Q0])});
            skArc(sketch, "E17", {"start": v(-42.69, -26.04) * mm, "mid": v(-35.36, -35.36) * mm, "end": v(-26.04, -42.69) * mm});
            skArc(sketch, "E18", {"start": v(-11.58, -9.54) * mm, "mid": v(-10.6, -10.6) * mm, "end": v(-9.54, -11.58) * mm});
            skLineSegment(sketch, "E19", {"start": v(-40.53, -18.9) * mm, "end": v(-17.55, -8.18) * mm});
            skLineSegment(sketch, "E20", {"start": v(-18.9, -40.53) * mm, "end": v(-8.18, -17.55) * mm});
            skLineSegment(sketch, "E21", {"start": v(-13.6, -6.34) * mm, "end": v(0, 0) * mm, "construction": true});
            skLineSegment(sketch, "E22", {"start": v(-6.34, -13.6) * mm, "end": v(0, 0) * mm, "construction": true});
            skArc(sketch, "E23", {"start": v(-5.52, -49.7) * mm, "mid": v(0, -50) * mm, "end": v(5.52, -49.7) * mm});
            skArc(sketch, "E24", {"start": v(-3.67, -36.82) * mm, "mid": v(0, -37) * mm, "end": v(3.67, -36.82) * mm});
            skLineSegment(sketch, "E25", {"start": v(-6.93, -39.28) * mm, "end": v(-8.14, -46.2) * mm});
            skLineSegment(sketch, "E26", {"start": v(6.93, -39.28) * mm, "end": v(8.14, -46.2) * mm});
            skLineSegment(sketch, "E27", {"start": v(-6.42, -36.44) * mm, "end": v(0, 0) * mm, "construction": true});
            skLineSegment(sketch, "E28", {"start": v(6.42, -36.44) * mm, "end": v(0, 0) * mm, "construction": true});
            skPoint(sketch, "E29.visualSharp", {"position": v(-13.6, -6.34) * mm});
            skArc(sketch, "E29.filletArc", {"start": v(-11.58, -9.54) * mm, "mid": v(-14.33, -7.84) * mm, "end": v(-17.55, -8.18) * mm});
            skPoint(sketch, "E30.visualSharp", {"position": v(-21.13, -45.32) * mm});
            skArc(sketch, "E30.filletArc", {"start": v(-26.04, -42.69) * mm, "mid": v(-21.99, -43.2) * mm, "end": v(-18.9, -40.53) * mm});
            skPoint(sketch, "E31.visualSharp", {"position": v(-6.34, -13.6) * mm});
            skArc(sketch, "E31.filletArc", {"start": v(-8.18, -17.55) * mm, "mid": v(-7.84, -14.33) * mm, "end": v(-9.54, -11.58) * mm});
            skArc(sketch, "E32.filletArc", {"start": v(-40.53, -18.9) * mm, "mid": v(-43.2, -21.99) * mm, "end": v(-42.69, -26.04) * mm});
            skPoint(sketch, "E33.visualSharp", {"position": v(6.42, -36.44) * mm});
            skArc(sketch, "E33.filletArc", {"start": v(6.93, -39.28) * mm, "mid": v(5.78, -37.41) * mm, "end": v(3.67, -36.82) * mm});
            skPoint(sketch, "E34.visualSharp", {"position": v(8.68, -49.24) * mm});
            skArc(sketch, "E34.filletArc", {"start": v(5.52, -49.7) * mm, "mid": v(7.6, -48.51) * mm, "end": v(8.14, -46.2) * mm});
            skPoint(sketch, "E35.visualSharp", {"position": v(-8.68, -49.24) * mm});
            skArc(sketch, "E35.filletArc", {"start": v(-8.14, -46.2) * mm, "mid": v(-7.6, -48.51) * mm, "end": v(-5.52, -49.7) * mm});
            skPoint(sketch, "E36.visualSharp", {"position": v(-6.42, -36.44) * mm});
            skArc(sketch, "E36.filletArc", {"start": v(-3.67, -36.82) * mm, "mid": v(-5.78, -37.41) * mm, "end": v(-6.93, -39.28) * mm});
            skLineSegment(sketch, "E37.1.0", {"start": v(18.9, -40.53) * mm, "end": v(8.18, -17.55) * mm});
            skArc(sketch, "E37.1.1", {"start": v(18.9, -40.53) * mm, "mid": v(21.99, -43.2) * mm, "end": v(26.04, -42.69) * mm});
            skArc(sketch, "E37.1.2", {"start": v(26.04, -42.69) * mm, "mid": v(35.36, -35.36) * mm, "end": v(42.69, -26.04) * mm});
            skArc(sketch, "E37.1.3", {"start": v(42.69, -26.04) * mm, "mid": v(43.2, -21.99) * mm, "end": v(40.53, -18.9) * mm});
            skLineSegment(sketch, "E37.1.4", {"start": v(40.53, -18.9) * mm, "end": v(17.55, -8.18) * mm});
            skArc(sketch, "E37.1.5", {"start": v(17.55, -8.18) * mm, "mid": v(14.33, -7.84) * mm, "end": v(11.58, -9.54) * mm});
            skArc(sketch, "E37.1.6", {"start": v(9.54, -11.58) * mm, "mid": v(10.6, -10.6) * mm, "end": v(11.58, -9.54) * mm});
            skArc(sketch, "E37.1.7", {"start": v(9.54, -11.58) * mm, "mid": v(7.84, -14.33) * mm, "end": v(8.18, -17.55) * mm});
            skLineSegment(sketch, "E37.1.8", {"start": v(39.28, -6.93) * mm, "end": v(46.2, -8.14) * mm});
            skArc(sketch, "E37.1.9", {"start": v(36.82, -3.67) * mm, "mid": v(37.41, -5.78) * mm, "end": v(39.28, -6.93) * mm});
            skArc(sketch, "E37.1.10", {"start": v(36.82, -3.67) * mm, "mid": v(37, 0) * mm, "end": v(36.82, 3.67) * mm});
            skArc(sketch, "E37.1.11", {"start": v(39.28, 6.93) * mm, "mid": v(37.41, 5.78) * mm, "end": v(36.82, 3.67) * mm});
            skLineSegment(sketch, "E37.1.12", {"start": v(39.28, 6.93) * mm, "end": v(46.2, 8.14) * mm});
            skArc(sketch, "E37.1.13", {"start": v(49.7, 5.52) * mm, "mid": v(48.51, 7.6) * mm, "end": v(46.2, 8.14) * mm});
            skArc(sketch, "E37.1.14", {"start": v(49.7, -5.52) * mm, "mid": v(50, 0) * mm, "end": v(49.7, 5.52) * mm});
            skArc(sketch, "E37.1.15", {"start": v(46.2, -8.14) * mm, "mid": v(48.51, -7.6) * mm, "end": v(49.7, -5.52) * mm});
            skLineSegment(sketch, "E37.2.0", {"start": v(40.53, 18.9) * mm, "end": v(17.55, 8.18) * mm});
            skArc(sketch, "E37.2.1", {"start": v(40.53, 18.9) * mm, "mid": v(43.2, 21.99) * mm, "end": v(42.69, 26.04) * mm});
            skArc(sketch, "E37.2.2", {"start": v(42.69, 26.04) * mm, "mid": v(35.36, 35.36) * mm, "end": v(26.04, 42.69) * mm});
            skArc(sketch, "E37.2.3", {"start": v(26.04, 42.69) * mm, "mid": v(21.99, 43.2) * mm, "end": v(18.9, 40.53) * mm});
            skLineSegment(sketch, "E37.2.4", {"start": v(18.9, 40.53) * mm, "end": v(8.18, 17.55) * mm});
            skArc(sketch, "E37.2.5", {"start": v(8.18, 17.55) * mm, "mid": v(7.84, 14.33) * mm, "end": v(9.54, 11.58) * mm});
            skArc(sketch, "E37.2.6", {"start": v(11.58, 9.54) * mm, "mid": v(10.6, 10.6) * mm, "end": v(9.54, 11.58) * mm});
            skArc(sketch, "E37.2.7", {"start": v(11.58, 9.54) * mm, "mid": v(14.33, 7.84) * mm, "end": v(17.55, 8.18) * mm});
            skLineSegment(sketch, "E37.2.8", {"start": v(6.93, 39.28) * mm, "end": v(8.14, 46.2) * mm});
            skArc(sketch, "E37.2.9", {"start": v(3.67, 36.82) * mm, "mid": v(5.78, 37.41) * mm, "end": v(6.93, 39.28) * mm});
            skArc(sketch, "E37.2.10", {"start": v(3.67, 36.82) * mm, "mid": v(0, 37) * mm, "end": v(-3.67, 36.82) * mm});
            skArc(sketch, "E37.2.11", {"start": v(-6.93, 39.28) * mm, "mid": v(-5.78, 37.41) * mm, "end": v(-3.67, 36.82) * mm});
            skLineSegment(sketch, "E37.2.12", {"start": v(-6.93, 39.28) * mm, "end": v(-8.14, 46.2) * mm});
            skArc(sketch, "E37.2.13", {"start": v(-5.52, 49.7) * mm, "mid": v(-7.6, 48.51) * mm, "end": v(-8.14, 46.2) * mm});
            skArc(sketch, "E37.2.14", {"start": v(5.52, 49.7) * mm, "mid": v(0, 50) * mm, "end": v(-5.52, 49.7) * mm});
            skArc(sketch, "E37.2.15", {"start": v(8.14, 46.2) * mm, "mid": v(7.6, 48.51) * mm, "end": v(5.52, 49.7) * mm});
            skLineSegment(sketch, "E37.3.0", {"start": v(-18.9, 40.53) * mm, "end": v(-8.18, 17.55) * mm});
            skArc(sketch, "E37.3.1", {"start": v(-18.9, 40.53) * mm, "mid": v(-21.99, 43.2) * mm, "end": v(-26.04, 42.69) * mm});
            skArc(sketch, "E37.3.2", {"start": v(-26.04, 42.69) * mm, "mid": v(-35.36, 35.36) * mm, "end": v(-42.69, 26.04) * mm});
            skArc(sketch, "E37.3.3", {"start": v(-42.69, 26.04) * mm, "mid": v(-43.2, 21.99) * mm, "end": v(-40.53, 18.9) * mm});
            skLineSegment(sketch, "E37.3.4", {"start": v(-40.53, 18.9) * mm, "end": v(-17.55, 8.18) * mm});
            skArc(sketch, "E37.3.5", {"start": v(-17.55, 8.18) * mm, "mid": v(-14.33, 7.84) * mm, "end": v(-11.58, 9.54) * mm});
            skArc(sketch, "E37.3.6", {"start": v(-9.54, 11.58) * mm, "mid": v(-10.6, 10.6) * mm, "end": v(-11.58, 9.54) * mm});
            skArc(sketch, "E37.3.7", {"start": v(-9.54, 11.58) * mm, "mid": v(-7.84, 14.33) * mm, "end": v(-8.18, 17.55) * mm});
            skLineSegment(sketch, "E37.3.8", {"start": v(-39.28, 6.93) * mm, "end": v(-46.2, 8.14) * mm});
            skArc(sketch, "E37.3.9", {"start": v(-36.82, 3.67) * mm, "mid": v(-37.41, 5.78) * mm, "end": v(-39.28, 6.93) * mm});
            skArc(sketch, "E37.3.10", {"start": v(-36.82, 3.67) * mm, "mid": v(-37, 0) * mm, "end": v(-36.82, -3.67) * mm});
            skArc(sketch, "E37.3.11", {"start": v(-39.28, -6.93) * mm, "mid": v(-37.41, -5.78) * mm, "end": v(-36.82, -3.67) * mm});
            skLineSegment(sketch, "E37.3.12", {"start": v(-39.28, -6.93) * mm, "end": v(-46.2, -8.14) * mm});
            skArc(sketch, "E37.3.13", {"start": v(-49.7, -5.52) * mm, "mid": v(-48.51, -7.6) * mm, "end": v(-46.2, -8.14) * mm});
            skArc(sketch, "E37.3.14", {"start": v(-49.7, 5.52) * mm, "mid": v(-50, 0) * mm, "end": v(-49.7, -5.52) * mm});
            skArc(sketch, "E37.3.15", {"start": v(-46.2, 8.14) * mm, "mid": v(-48.51, 7.6) * mm, "end": v(-49.7, 5.52) * mm});
            skSolve(sketch);
        }
        {
            var Q0;
            Q0=qSketchRegion(id+"F14",true);
            extrude(context, id + "F15", {"entities" : qUnion([Q0]), "operationType" : NewBodyOperationType.REMOVE, "oppositeDirection" : true, "depth" : 10 * mm});
        }
    });
